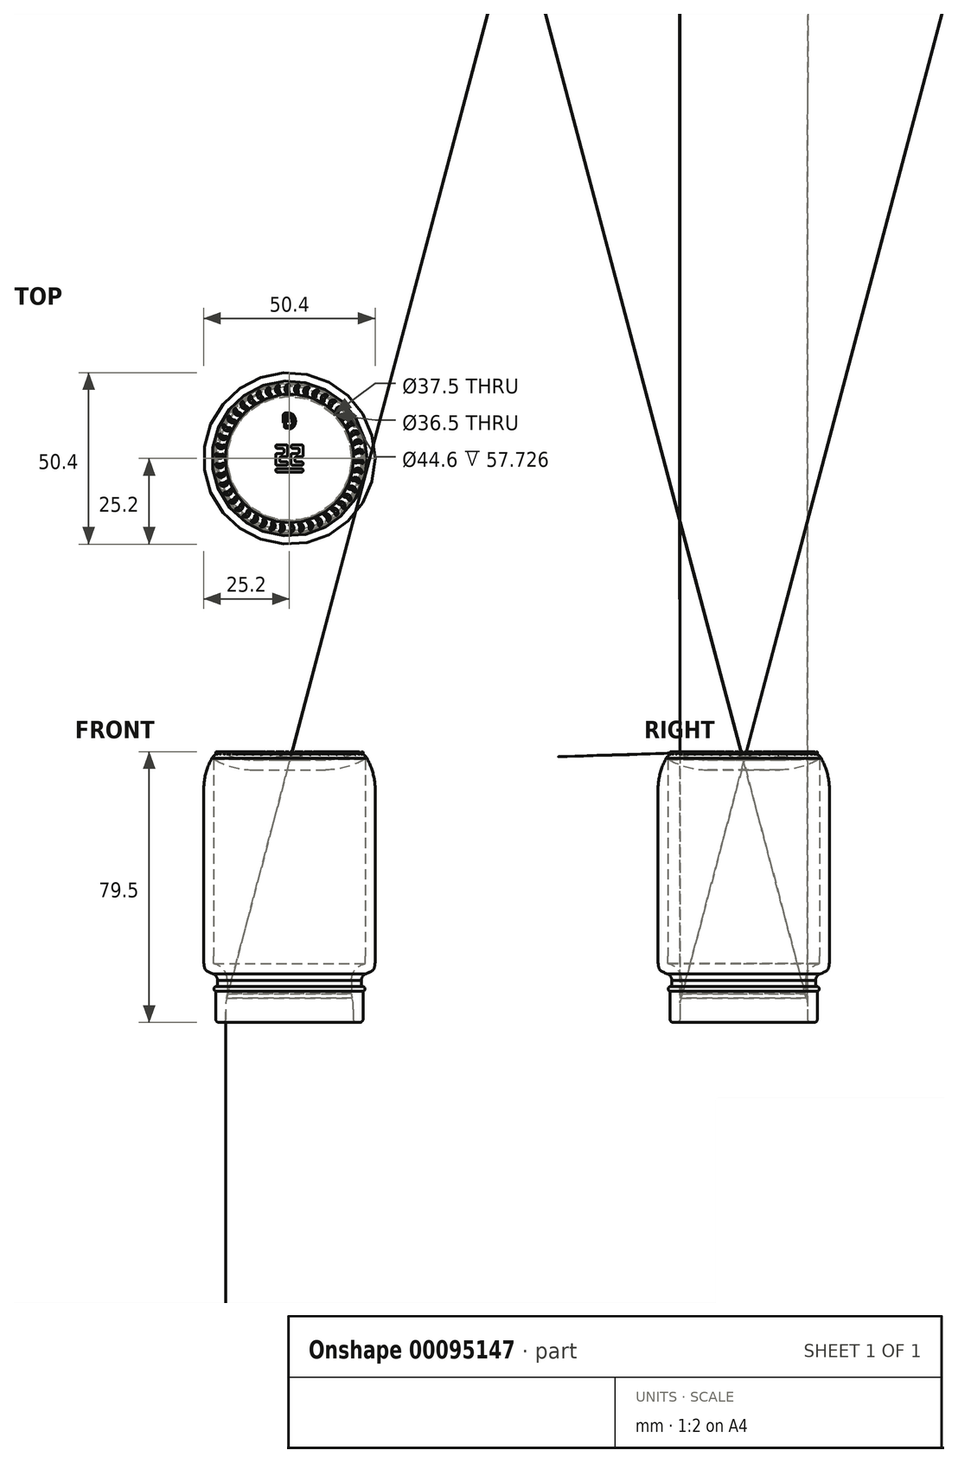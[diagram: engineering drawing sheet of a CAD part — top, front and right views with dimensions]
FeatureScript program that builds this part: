
annotation { "Feature Type Name" : "Feature", "Feature Type Description" : "" }
export const myFeature = defineFeature(function(context is Context, id is Id, definition is map)
    precondition{}
    {
        {
            var Q0;
            Q0=qCreatedBy(makeId("Top.planeOp"),FACE);
            var sketch = newSketch(context, id + "F0", { "sketchPlane" : qUnion([Q0])});
            skCircle(sketch, "E0", {"center": v(0, 0) * mm, "radius": 21.65 * mm});
            skCircle(sketch, "E1", {"center": v(0, 0) * mm, "radius": 25.2 * mm});
            skCircle(sketch, "E2", {"center": v(0, 0) * mm, "radius": 21.15 * mm});
            skCircle(sketch, "E3", {"center": v(0, 0) * mm, "radius": 22.15 * mm});
            skSolve(sketch);
        }
        {
            var Q0;
            Q0=makeQuery(id+"F0.imprint","IMPRINT",FACE,{"disambiguationData":[TD([[makeQuery(id+"F0.imprint","IMPRINT",EDGE,{"derivedFrom":sQuery(id+"F0.wireOp",EDGE,"E0")}),1.0]])]});
            var Q1;
            Q1=makeQuery(id+"F0.imprint","IMPRINT",FACE,{"disambiguationData":[TD([[makeQuery(id+"F0.imprint","IMPRINT",EDGE,{"derivedFrom":sQuery(id+"F0.wireOp",EDGE,"E2")}),1.0]])]});
            extrude(context, id + "F1", {"entities" : qUnion([Q0, Q1]), "depth" : 10.6 * mm});
        }
        {
            var Q0;
            Q0=makeQuery(id+"F0.imprint","IMPRINT",FACE,{"disambiguationData":[TD([[makeQuery(id+"F0.imprint","IMPRINT",EDGE,{"derivedFrom":sQuery(id+"F0.wireOp",EDGE,"E2")}),1.0]])]});
            extrude(context, id + "F2", {"entities" : qUnion([Q0]), "operationType" : NewBodyOperationType.ADD, "depth" : 13.8 * mm, "hasSecondDirection" : true, "secondDirectionOppositeDirection" : false, "secondDirectionDepth" : 10.6 * mm});
        }
        {
            var Q0;
            Q0=makeQuery(id+"F0.imprint","IMPRINT",FACE,{"disambiguationData":[TD([[makeQuery(id+"F0.imprint","IMPRINT",EDGE,{"derivedFrom":sQuery(id+"F0.wireOp",EDGE,"E1")}),1.0]])]});
            var Q1;
            Q1=makeQuery(id+"F0.imprint","IMPRINT",FACE,{"disambiguationData":[TD([[makeQuery(id+"F0.imprint","IMPRINT",EDGE,{"derivedFrom":sQuery(id+"F0.wireOp",EDGE,"E0")}),-1.0]])]});
            var Q2;
            Q2=makeQuery(id+"F0.imprint","IMPRINT",FACE,{"disambiguationData":[TD([[makeQuery(id+"F0.imprint","IMPRINT",EDGE,{"derivedFrom":sQuery(id+"F0.wireOp",EDGE,"E0")}),1.0]])]});
            var Q3;
            Q3=makeQuery(id+"F0.imprint","IMPRINT",FACE,{"disambiguationData":[TD([[makeQuery(id+"F0.imprint","IMPRINT",EDGE,{"derivedFrom":sQuery(id+"F0.wireOp",EDGE,"E2")}),1.0]])]});
            extrude(context, id + "F3", {"entities" : qUnion([Q0, Q1, Q2, Q3]), "operationType" : NewBodyOperationType.ADD, "depth" : (15.8 + 64.3) * mm, "hasSecondDirection" : true, "secondDirectionOppositeDirection" : false, "secondDirectionDepth" : 13.8 * mm});
        }
        {
            var Q0;
            Q0=makeQuery(id+"F3.opExtrude","CAP_EDGE",EDGE,{"disambiguationData":[OSD([sQuery(id+"F0.wireOp",EDGE,"E1")])],"isStart":true});
            fillet(context, id + "F4", {"entities" : qUnion([Q0]), "radius" : 6 * mm, "tangentPropagation" : true, "rho" : .75, "crossSection" : FilletCrossSection.CONIC, "allowEdgeOverflow" : false});
        }
        {
            var Q0;
            Q0=makeQuery(id+"F4.opFillet","BLEND_EDGE",EDGE,{"blendedFrom":[makeQuery(id+"F3.opExtrude","CAP_EDGE",EDGE,{"disambiguationData":[OSD([sQuery(id+"F0.wireOp",EDGE,"E1")])],"isStart":true}),makeQuery(id+"F2.opExtrude","SWEPT_FACE",FACE,{"disambiguationData":[OSD([sQuery(id+"F0.wireOp",EDGE,"E2")])]})],"blendedInto":[makeQuery(id+"F2.opExtrude","SWEPT_FACE",FACE,{"disambiguationData":[OSD([sQuery(id+"F0.wireOp",EDGE,"E2")])]})]});
            fillet(context, id + "F5", {"entities" : qUnion([Q0]), "radius" : 2 * mm, "tangentPropagation" : true, "allowEdgeOverflow" : false});
        }
        {
            var Q0;
            Q0=makeQuery(id+"F0.imprint","IMPRINT",FACE,{"disambiguationData":[TD([[makeQuery(id+"F0.imprint","IMPRINT",EDGE,{"derivedFrom":sQuery(id+"F0.wireOp",EDGE,"E2")}),1.0]])]});
            extrude(context, id + "F6", {"entities" : qUnion([Q0]), "operationType" : NewBodyOperationType.REMOVE, "depth" : 80.1 * mm, "hasSecondDirection" : true, "secondDirectionOppositeDirection" : false, "secondDirectionDepth" : 77.1 * mm});
        }
        {
            var Q0;
            Q0=makeQuery(id+"F6.boolean.opBoolean","COPY",EDGE,{"derivedFrom":makeQuery(id+"F6.opExtrude","CAP_EDGE",EDGE,{"disambiguationData":[OSD([sQuery(id+"F0.wireOp",EDGE,"E2")])],"isStart":true})});
            fillet(context, id + "F7", {"entities" : qUnion([Q0]), "radius" : 20 * mm, "tangentPropagation" : true, "rho" : 0, "crossSection" : FilletCrossSection.CONIC, "allowEdgeOverflow" : false});
        }
        {
            var Q0;
            Q0=makeQuery(id+"F1.opExtrude","CAP_FACE",FACE,{"disambiguationData":[OSD([sQuery(id+"F0.wireOp",EDGE,"E0")])],"isStart":true});
            shell(context, id + "F8", {"entities" : qUnion([Q0]), "thickness" : 2.9 * mm});
        }
        {
            var Q0;
            Q0=makeQuery(id+"F0.imprint","IMPRINT",FACE,{"disambiguationData":[TD([[makeQuery(id+"F0.imprint","IMPRINT",EDGE,{"derivedFrom":sQuery(id+"F0.wireOp",EDGE,"E0")}),-1.0]])]});
            extrude(context, id + "F9", {"entities" : qUnion([Q0]), "operationType" : NewBodyOperationType.ADD, "depth" : 10.6 * mm, "hasSecondDirection" : true, "secondDirectionOppositeDirection" : false, "secondDirectionDepth" : 9.1 * mm});
        }
        {
            var Q0;
            {var subQ0=sQuery(id+"F0.wireOp",EDGE,"E0");Q0=makeQuery(id+"F8.opShell","OFFSET_EDGE",EDGE,{"disambiguationData":[OSD([subQ0]),TDD([makeQuery(id+"F1.opExtrude","CAP_EDGE",EDGE,{"disambiguationData":[OSD([subQ0])],"isStart":false})])]});}
            fillet(context, id + "F10", {"entities" : qUnion([Q0]), "radius" : 15 * mm, "tangentPropagation" : true, "rho" : .999, "crossSection" : FilletCrossSection.CONIC, "allowEdgeOverflow" : false});
        }
        {
            var Q0;
            Q0=makeQuery(id+"F9.opExtrude","CAP_EDGE",EDGE,{"disambiguationData":[OSD([sQuery(id+"F0.wireOp",EDGE,"E3")])],"isStart":false});
            var Q1;
            Q1=makeQuery(id+"F9.opExtrude","CAP_EDGE",EDGE,{"disambiguationData":[OSD([sQuery(id+"F0.wireOp",EDGE,"E3")])],"isStart":true});
            fillet(context, id + "F11", {"entities" : qUnion([Q0, Q1]), "radius" : .7 * mm, "tangentPropagation" : true, "allowEdgeOverflow" : false});
        }
        {
            var Q0;
            {var subQ0=sQuery(id+"F0.wireOp",EDGE,"E0");Q0=makeQuery(id+"F10.opFillet","BLEND_EDGE",EDGE,{"blendedFrom":[makeQuery(id+"F8.opShell","OFFSET_EDGE",EDGE,{"disambiguationData":[OSD([subQ0]),TDD([makeQuery(id+"F1.opExtrude","CAP_EDGE",EDGE,{"disambiguationData":[OSD([subQ0])],"isStart":false})])]}),makeQuery(id+"F8.opShell","OFFSET_FACE",FACE,{"disambiguationData":[OSD([sQuery(id+"F0.wireOp",EDGE,"E2")])]})],"blendedInto":[makeQuery(id+"F8.opShell","OFFSET_FACE",FACE,{"disambiguationData":[OSD([sQuery(id+"F0.wireOp",EDGE,"E2")])]})]});}
            fillet(context, id + "F12", {"entities" : qUnion([Q0]), "radius" : 5 * mm, "tangentPropagation" : true, "allowEdgeOverflow" : false});
        }
        {
            var Q0;
            Q0=makeQuery(id+"F3.opExtrude","CAP_EDGE",EDGE,{"disambiguationData":[OSD([sQuery(id+"F0.wireOp",EDGE,"E1")])],"isStart":false});
            fillet(context, id + "F13", {"entities" : qUnion([Q0]), "radius" : 20 * mm, "tangentPropagation" : true, "rho" : 0.5, "crossSection" : FilletCrossSection.CONIC, "allowEdgeOverflow" : false});
        }
        {
            var Q0;
            Q0=makeQuery(id+"F13.opFillet","BLEND_EDGE",EDGE,{"blendedFrom":[makeQuery(id+"F3.opExtrude","CAP_EDGE",EDGE,{"disambiguationData":[OSD([sQuery(id+"F0.wireOp",EDGE,"E1")])],"isStart":false}),makeQuery(id+"F7.opFillet","BLEND_FACE",FACE,{"disambiguationData":[OSD([sQuery(id+"F0.wireOp",EDGE,"E2")])]})],"blendedInto":[makeQuery(id+"F7.opFillet","BLEND_FACE",FACE,{"disambiguationData":[OSD([sQuery(id+"F0.wireOp",EDGE,"E2")])]})]});
            fillet(context, id + "F14", {"entities" : qUnion([Q0]), "radius" : 3 * mm, "tangentPropagation" : true, "allowEdgeOverflow" : false});
        }
        {
            var Q0;
            Q0=makeQuery(id+"F1.opExtrude","CAP_EDGE",EDGE,{"disambiguationData":[OSD([sQuery(id+"F0.wireOp",EDGE,"E0")])],"isStart":true});
            var Q1;
            {var subQ0=sQuery(id+"F0.wireOp",EDGE,"E0");Q1=makeQuery(id+"F8.opShell","OFFSET_EDGE",EDGE,{"disambiguationData":[OSD([subQ0]),TDD([makeQuery(id+"F1.opExtrude","CAP_EDGE",EDGE,{"disambiguationData":[OSD([subQ0])],"isStart":true})])]});}
            fillet(context, id + "F15", {"entities" : qUnion([Q0, Q1]), "radius" : 1 * mm, "tangentPropagation" : true, "allowEdgeOverflow" : false});
        }
        {
            var Q0;
            Q0=qCreatedBy(makeId("Top.planeOp"),FACE);
            var sketch = newSketch(context, id + "F16", { "sketchPlane" : qUnion([Q0])});
            skCircle(sketch, "E4", {"center": v(0, 0) * mm, "radius": 21.75 * mm, "construction": true});
            skCircle(sketch, "E5", {"center": v(0, 0) * mm, "radius": 19.3 * mm, "construction": true});
            skArc(sketch, "E6.MirrorCS", {"start": v(0, 19.3) * mm, "mid": v(-0.4, 20.52) * mm, "end": v(0, 21.75) * mm});
            skArc(sketch, "E7.MirrorCS", {"start": v(0, 21.75) * mm, "mid": v(-1.23, 20.52) * mm, "end": v(0, 19.3) * mm});
            skArc(sketch, "E8.1.0", {"start": v(2.96, 21.55) * mm, "mid": v(1.58, 20.5) * mm, "end": v(2.63, 19.12) * mm});
            skArc(sketch, "E8.1.1", {"start": v(2.63, 19.12) * mm, "mid": v(2.4, 20.39) * mm, "end": v(2.96, 21.55) * mm});
            skArc(sketch, "E8.2.0", {"start": v(5.87, 20.94) * mm, "mid": v(4.36, 20.1) * mm, "end": v(5.2, 18.58) * mm});
            skArc(sketch, "E8.2.1", {"start": v(5.2, 18.58) * mm, "mid": v(5.16, 19.87) * mm, "end": v(5.87, 20.94) * mm});
            skArc(sketch, "E8.3.0", {"start": v(8.67, 19.95) * mm, "mid": v(7.05, 19.31) * mm, "end": v(7.69, 17.7) * mm});
            skArc(sketch, "E8.3.1", {"start": v(7.69, 17.7) * mm, "mid": v(7.81, 18.98) * mm, "end": v(8.67, 19.95) * mm});
            skArc(sketch, "E8.4.0", {"start": v(11.3, 18.58) * mm, "mid": v(9.62, 18.17) * mm, "end": v(10.03, 16.49) * mm});
            skArc(sketch, "E8.4.1", {"start": v(10.03, 16.49) * mm, "mid": v(10.33, 17.74) * mm, "end": v(11.3, 18.58) * mm});
            skArc(sketch, "E8.5.0", {"start": v(13.73, 16.87) * mm, "mid": v(12, 16.7) * mm, "end": v(12.18, 14.97) * mm});
            skArc(sketch, "E8.5.1", {"start": v(12.18, 14.97) * mm, "mid": v(12.65, 16.17) * mm, "end": v(13.73, 16.87) * mm});
            skArc(sketch, "E8.6.0", {"start": v(15.9, 14.85) * mm, "mid": v(14.16, 14.9) * mm, "end": v(14.1, 13.17) * mm});
            skArc(sketch, "E8.6.1", {"start": v(14.1, 13.17) * mm, "mid": v(14.73, 14.3) * mm, "end": v(15.9, 14.85) * mm});
            skArc(sketch, "E8.7.0", {"start": v(17.77, 12.54) * mm, "mid": v(16.06, 12.84) * mm, "end": v(15.77, 11.13) * mm});
            skArc(sketch, "E8.7.1", {"start": v(15.77, 11.13) * mm, "mid": v(16.54, 12.16) * mm, "end": v(17.77, 12.54) * mm});
            skArc(sketch, "E8.8.0", {"start": v(19.31, 10) * mm, "mid": v(17.66, 10.53) * mm, "end": v(17.13, 8.88) * mm});
            skArc(sketch, "E8.8.1", {"start": v(17.13, 8.88) * mm, "mid": v(18.04, 9.8) * mm, "end": v(19.31, 10) * mm});
            skArc(sketch, "E8.9.0", {"start": v(20.5, 7.28) * mm, "mid": v(18.93, 8.03) * mm, "end": v(18.18, 6.46) * mm});
            skArc(sketch, "E8.9.1", {"start": v(18.18, 6.46) * mm, "mid": v(19.2, 7.25) * mm, "end": v(20.5, 7.28) * mm});
            skArc(sketch, "E8.10.0", {"start": v(21.3, 4.43) * mm, "mid": v(19.85, 5.38) * mm, "end": v(18.9, 3.93) * mm});
            skArc(sketch, "E8.10.1", {"start": v(18.9, 3.93) * mm, "mid": v(20.01, 4.56) * mm, "end": v(21.3, 4.43) * mm});
            skArc(sketch, "E8.11.0", {"start": v(21.7, 1.48) * mm, "mid": v(20.4, 2.62) * mm, "end": v(19.25, 1.32) * mm});
            skArc(sketch, "E8.11.1", {"start": v(19.25, 1.32) * mm, "mid": v(20.45, 1.8) * mm, "end": v(21.7, 1.48) * mm});
            skArc(sketch, "E8.12.0", {"start": v(21.7, -1.48) * mm, "mid": v(20.56, -0.18) * mm, "end": v(19.25, -1.32) * mm});
            skArc(sketch, "E8.12.1", {"start": v(19.25, -1.32) * mm, "mid": v(20.5, -1) * mm, "end": v(21.7, -1.48) * mm});
            skArc(sketch, "E8.13.0", {"start": v(21.3, -4.43) * mm, "mid": v(20.34, -2.98) * mm, "end": v(18.9, -3.93) * mm});
            skArc(sketch, "E8.13.1", {"start": v(18.9, -3.93) * mm, "mid": v(20.18, -3.79) * mm, "end": v(21.3, -4.43) * mm});
            skArc(sketch, "E8.14.0", {"start": v(20.5, -7.28) * mm, "mid": v(19.75, -5.72) * mm, "end": v(18.18, -6.46) * mm});
            skArc(sketch, "E8.14.1", {"start": v(18.18, -6.46) * mm, "mid": v(19.47, -6.5) * mm, "end": v(20.5, -7.28) * mm});
            skArc(sketch, "E8.15.0", {"start": v(19.31, -10) * mm, "mid": v(18.79, -8.35) * mm, "end": v(17.13, -8.88) * mm});
            skArc(sketch, "E8.15.1", {"start": v(17.13, -8.88) * mm, "mid": v(18.4, -9.1) * mm, "end": v(19.31, -10) * mm});
            skArc(sketch, "E8.16.0", {"start": v(17.77, -12.54) * mm, "mid": v(17.47, -10.83) * mm, "end": v(15.77, -11.13) * mm});
            skArc(sketch, "E8.16.1", {"start": v(15.77, -11.13) * mm, "mid": v(17, -11.51) * mm, "end": v(17.77, -12.54) * mm});
            skArc(sketch, "E8.17.0", {"start": v(15.9, -14.85) * mm, "mid": v(15.84, -13.11) * mm, "end": v(14.1, -13.17) * mm});
            skArc(sketch, "E8.17.1", {"start": v(14.1, -13.17) * mm, "mid": v(15.27, -13.72) * mm, "end": v(15.9, -14.85) * mm});
            skArc(sketch, "E8.18.0", {"start": v(13.73, -16.87) * mm, "mid": v(13.9, -15.15) * mm, "end": v(12.18, -14.97) * mm});
            skArc(sketch, "E8.18.1", {"start": v(12.18, -14.97) * mm, "mid": v(13.26, -15.67) * mm, "end": v(13.73, -16.87) * mm});
            skArc(sketch, "E8.19.0", {"start": v(11.3, -18.58) * mm, "mid": v(11.71, -16.9) * mm, "end": v(10.03, -16.49) * mm});
            skArc(sketch, "E8.19.1", {"start": v(10.03, -16.49) * mm, "mid": v(11, -17.33) * mm, "end": v(11.3, -18.58) * mm});
            skArc(sketch, "E8.20.0", {"start": v(8.67, -19.95) * mm, "mid": v(9.3, -18.34) * mm, "end": v(7.69, -17.7) * mm});
            skArc(sketch, "E8.20.1", {"start": v(7.69, -17.7) * mm, "mid": v(8.54, -18.67) * mm, "end": v(8.67, -19.95) * mm});
            skArc(sketch, "E8.21.0", {"start": v(5.87, -20.94) * mm, "mid": v(6.72, -19.43) * mm, "end": v(5.2, -18.58) * mm});
            skArc(sketch, "E8.21.1", {"start": v(5.2, -18.58) * mm, "mid": v(5.92, -19.66) * mm, "end": v(5.87, -20.94) * mm});
            skArc(sketch, "E8.22.0", {"start": v(2.96, -21.55) * mm, "mid": v(4, -20.17) * mm, "end": v(2.63, -19.12) * mm});
            skArc(sketch, "E8.22.1", {"start": v(2.63, -19.12) * mm, "mid": v(3.19, -20.28) * mm, "end": v(2.96, -21.55) * mm});
            skArc(sketch, "E8.23.0", {"start": v(0, -21.75) * mm, "mid": v(1.23, -20.52) * mm, "end": v(0, -19.3) * mm});
            skArc(sketch, "E8.23.1", {"start": v(0, -19.3) * mm, "mid": v(0.4, -20.52) * mm, "end": v(0, -21.75) * mm});
            skArc(sketch, "E8.24.0", {"start": v(-2.96, -21.55) * mm, "mid": v(-1.58, -20.5) * mm, "end": v(-2.63, -19.12) * mm});
            skArc(sketch, "E8.24.1", {"start": v(-2.63, -19.12) * mm, "mid": v(-2.4, -20.39) * mm, "end": v(-2.96, -21.55) * mm});
            skArc(sketch, "E8.25.0", {"start": v(-5.87, -20.94) * mm, "mid": v(-4.36, -20.1) * mm, "end": v(-5.2, -18.58) * mm});
            skArc(sketch, "E8.25.1", {"start": v(-5.2, -18.58) * mm, "mid": v(-5.16, -19.87) * mm, "end": v(-5.87, -20.94) * mm});
            skArc(sketch, "E8.26.0", {"start": v(-8.67, -19.95) * mm, "mid": v(-7.05, -19.31) * mm, "end": v(-7.69, -17.7) * mm});
            skArc(sketch, "E8.26.1", {"start": v(-7.69, -17.7) * mm, "mid": v(-7.81, -18.98) * mm, "end": v(-8.67, -19.95) * mm});
            skArc(sketch, "E8.27.0", {"start": v(-11.3, -18.58) * mm, "mid": v(-9.62, -18.17) * mm, "end": v(-10.03, -16.49) * mm});
            skArc(sketch, "E8.27.1", {"start": v(-10.03, -16.49) * mm, "mid": v(-10.33, -17.74) * mm, "end": v(-11.3, -18.58) * mm});
            skArc(sketch, "E8.28.0", {"start": v(-13.73, -16.87) * mm, "mid": v(-12, -16.7) * mm, "end": v(-12.18, -14.97) * mm});
            skArc(sketch, "E8.28.1", {"start": v(-12.18, -14.97) * mm, "mid": v(-12.65, -16.17) * mm, "end": v(-13.73, -16.87) * mm});
            skArc(sketch, "E8.29.0", {"start": v(-15.9, -14.85) * mm, "mid": v(-14.16, -14.9) * mm, "end": v(-14.1, -13.17) * mm});
            skArc(sketch, "E8.29.1", {"start": v(-14.1, -13.17) * mm, "mid": v(-14.73, -14.3) * mm, "end": v(-15.9, -14.85) * mm});
            skArc(sketch, "E8.30.0", {"start": v(-17.77, -12.54) * mm, "mid": v(-16.06, -12.84) * mm, "end": v(-15.77, -11.13) * mm});
            skArc(sketch, "E8.30.1", {"start": v(-15.77, -11.13) * mm, "mid": v(-16.54, -12.16) * mm, "end": v(-17.77, -12.54) * mm});
            skArc(sketch, "E8.31.0", {"start": v(-19.31, -10) * mm, "mid": v(-17.66, -10.53) * mm, "end": v(-17.13, -8.88) * mm});
            skArc(sketch, "E8.31.1", {"start": v(-17.13, -8.88) * mm, "mid": v(-18.04, -9.8) * mm, "end": v(-19.31, -10) * mm});
            skArc(sketch, "E8.32.0", {"start": v(-20.5, -7.28) * mm, "mid": v(-18.93, -8.03) * mm, "end": v(-18.18, -6.46) * mm});
            skArc(sketch, "E8.32.1", {"start": v(-18.18, -6.46) * mm, "mid": v(-19.2, -7.25) * mm, "end": v(-20.5, -7.28) * mm});
            skArc(sketch, "E8.33.0", {"start": v(-21.3, -4.43) * mm, "mid": v(-19.85, -5.38) * mm, "end": v(-18.9, -3.93) * mm});
            skArc(sketch, "E8.33.1", {"start": v(-18.9, -3.93) * mm, "mid": v(-20.01, -4.56) * mm, "end": v(-21.3, -4.43) * mm});
            skArc(sketch, "E8.34.0", {"start": v(-21.7, -1.48) * mm, "mid": v(-20.4, -2.62) * mm, "end": v(-19.25, -1.32) * mm});
            skArc(sketch, "E8.34.1", {"start": v(-19.25, -1.32) * mm, "mid": v(-20.45, -1.8) * mm, "end": v(-21.7, -1.48) * mm});
            skArc(sketch, "E8.35.0", {"start": v(-21.7, 1.48) * mm, "mid": v(-20.56, 0.18) * mm, "end": v(-19.25, 1.32) * mm});
            skArc(sketch, "E8.35.1", {"start": v(-19.25, 1.32) * mm, "mid": v(-20.5, 1) * mm, "end": v(-21.7, 1.48) * mm});
            skArc(sketch, "E8.36.0", {"start": v(-21.3, 4.43) * mm, "mid": v(-20.34, 2.98) * mm, "end": v(-18.9, 3.93) * mm});
            skArc(sketch, "E8.36.1", {"start": v(-18.9, 3.93) * mm, "mid": v(-20.18, 3.79) * mm, "end": v(-21.3, 4.43) * mm});
            skArc(sketch, "E8.37.0", {"start": v(-20.5, 7.28) * mm, "mid": v(-19.75, 5.72) * mm, "end": v(-18.18, 6.46) * mm});
            skArc(sketch, "E8.37.1", {"start": v(-18.18, 6.46) * mm, "mid": v(-19.47, 6.5) * mm, "end": v(-20.5, 7.28) * mm});
            skArc(sketch, "E8.38.0", {"start": v(-19.31, 10) * mm, "mid": v(-18.79, 8.35) * mm, "end": v(-17.13, 8.88) * mm});
            skArc(sketch, "E8.38.1", {"start": v(-17.13, 8.88) * mm, "mid": v(-18.4, 9.1) * mm, "end": v(-19.31, 10) * mm});
            skArc(sketch, "E8.39.0", {"start": v(-17.77, 12.54) * mm, "mid": v(-17.47, 10.83) * mm, "end": v(-15.77, 11.13) * mm});
            skArc(sketch, "E8.39.1", {"start": v(-15.77, 11.13) * mm, "mid": v(-17, 11.51) * mm, "end": v(-17.77, 12.54) * mm});
            skArc(sketch, "E8.40.0", {"start": v(-15.9, 14.85) * mm, "mid": v(-15.84, 13.11) * mm, "end": v(-14.1, 13.17) * mm});
            skArc(sketch, "E8.40.1", {"start": v(-14.1, 13.17) * mm, "mid": v(-15.27, 13.72) * mm, "end": v(-15.9, 14.85) * mm});
            skArc(sketch, "E8.41.0", {"start": v(-13.73, 16.87) * mm, "mid": v(-13.9, 15.15) * mm, "end": v(-12.18, 14.97) * mm});
            skArc(sketch, "E8.41.1", {"start": v(-12.18, 14.97) * mm, "mid": v(-13.26, 15.67) * mm, "end": v(-13.73, 16.87) * mm});
            skArc(sketch, "E8.42.0", {"start": v(-11.3, 18.58) * mm, "mid": v(-11.71, 16.9) * mm, "end": v(-10.03, 16.49) * mm});
            skArc(sketch, "E8.42.1", {"start": v(-10.03, 16.49) * mm, "mid": v(-11, 17.33) * mm, "end": v(-11.3, 18.58) * mm});
            skArc(sketch, "E8.43.0", {"start": v(-8.67, 19.95) * mm, "mid": v(-9.3, 18.34) * mm, "end": v(-7.69, 17.7) * mm});
            skArc(sketch, "E8.43.1", {"start": v(-7.69, 17.7) * mm, "mid": v(-8.54, 18.67) * mm, "end": v(-8.67, 19.95) * mm});
            skArc(sketch, "E8.44.0", {"start": v(-5.87, 20.94) * mm, "mid": v(-6.72, 19.43) * mm, "end": v(-5.2, 18.58) * mm});
            skArc(sketch, "E8.44.1", {"start": v(-5.2, 18.58) * mm, "mid": v(-5.92, 19.66) * mm, "end": v(-5.87, 20.94) * mm});
            skArc(sketch, "E8.45.0", {"start": v(-2.96, 21.55) * mm, "mid": v(-4, 20.17) * mm, "end": v(-2.63, 19.12) * mm});
            skArc(sketch, "E8.45.1", {"start": v(-2.63, 19.12) * mm, "mid": v(-3.19, 20.28) * mm, "end": v(-2.96, 21.55) * mm});
            skLineSegment(sketch, "E8.anchor1", {"start": v(0, 0) * mm, "end": v(0, 19.3) * mm, "construction": true});
            skLineSegment(sketch, "E8.anchor2", {"start": v(0, 0) * mm, "end": v(-2.63, 19.12) * mm, "construction": true});
            skSolve(sketch);
        }
        {
            var Q0;
            Q0 = qSketchRegion(id + "F16", true);
            extrude(context, id + "F17", {"entities" : qUnion([Q0]), "operationType" : NewBodyOperationType.ADD, "depth" : 79.5 * mm, "hasSecondDirection" : true, "secondDirectionOppositeDirection" : false, "secondDirectionDepth" : 77.1 * mm});
        }
        {
            var Q0;
            Q0=makeQuery(id+"F17.boolean.opBoolean","INTERSECT",EDGE,{"derivedFrom":[makeQuery(id+"F14.opFillet","BLEND_FACE",FACE,{"disambiguationData":[OSD([sQuery(id+"F0.wireOp",EDGE,"E1"),sQuery(id+"F0.wireOp",EDGE,"E2")])]}),makeQuery(id+"F17.opExtrude","SWEPT_FACE",FACE,{"disambiguationData":[OSD([sQuery(id+"F16.wireOp",EDGE,"E6.MirrorCS")])]})]});
            var Q1;
            Q1=makeQuery(id+"F17.boolean.opBoolean","INTERSECT",EDGE,{"derivedFrom":[makeQuery(id+"F14.opFillet","BLEND_FACE",FACE,{"disambiguationData":[OSD([sQuery(id+"F0.wireOp",EDGE,"E1"),sQuery(id+"F0.wireOp",EDGE,"E2")])]}),makeQuery(id+"F17.opExtrude","SWEPT_FACE",FACE,{"disambiguationData":[OSD([sQuery(id+"F16.wireOp",EDGE,"E7.MirrorCS")])]})]});
            var Q2;
            Q2=makeQuery(id+"F17.boolean.opBoolean","INTERSECT",EDGE,{"derivedFrom":[makeQuery(id+"F14.opFillet","BLEND_FACE",FACE,{"disambiguationData":[OSD([sQuery(id+"F0.wireOp",EDGE,"E1"),sQuery(id+"F0.wireOp",EDGE,"E2")])]}),makeQuery(id+"F17.opExtrude","SWEPT_FACE",FACE,{"disambiguationData":[OSD([sQuery(id+"F16.wireOp",EDGE,"E8.1.0")])]})]});
            var Q3;
            Q3=makeQuery(id+"F17.boolean.opBoolean","INTERSECT",EDGE,{"derivedFrom":[makeQuery(id+"F14.opFillet","BLEND_FACE",FACE,{"disambiguationData":[OSD([sQuery(id+"F0.wireOp",EDGE,"E1"),sQuery(id+"F0.wireOp",EDGE,"E2")])]}),makeQuery(id+"F17.opExtrude","SWEPT_FACE",FACE,{"disambiguationData":[OSD([sQuery(id+"F16.wireOp",EDGE,"E8.1.1")])]})]});
            var Q4;
            Q4=makeQuery(id+"F17.boolean.opBoolean","INTERSECT",EDGE,{"derivedFrom":[makeQuery(id+"F14.opFillet","BLEND_FACE",FACE,{"disambiguationData":[OSD([sQuery(id+"F0.wireOp",EDGE,"E1"),sQuery(id+"F0.wireOp",EDGE,"E2")])]}),makeQuery(id+"F17.opExtrude","SWEPT_FACE",FACE,{"disambiguationData":[OSD([sQuery(id+"F16.wireOp",EDGE,"E8.2.0")])]})]});
            var Q5;
            Q5=makeQuery(id+"F17.boolean.opBoolean","INTERSECT",EDGE,{"derivedFrom":[makeQuery(id+"F14.opFillet","BLEND_FACE",FACE,{"disambiguationData":[OSD([sQuery(id+"F0.wireOp",EDGE,"E1"),sQuery(id+"F0.wireOp",EDGE,"E2")])]}),makeQuery(id+"F17.opExtrude","SWEPT_FACE",FACE,{"disambiguationData":[OSD([sQuery(id+"F16.wireOp",EDGE,"E8.2.1")])]})]});
            var Q6;
            Q6=makeQuery(id+"F17.boolean.opBoolean","INTERSECT",EDGE,{"derivedFrom":[makeQuery(id+"F14.opFillet","BLEND_FACE",FACE,{"disambiguationData":[OSD([sQuery(id+"F0.wireOp",EDGE,"E1"),sQuery(id+"F0.wireOp",EDGE,"E2")])]}),makeQuery(id+"F17.opExtrude","SWEPT_FACE",FACE,{"disambiguationData":[OSD([sQuery(id+"F16.wireOp",EDGE,"E8.3.0")])]})]});
            var Q7;
            Q7=makeQuery(id+"F17.boolean.opBoolean","INTERSECT",EDGE,{"derivedFrom":[makeQuery(id+"F14.opFillet","BLEND_FACE",FACE,{"disambiguationData":[OSD([sQuery(id+"F0.wireOp",EDGE,"E1"),sQuery(id+"F0.wireOp",EDGE,"E2")])]}),makeQuery(id+"F17.opExtrude","SWEPT_FACE",FACE,{"disambiguationData":[OSD([sQuery(id+"F16.wireOp",EDGE,"E8.3.1")])]})]});
            var Q8;
            Q8=makeQuery(id+"F17.boolean.opBoolean","INTERSECT",EDGE,{"derivedFrom":[makeQuery(id+"F14.opFillet","BLEND_FACE",FACE,{"disambiguationData":[OSD([sQuery(id+"F0.wireOp",EDGE,"E1"),sQuery(id+"F0.wireOp",EDGE,"E2")])]}),makeQuery(id+"F17.opExtrude","SWEPT_FACE",FACE,{"disambiguationData":[OSD([sQuery(id+"F16.wireOp",EDGE,"E8.4.0")])]})]});
            var Q9;
            Q9=makeQuery(id+"F17.boolean.opBoolean","INTERSECT",EDGE,{"derivedFrom":[makeQuery(id+"F14.opFillet","BLEND_FACE",FACE,{"disambiguationData":[OSD([sQuery(id+"F0.wireOp",EDGE,"E1"),sQuery(id+"F0.wireOp",EDGE,"E2")])]}),makeQuery(id+"F17.opExtrude","SWEPT_FACE",FACE,{"disambiguationData":[OSD([sQuery(id+"F16.wireOp",EDGE,"E8.4.1")])]})]});
            var Q10;
            Q10=makeQuery(id+"F17.boolean.opBoolean","INTERSECT",EDGE,{"derivedFrom":[makeQuery(id+"F14.opFillet","BLEND_FACE",FACE,{"disambiguationData":[OSD([sQuery(id+"F0.wireOp",EDGE,"E1"),sQuery(id+"F0.wireOp",EDGE,"E2")])]}),makeQuery(id+"F17.opExtrude","SWEPT_FACE",FACE,{"disambiguationData":[OSD([sQuery(id+"F16.wireOp",EDGE,"E8.5.0")])]})]});
            var Q11;
            Q11=makeQuery(id+"F17.boolean.opBoolean","INTERSECT",EDGE,{"derivedFrom":[makeQuery(id+"F14.opFillet","BLEND_FACE",FACE,{"disambiguationData":[OSD([sQuery(id+"F0.wireOp",EDGE,"E1"),sQuery(id+"F0.wireOp",EDGE,"E2")])]}),makeQuery(id+"F17.opExtrude","SWEPT_FACE",FACE,{"disambiguationData":[OSD([sQuery(id+"F16.wireOp",EDGE,"E8.5.1")])]})]});
            var Q12;
            Q12=makeQuery(id+"F17.boolean.opBoolean","INTERSECT",EDGE,{"derivedFrom":[makeQuery(id+"F14.opFillet","BLEND_FACE",FACE,{"disambiguationData":[OSD([sQuery(id+"F0.wireOp",EDGE,"E1"),sQuery(id+"F0.wireOp",EDGE,"E2")])]}),makeQuery(id+"F17.opExtrude","SWEPT_FACE",FACE,{"disambiguationData":[OSD([sQuery(id+"F16.wireOp",EDGE,"E8.6.0")])]})]});
            var Q13;
            Q13=makeQuery(id+"F17.boolean.opBoolean","INTERSECT",EDGE,{"derivedFrom":[makeQuery(id+"F14.opFillet","BLEND_FACE",FACE,{"disambiguationData":[OSD([sQuery(id+"F0.wireOp",EDGE,"E1"),sQuery(id+"F0.wireOp",EDGE,"E2")])]}),makeQuery(id+"F17.opExtrude","SWEPT_FACE",FACE,{"disambiguationData":[OSD([sQuery(id+"F16.wireOp",EDGE,"E8.6.1")])]})]});
            var Q14;
            Q14=makeQuery(id+"F17.boolean.opBoolean","INTERSECT",EDGE,{"derivedFrom":[makeQuery(id+"F14.opFillet","BLEND_FACE",FACE,{"disambiguationData":[OSD([sQuery(id+"F0.wireOp",EDGE,"E1"),sQuery(id+"F0.wireOp",EDGE,"E2")])]}),makeQuery(id+"F17.opExtrude","SWEPT_FACE",FACE,{"disambiguationData":[OSD([sQuery(id+"F16.wireOp",EDGE,"E8.7.0")])]})]});
            var Q15;
            Q15=makeQuery(id+"F17.boolean.opBoolean","INTERSECT",EDGE,{"derivedFrom":[makeQuery(id+"F14.opFillet","BLEND_FACE",FACE,{"disambiguationData":[OSD([sQuery(id+"F0.wireOp",EDGE,"E1"),sQuery(id+"F0.wireOp",EDGE,"E2")])]}),makeQuery(id+"F17.opExtrude","SWEPT_FACE",FACE,{"disambiguationData":[OSD([sQuery(id+"F16.wireOp",EDGE,"E8.7.1")])]})]});
            var Q16;
            Q16=makeQuery(id+"F17.boolean.opBoolean","INTERSECT",EDGE,{"derivedFrom":[makeQuery(id+"F14.opFillet","BLEND_FACE",FACE,{"disambiguationData":[OSD([sQuery(id+"F0.wireOp",EDGE,"E1"),sQuery(id+"F0.wireOp",EDGE,"E2")])]}),makeQuery(id+"F17.opExtrude","SWEPT_FACE",FACE,{"disambiguationData":[OSD([sQuery(id+"F16.wireOp",EDGE,"E8.8.0")])]})]});
            var Q17;
            Q17=makeQuery(id+"F17.boolean.opBoolean","INTERSECT",EDGE,{"derivedFrom":[makeQuery(id+"F14.opFillet","BLEND_FACE",FACE,{"disambiguationData":[OSD([sQuery(id+"F0.wireOp",EDGE,"E1"),sQuery(id+"F0.wireOp",EDGE,"E2")])]}),makeQuery(id+"F17.opExtrude","SWEPT_FACE",FACE,{"disambiguationData":[OSD([sQuery(id+"F16.wireOp",EDGE,"E8.8.1")])]})]});
            var Q18;
            Q18=makeQuery(id+"F17.boolean.opBoolean","INTERSECT",EDGE,{"derivedFrom":[makeQuery(id+"F14.opFillet","BLEND_FACE",FACE,{"disambiguationData":[OSD([sQuery(id+"F0.wireOp",EDGE,"E1"),sQuery(id+"F0.wireOp",EDGE,"E2")])]}),makeQuery(id+"F17.opExtrude","SWEPT_FACE",FACE,{"disambiguationData":[OSD([sQuery(id+"F16.wireOp",EDGE,"E8.9.0")])]})]});
            var Q19;
            Q19=makeQuery(id+"F17.boolean.opBoolean","INTERSECT",EDGE,{"derivedFrom":[makeQuery(id+"F14.opFillet","BLEND_FACE",FACE,{"disambiguationData":[OSD([sQuery(id+"F0.wireOp",EDGE,"E1"),sQuery(id+"F0.wireOp",EDGE,"E2")])]}),makeQuery(id+"F17.opExtrude","SWEPT_FACE",FACE,{"disambiguationData":[OSD([sQuery(id+"F16.wireOp",EDGE,"E8.9.1")])]})]});
            var Q20;
            Q20=makeQuery(id+"F17.boolean.opBoolean","INTERSECT",EDGE,{"derivedFrom":[makeQuery(id+"F14.opFillet","BLEND_FACE",FACE,{"disambiguationData":[OSD([sQuery(id+"F0.wireOp",EDGE,"E1"),sQuery(id+"F0.wireOp",EDGE,"E2")])]}),makeQuery(id+"F17.opExtrude","SWEPT_FACE",FACE,{"disambiguationData":[OSD([sQuery(id+"F16.wireOp",EDGE,"E8.10.0")])]})]});
            var Q21;
            Q21=makeQuery(id+"F17.boolean.opBoolean","INTERSECT",EDGE,{"derivedFrom":[makeQuery(id+"F14.opFillet","BLEND_FACE",FACE,{"disambiguationData":[OSD([sQuery(id+"F0.wireOp",EDGE,"E1"),sQuery(id+"F0.wireOp",EDGE,"E2")])]}),makeQuery(id+"F17.opExtrude","SWEPT_FACE",FACE,{"disambiguationData":[OSD([sQuery(id+"F16.wireOp",EDGE,"E8.10.1")])]})]});
            var Q22;
            Q22=makeQuery(id+"F17.boolean.opBoolean","INTERSECT",EDGE,{"derivedFrom":[makeQuery(id+"F14.opFillet","BLEND_FACE",FACE,{"disambiguationData":[OSD([sQuery(id+"F0.wireOp",EDGE,"E1"),sQuery(id+"F0.wireOp",EDGE,"E2")])]}),makeQuery(id+"F17.opExtrude","SWEPT_FACE",FACE,{"disambiguationData":[OSD([sQuery(id+"F16.wireOp",EDGE,"E8.11.0")])]})]});
            var Q23;
            Q23=makeQuery(id+"F17.boolean.opBoolean","INTERSECT",EDGE,{"derivedFrom":[makeQuery(id+"F14.opFillet","BLEND_FACE",FACE,{"disambiguationData":[OSD([sQuery(id+"F0.wireOp",EDGE,"E1"),sQuery(id+"F0.wireOp",EDGE,"E2")])]}),makeQuery(id+"F17.opExtrude","SWEPT_FACE",FACE,{"disambiguationData":[OSD([sQuery(id+"F16.wireOp",EDGE,"E8.11.1")])]})]});
            var Q24;
            Q24=makeQuery(id+"F17.boolean.opBoolean","INTERSECT",EDGE,{"derivedFrom":[makeQuery(id+"F14.opFillet","BLEND_FACE",FACE,{"disambiguationData":[OSD([sQuery(id+"F0.wireOp",EDGE,"E1"),sQuery(id+"F0.wireOp",EDGE,"E2")])]}),makeQuery(id+"F17.opExtrude","SWEPT_FACE",FACE,{"disambiguationData":[OSD([sQuery(id+"F16.wireOp",EDGE,"E8.12.0")])]})]});
            var Q25;
            Q25=makeQuery(id+"F17.boolean.opBoolean","INTERSECT",EDGE,{"derivedFrom":[makeQuery(id+"F14.opFillet","BLEND_FACE",FACE,{"disambiguationData":[OSD([sQuery(id+"F0.wireOp",EDGE,"E1"),sQuery(id+"F0.wireOp",EDGE,"E2")])]}),makeQuery(id+"F17.opExtrude","SWEPT_FACE",FACE,{"disambiguationData":[OSD([sQuery(id+"F16.wireOp",EDGE,"E8.12.1")])]})]});
            var Q26;
            Q26=makeQuery(id+"F17.boolean.opBoolean","INTERSECT",EDGE,{"derivedFrom":[makeQuery(id+"F14.opFillet","BLEND_FACE",FACE,{"disambiguationData":[OSD([sQuery(id+"F0.wireOp",EDGE,"E1"),sQuery(id+"F0.wireOp",EDGE,"E2")])]}),makeQuery(id+"F17.opExtrude","SWEPT_FACE",FACE,{"disambiguationData":[OSD([sQuery(id+"F16.wireOp",EDGE,"E8.13.0")])]})]});
            var Q27;
            Q27=makeQuery(id+"F17.boolean.opBoolean","INTERSECT",EDGE,{"derivedFrom":[makeQuery(id+"F14.opFillet","BLEND_FACE",FACE,{"disambiguationData":[OSD([sQuery(id+"F0.wireOp",EDGE,"E1"),sQuery(id+"F0.wireOp",EDGE,"E2")])]}),makeQuery(id+"F17.opExtrude","SWEPT_FACE",FACE,{"disambiguationData":[OSD([sQuery(id+"F16.wireOp",EDGE,"E8.13.1")])]})]});
            var Q28;
            Q28=makeQuery(id+"F17.boolean.opBoolean","INTERSECT",EDGE,{"derivedFrom":[makeQuery(id+"F14.opFillet","BLEND_FACE",FACE,{"disambiguationData":[OSD([sQuery(id+"F0.wireOp",EDGE,"E1"),sQuery(id+"F0.wireOp",EDGE,"E2")])]}),makeQuery(id+"F17.opExtrude","SWEPT_FACE",FACE,{"disambiguationData":[OSD([sQuery(id+"F16.wireOp",EDGE,"E8.14.0")])]})]});
            var Q29;
            Q29=makeQuery(id+"F17.boolean.opBoolean","INTERSECT",EDGE,{"derivedFrom":[makeQuery(id+"F14.opFillet","BLEND_FACE",FACE,{"disambiguationData":[OSD([sQuery(id+"F0.wireOp",EDGE,"E1"),sQuery(id+"F0.wireOp",EDGE,"E2")])]}),makeQuery(id+"F17.opExtrude","SWEPT_FACE",FACE,{"disambiguationData":[OSD([sQuery(id+"F16.wireOp",EDGE,"E8.14.1")])]})]});
            var Q30;
            Q30=makeQuery(id+"F17.boolean.opBoolean","INTERSECT",EDGE,{"derivedFrom":[makeQuery(id+"F14.opFillet","BLEND_FACE",FACE,{"disambiguationData":[OSD([sQuery(id+"F0.wireOp",EDGE,"E1"),sQuery(id+"F0.wireOp",EDGE,"E2")])]}),makeQuery(id+"F17.opExtrude","SWEPT_FACE",FACE,{"disambiguationData":[OSD([sQuery(id+"F16.wireOp",EDGE,"E8.15.0")])]})]});
            var Q31;
            Q31=makeQuery(id+"F17.boolean.opBoolean","INTERSECT",EDGE,{"derivedFrom":[makeQuery(id+"F14.opFillet","BLEND_FACE",FACE,{"disambiguationData":[OSD([sQuery(id+"F0.wireOp",EDGE,"E1"),sQuery(id+"F0.wireOp",EDGE,"E2")])]}),makeQuery(id+"F17.opExtrude","SWEPT_FACE",FACE,{"disambiguationData":[OSD([sQuery(id+"F16.wireOp",EDGE,"E8.15.1")])]})]});
            var Q32;
            Q32=makeQuery(id+"F17.boolean.opBoolean","INTERSECT",EDGE,{"derivedFrom":[makeQuery(id+"F14.opFillet","BLEND_FACE",FACE,{"disambiguationData":[OSD([sQuery(id+"F0.wireOp",EDGE,"E1"),sQuery(id+"F0.wireOp",EDGE,"E2")])]}),makeQuery(id+"F17.opExtrude","SWEPT_FACE",FACE,{"disambiguationData":[OSD([sQuery(id+"F16.wireOp",EDGE,"E8.16.0")])]})]});
            var Q33;
            Q33=makeQuery(id+"F17.boolean.opBoolean","INTERSECT",EDGE,{"derivedFrom":[makeQuery(id+"F14.opFillet","BLEND_FACE",FACE,{"disambiguationData":[OSD([sQuery(id+"F0.wireOp",EDGE,"E1"),sQuery(id+"F0.wireOp",EDGE,"E2")])]}),makeQuery(id+"F17.opExtrude","SWEPT_FACE",FACE,{"disambiguationData":[OSD([sQuery(id+"F16.wireOp",EDGE,"E8.16.1")])]})]});
            var Q34;
            Q34=makeQuery(id+"F17.boolean.opBoolean","INTERSECT",EDGE,{"derivedFrom":[makeQuery(id+"F14.opFillet","BLEND_FACE",FACE,{"disambiguationData":[OSD([sQuery(id+"F0.wireOp",EDGE,"E1"),sQuery(id+"F0.wireOp",EDGE,"E2")])]}),makeQuery(id+"F17.opExtrude","SWEPT_FACE",FACE,{"disambiguationData":[OSD([sQuery(id+"F16.wireOp",EDGE,"E8.17.0")])]})]});
            var Q35;
            Q35=makeQuery(id+"F17.boolean.opBoolean","INTERSECT",EDGE,{"derivedFrom":[makeQuery(id+"F14.opFillet","BLEND_FACE",FACE,{"disambiguationData":[OSD([sQuery(id+"F0.wireOp",EDGE,"E1"),sQuery(id+"F0.wireOp",EDGE,"E2")])]}),makeQuery(id+"F17.opExtrude","SWEPT_FACE",FACE,{"disambiguationData":[OSD([sQuery(id+"F16.wireOp",EDGE,"E8.17.1")])]})]});
            var Q36;
            Q36=makeQuery(id+"F17.boolean.opBoolean","INTERSECT",EDGE,{"derivedFrom":[makeQuery(id+"F14.opFillet","BLEND_FACE",FACE,{"disambiguationData":[OSD([sQuery(id+"F0.wireOp",EDGE,"E1"),sQuery(id+"F0.wireOp",EDGE,"E2")])]}),makeQuery(id+"F17.opExtrude","SWEPT_FACE",FACE,{"disambiguationData":[OSD([sQuery(id+"F16.wireOp",EDGE,"E8.18.0")])]})]});
            var Q37;
            Q37=makeQuery(id+"F17.boolean.opBoolean","INTERSECT",EDGE,{"derivedFrom":[makeQuery(id+"F14.opFillet","BLEND_FACE",FACE,{"disambiguationData":[OSD([sQuery(id+"F0.wireOp",EDGE,"E1"),sQuery(id+"F0.wireOp",EDGE,"E2")])]}),makeQuery(id+"F17.opExtrude","SWEPT_FACE",FACE,{"disambiguationData":[OSD([sQuery(id+"F16.wireOp",EDGE,"E8.18.1")])]})]});
            var Q38;
            Q38=makeQuery(id+"F17.boolean.opBoolean","INTERSECT",EDGE,{"derivedFrom":[makeQuery(id+"F14.opFillet","BLEND_FACE",FACE,{"disambiguationData":[OSD([sQuery(id+"F0.wireOp",EDGE,"E1"),sQuery(id+"F0.wireOp",EDGE,"E2")])]}),makeQuery(id+"F17.opExtrude","SWEPT_FACE",FACE,{"disambiguationData":[OSD([sQuery(id+"F16.wireOp",EDGE,"E8.19.0")])]})]});
            var Q39;
            Q39=makeQuery(id+"F17.boolean.opBoolean","INTERSECT",EDGE,{"derivedFrom":[makeQuery(id+"F14.opFillet","BLEND_FACE",FACE,{"disambiguationData":[OSD([sQuery(id+"F0.wireOp",EDGE,"E1"),sQuery(id+"F0.wireOp",EDGE,"E2")])]}),makeQuery(id+"F17.opExtrude","SWEPT_FACE",FACE,{"disambiguationData":[OSD([sQuery(id+"F16.wireOp",EDGE,"E8.19.1")])]})]});
            var Q40;
            Q40=makeQuery(id+"F17.boolean.opBoolean","INTERSECT",EDGE,{"derivedFrom":[makeQuery(id+"F14.opFillet","BLEND_FACE",FACE,{"disambiguationData":[OSD([sQuery(id+"F0.wireOp",EDGE,"E1"),sQuery(id+"F0.wireOp",EDGE,"E2")])]}),makeQuery(id+"F17.opExtrude","SWEPT_FACE",FACE,{"disambiguationData":[OSD([sQuery(id+"F16.wireOp",EDGE,"E8.20.0")])]})]});
            var Q41;
            Q41=makeQuery(id+"F17.boolean.opBoolean","INTERSECT",EDGE,{"derivedFrom":[makeQuery(id+"F14.opFillet","BLEND_FACE",FACE,{"disambiguationData":[OSD([sQuery(id+"F0.wireOp",EDGE,"E1"),sQuery(id+"F0.wireOp",EDGE,"E2")])]}),makeQuery(id+"F17.opExtrude","SWEPT_FACE",FACE,{"disambiguationData":[OSD([sQuery(id+"F16.wireOp",EDGE,"E8.20.1")])]})]});
            var Q42;
            Q42=makeQuery(id+"F17.boolean.opBoolean","INTERSECT",EDGE,{"derivedFrom":[makeQuery(id+"F14.opFillet","BLEND_FACE",FACE,{"disambiguationData":[OSD([sQuery(id+"F0.wireOp",EDGE,"E1"),sQuery(id+"F0.wireOp",EDGE,"E2")])]}),makeQuery(id+"F17.opExtrude","SWEPT_FACE",FACE,{"disambiguationData":[OSD([sQuery(id+"F16.wireOp",EDGE,"E8.21.0")])]})]});
            var Q43;
            Q43=makeQuery(id+"F17.boolean.opBoolean","INTERSECT",EDGE,{"derivedFrom":[makeQuery(id+"F14.opFillet","BLEND_FACE",FACE,{"disambiguationData":[OSD([sQuery(id+"F0.wireOp",EDGE,"E1"),sQuery(id+"F0.wireOp",EDGE,"E2")])]}),makeQuery(id+"F17.opExtrude","SWEPT_FACE",FACE,{"disambiguationData":[OSD([sQuery(id+"F16.wireOp",EDGE,"E8.21.1")])]})]});
            var Q44;
            Q44=makeQuery(id+"F17.boolean.opBoolean","INTERSECT",EDGE,{"derivedFrom":[makeQuery(id+"F14.opFillet","BLEND_FACE",FACE,{"disambiguationData":[OSD([sQuery(id+"F0.wireOp",EDGE,"E1"),sQuery(id+"F0.wireOp",EDGE,"E2")])]}),makeQuery(id+"F17.opExtrude","SWEPT_FACE",FACE,{"disambiguationData":[OSD([sQuery(id+"F16.wireOp",EDGE,"E8.22.0")])]})]});
            var Q45;
            Q45=makeQuery(id+"F17.boolean.opBoolean","INTERSECT",EDGE,{"derivedFrom":[makeQuery(id+"F14.opFillet","BLEND_FACE",FACE,{"disambiguationData":[OSD([sQuery(id+"F0.wireOp",EDGE,"E1"),sQuery(id+"F0.wireOp",EDGE,"E2")])]}),makeQuery(id+"F17.opExtrude","SWEPT_FACE",FACE,{"disambiguationData":[OSD([sQuery(id+"F16.wireOp",EDGE,"E8.22.1")])]})]});
            var Q46;
            Q46=makeQuery(id+"F17.boolean.opBoolean","INTERSECT",EDGE,{"derivedFrom":[makeQuery(id+"F14.opFillet","BLEND_FACE",FACE,{"disambiguationData":[OSD([sQuery(id+"F0.wireOp",EDGE,"E1"),sQuery(id+"F0.wireOp",EDGE,"E2")])]}),makeQuery(id+"F17.opExtrude","SWEPT_FACE",FACE,{"disambiguationData":[OSD([sQuery(id+"F16.wireOp",EDGE,"E8.23.0")])]})]});
            var Q47;
            Q47=makeQuery(id+"F17.boolean.opBoolean","INTERSECT",EDGE,{"derivedFrom":[makeQuery(id+"F14.opFillet","BLEND_FACE",FACE,{"disambiguationData":[OSD([sQuery(id+"F0.wireOp",EDGE,"E1"),sQuery(id+"F0.wireOp",EDGE,"E2")])]}),makeQuery(id+"F17.opExtrude","SWEPT_FACE",FACE,{"disambiguationData":[OSD([sQuery(id+"F16.wireOp",EDGE,"E8.23.1")])]})]});
            var Q48;
            Q48=makeQuery(id+"F17.boolean.opBoolean","INTERSECT",EDGE,{"derivedFrom":[makeQuery(id+"F14.opFillet","BLEND_FACE",FACE,{"disambiguationData":[OSD([sQuery(id+"F0.wireOp",EDGE,"E1"),sQuery(id+"F0.wireOp",EDGE,"E2")])]}),makeQuery(id+"F17.opExtrude","SWEPT_FACE",FACE,{"disambiguationData":[OSD([sQuery(id+"F16.wireOp",EDGE,"E8.24.0")])]})]});
            var Q49;
            Q49=makeQuery(id+"F17.boolean.opBoolean","INTERSECT",EDGE,{"derivedFrom":[makeQuery(id+"F14.opFillet","BLEND_FACE",FACE,{"disambiguationData":[OSD([sQuery(id+"F0.wireOp",EDGE,"E1"),sQuery(id+"F0.wireOp",EDGE,"E2")])]}),makeQuery(id+"F17.opExtrude","SWEPT_FACE",FACE,{"disambiguationData":[OSD([sQuery(id+"F16.wireOp",EDGE,"E8.24.1")])]})]});
            var Q50;
            Q50=makeQuery(id+"F17.boolean.opBoolean","INTERSECT",EDGE,{"derivedFrom":[makeQuery(id+"F14.opFillet","BLEND_FACE",FACE,{"disambiguationData":[OSD([sQuery(id+"F0.wireOp",EDGE,"E1"),sQuery(id+"F0.wireOp",EDGE,"E2")])]}),makeQuery(id+"F17.opExtrude","SWEPT_FACE",FACE,{"disambiguationData":[OSD([sQuery(id+"F16.wireOp",EDGE,"E8.25.0")])]})]});
            var Q51;
            Q51=makeQuery(id+"F17.boolean.opBoolean","INTERSECT",EDGE,{"derivedFrom":[makeQuery(id+"F14.opFillet","BLEND_FACE",FACE,{"disambiguationData":[OSD([sQuery(id+"F0.wireOp",EDGE,"E1"),sQuery(id+"F0.wireOp",EDGE,"E2")])]}),makeQuery(id+"F17.opExtrude","SWEPT_FACE",FACE,{"disambiguationData":[OSD([sQuery(id+"F16.wireOp",EDGE,"E8.25.1")])]})]});
            var Q52;
            Q52=makeQuery(id+"F17.boolean.opBoolean","INTERSECT",EDGE,{"derivedFrom":[makeQuery(id+"F14.opFillet","BLEND_FACE",FACE,{"disambiguationData":[OSD([sQuery(id+"F0.wireOp",EDGE,"E1"),sQuery(id+"F0.wireOp",EDGE,"E2")])]}),makeQuery(id+"F17.opExtrude","SWEPT_FACE",FACE,{"disambiguationData":[OSD([sQuery(id+"F16.wireOp",EDGE,"E8.26.0")])]})]});
            var Q53;
            Q53=makeQuery(id+"F17.boolean.opBoolean","INTERSECT",EDGE,{"derivedFrom":[makeQuery(id+"F14.opFillet","BLEND_FACE",FACE,{"disambiguationData":[OSD([sQuery(id+"F0.wireOp",EDGE,"E1"),sQuery(id+"F0.wireOp",EDGE,"E2")])]}),makeQuery(id+"F17.opExtrude","SWEPT_FACE",FACE,{"disambiguationData":[OSD([sQuery(id+"F16.wireOp",EDGE,"E8.26.1")])]})]});
            var Q54;
            Q54=makeQuery(id+"F17.boolean.opBoolean","INTERSECT",EDGE,{"derivedFrom":[makeQuery(id+"F14.opFillet","BLEND_FACE",FACE,{"disambiguationData":[OSD([sQuery(id+"F0.wireOp",EDGE,"E1"),sQuery(id+"F0.wireOp",EDGE,"E2")])]}),makeQuery(id+"F17.opExtrude","SWEPT_FACE",FACE,{"disambiguationData":[OSD([sQuery(id+"F16.wireOp",EDGE,"E8.27.0")])]})]});
            var Q55;
            Q55=makeQuery(id+"F17.boolean.opBoolean","INTERSECT",EDGE,{"derivedFrom":[makeQuery(id+"F14.opFillet","BLEND_FACE",FACE,{"disambiguationData":[OSD([sQuery(id+"F0.wireOp",EDGE,"E1"),sQuery(id+"F0.wireOp",EDGE,"E2")])]}),makeQuery(id+"F17.opExtrude","SWEPT_FACE",FACE,{"disambiguationData":[OSD([sQuery(id+"F16.wireOp",EDGE,"E8.27.1")])]})]});
            var Q56;
            Q56=makeQuery(id+"F17.boolean.opBoolean","INTERSECT",EDGE,{"derivedFrom":[makeQuery(id+"F14.opFillet","BLEND_FACE",FACE,{"disambiguationData":[OSD([sQuery(id+"F0.wireOp",EDGE,"E1"),sQuery(id+"F0.wireOp",EDGE,"E2")])]}),makeQuery(id+"F17.opExtrude","SWEPT_FACE",FACE,{"disambiguationData":[OSD([sQuery(id+"F16.wireOp",EDGE,"E8.28.0")])]})]});
            var Q57;
            Q57=makeQuery(id+"F17.boolean.opBoolean","INTERSECT",EDGE,{"derivedFrom":[makeQuery(id+"F14.opFillet","BLEND_FACE",FACE,{"disambiguationData":[OSD([sQuery(id+"F0.wireOp",EDGE,"E1"),sQuery(id+"F0.wireOp",EDGE,"E2")])]}),makeQuery(id+"F17.opExtrude","SWEPT_FACE",FACE,{"disambiguationData":[OSD([sQuery(id+"F16.wireOp",EDGE,"E8.28.1")])]})]});
            var Q58;
            Q58=makeQuery(id+"F17.boolean.opBoolean","INTERSECT",EDGE,{"derivedFrom":[makeQuery(id+"F14.opFillet","BLEND_FACE",FACE,{"disambiguationData":[OSD([sQuery(id+"F0.wireOp",EDGE,"E1"),sQuery(id+"F0.wireOp",EDGE,"E2")])]}),makeQuery(id+"F17.opExtrude","SWEPT_FACE",FACE,{"disambiguationData":[OSD([sQuery(id+"F16.wireOp",EDGE,"E8.29.0")])]})]});
            var Q59;
            Q59=makeQuery(id+"F17.boolean.opBoolean","INTERSECT",EDGE,{"derivedFrom":[makeQuery(id+"F14.opFillet","BLEND_FACE",FACE,{"disambiguationData":[OSD([sQuery(id+"F0.wireOp",EDGE,"E1"),sQuery(id+"F0.wireOp",EDGE,"E2")])]}),makeQuery(id+"F17.opExtrude","SWEPT_FACE",FACE,{"disambiguationData":[OSD([sQuery(id+"F16.wireOp",EDGE,"E8.29.1")])]})]});
            var Q60;
            Q60=makeQuery(id+"F17.boolean.opBoolean","INTERSECT",EDGE,{"derivedFrom":[makeQuery(id+"F14.opFillet","BLEND_FACE",FACE,{"disambiguationData":[OSD([sQuery(id+"F0.wireOp",EDGE,"E1"),sQuery(id+"F0.wireOp",EDGE,"E2")])]}),makeQuery(id+"F17.opExtrude","SWEPT_FACE",FACE,{"disambiguationData":[OSD([sQuery(id+"F16.wireOp",EDGE,"E8.30.0")])]})]});
            var Q61;
            Q61=makeQuery(id+"F17.boolean.opBoolean","INTERSECT",EDGE,{"derivedFrom":[makeQuery(id+"F14.opFillet","BLEND_FACE",FACE,{"disambiguationData":[OSD([sQuery(id+"F0.wireOp",EDGE,"E1"),sQuery(id+"F0.wireOp",EDGE,"E2")])]}),makeQuery(id+"F17.opExtrude","SWEPT_FACE",FACE,{"disambiguationData":[OSD([sQuery(id+"F16.wireOp",EDGE,"E8.30.1")])]})]});
            var Q62;
            Q62=makeQuery(id+"F17.boolean.opBoolean","INTERSECT",EDGE,{"derivedFrom":[makeQuery(id+"F14.opFillet","BLEND_FACE",FACE,{"disambiguationData":[OSD([sQuery(id+"F0.wireOp",EDGE,"E1"),sQuery(id+"F0.wireOp",EDGE,"E2")])]}),makeQuery(id+"F17.opExtrude","SWEPT_FACE",FACE,{"disambiguationData":[OSD([sQuery(id+"F16.wireOp",EDGE,"E8.31.0")])]})]});
            var Q63;
            Q63=makeQuery(id+"F17.boolean.opBoolean","INTERSECT",EDGE,{"derivedFrom":[makeQuery(id+"F14.opFillet","BLEND_FACE",FACE,{"disambiguationData":[OSD([sQuery(id+"F0.wireOp",EDGE,"E1"),sQuery(id+"F0.wireOp",EDGE,"E2")])]}),makeQuery(id+"F17.opExtrude","SWEPT_FACE",FACE,{"disambiguationData":[OSD([sQuery(id+"F16.wireOp",EDGE,"E8.31.1")])]})]});
            var Q64;
            Q64=makeQuery(id+"F17.boolean.opBoolean","INTERSECT",EDGE,{"derivedFrom":[makeQuery(id+"F14.opFillet","BLEND_FACE",FACE,{"disambiguationData":[OSD([sQuery(id+"F0.wireOp",EDGE,"E1"),sQuery(id+"F0.wireOp",EDGE,"E2")])]}),makeQuery(id+"F17.opExtrude","SWEPT_FACE",FACE,{"disambiguationData":[OSD([sQuery(id+"F16.wireOp",EDGE,"E8.32.0")])]})]});
            var Q65;
            Q65=makeQuery(id+"F17.boolean.opBoolean","INTERSECT",EDGE,{"derivedFrom":[makeQuery(id+"F14.opFillet","BLEND_FACE",FACE,{"disambiguationData":[OSD([sQuery(id+"F0.wireOp",EDGE,"E1"),sQuery(id+"F0.wireOp",EDGE,"E2")])]}),makeQuery(id+"F17.opExtrude","SWEPT_FACE",FACE,{"disambiguationData":[OSD([sQuery(id+"F16.wireOp",EDGE,"E8.32.1")])]})]});
            var Q66;
            Q66=makeQuery(id+"F17.boolean.opBoolean","INTERSECT",EDGE,{"derivedFrom":[makeQuery(id+"F14.opFillet","BLEND_FACE",FACE,{"disambiguationData":[OSD([sQuery(id+"F0.wireOp",EDGE,"E1"),sQuery(id+"F0.wireOp",EDGE,"E2")])]}),makeQuery(id+"F17.opExtrude","SWEPT_FACE",FACE,{"disambiguationData":[OSD([sQuery(id+"F16.wireOp",EDGE,"E8.33.0")])]})]});
            var Q67;
            Q67=makeQuery(id+"F17.boolean.opBoolean","INTERSECT",EDGE,{"derivedFrom":[makeQuery(id+"F14.opFillet","BLEND_FACE",FACE,{"disambiguationData":[OSD([sQuery(id+"F0.wireOp",EDGE,"E1"),sQuery(id+"F0.wireOp",EDGE,"E2")])]}),makeQuery(id+"F17.opExtrude","SWEPT_FACE",FACE,{"disambiguationData":[OSD([sQuery(id+"F16.wireOp",EDGE,"E8.33.1")])]})]});
            var Q68;
            Q68=makeQuery(id+"F17.boolean.opBoolean","INTERSECT",EDGE,{"derivedFrom":[makeQuery(id+"F14.opFillet","BLEND_FACE",FACE,{"disambiguationData":[OSD([sQuery(id+"F0.wireOp",EDGE,"E1"),sQuery(id+"F0.wireOp",EDGE,"E2")])]}),makeQuery(id+"F17.opExtrude","SWEPT_FACE",FACE,{"disambiguationData":[OSD([sQuery(id+"F16.wireOp",EDGE,"E8.34.0")])]})]});
            var Q69;
            Q69=makeQuery(id+"F17.boolean.opBoolean","INTERSECT",EDGE,{"derivedFrom":[makeQuery(id+"F14.opFillet","BLEND_FACE",FACE,{"disambiguationData":[OSD([sQuery(id+"F0.wireOp",EDGE,"E1"),sQuery(id+"F0.wireOp",EDGE,"E2")])]}),makeQuery(id+"F17.opExtrude","SWEPT_FACE",FACE,{"disambiguationData":[OSD([sQuery(id+"F16.wireOp",EDGE,"E8.34.1")])]})]});
            var Q70;
            Q70=makeQuery(id+"F17.boolean.opBoolean","INTERSECT",EDGE,{"derivedFrom":[makeQuery(id+"F14.opFillet","BLEND_FACE",FACE,{"disambiguationData":[OSD([sQuery(id+"F0.wireOp",EDGE,"E1"),sQuery(id+"F0.wireOp",EDGE,"E2")])]}),makeQuery(id+"F17.opExtrude","SWEPT_FACE",FACE,{"disambiguationData":[OSD([sQuery(id+"F16.wireOp",EDGE,"E8.35.0")])]})]});
            var Q71;
            Q71=makeQuery(id+"F17.boolean.opBoolean","INTERSECT",EDGE,{"derivedFrom":[makeQuery(id+"F14.opFillet","BLEND_FACE",FACE,{"disambiguationData":[OSD([sQuery(id+"F0.wireOp",EDGE,"E1"),sQuery(id+"F0.wireOp",EDGE,"E2")])]}),makeQuery(id+"F17.opExtrude","SWEPT_FACE",FACE,{"disambiguationData":[OSD([sQuery(id+"F16.wireOp",EDGE,"E8.35.1")])]})]});
            var Q72;
            Q72=makeQuery(id+"F17.boolean.opBoolean","INTERSECT",EDGE,{"derivedFrom":[makeQuery(id+"F14.opFillet","BLEND_FACE",FACE,{"disambiguationData":[OSD([sQuery(id+"F0.wireOp",EDGE,"E1"),sQuery(id+"F0.wireOp",EDGE,"E2")])]}),makeQuery(id+"F17.opExtrude","SWEPT_FACE",FACE,{"disambiguationData":[OSD([sQuery(id+"F16.wireOp",EDGE,"E8.36.0")])]})]});
            var Q73;
            Q73=makeQuery(id+"F17.boolean.opBoolean","INTERSECT",EDGE,{"derivedFrom":[makeQuery(id+"F14.opFillet","BLEND_FACE",FACE,{"disambiguationData":[OSD([sQuery(id+"F0.wireOp",EDGE,"E1"),sQuery(id+"F0.wireOp",EDGE,"E2")])]}),makeQuery(id+"F17.opExtrude","SWEPT_FACE",FACE,{"disambiguationData":[OSD([sQuery(id+"F16.wireOp",EDGE,"E8.36.1")])]})]});
            var Q74;
            Q74=makeQuery(id+"F17.boolean.opBoolean","INTERSECT",EDGE,{"derivedFrom":[makeQuery(id+"F14.opFillet","BLEND_FACE",FACE,{"disambiguationData":[OSD([sQuery(id+"F0.wireOp",EDGE,"E1"),sQuery(id+"F0.wireOp",EDGE,"E2")])]}),makeQuery(id+"F17.opExtrude","SWEPT_FACE",FACE,{"disambiguationData":[OSD([sQuery(id+"F16.wireOp",EDGE,"E8.37.0")])]})]});
            var Q75;
            Q75=makeQuery(id+"F17.boolean.opBoolean","INTERSECT",EDGE,{"derivedFrom":[makeQuery(id+"F14.opFillet","BLEND_FACE",FACE,{"disambiguationData":[OSD([sQuery(id+"F0.wireOp",EDGE,"E1"),sQuery(id+"F0.wireOp",EDGE,"E2")])]}),makeQuery(id+"F17.opExtrude","SWEPT_FACE",FACE,{"disambiguationData":[OSD([sQuery(id+"F16.wireOp",EDGE,"E8.37.1")])]})]});
            var Q76;
            Q76=makeQuery(id+"F17.boolean.opBoolean","INTERSECT",EDGE,{"derivedFrom":[makeQuery(id+"F14.opFillet","BLEND_FACE",FACE,{"disambiguationData":[OSD([sQuery(id+"F0.wireOp",EDGE,"E1"),sQuery(id+"F0.wireOp",EDGE,"E2")])]}),makeQuery(id+"F17.opExtrude","SWEPT_FACE",FACE,{"disambiguationData":[OSD([sQuery(id+"F16.wireOp",EDGE,"E8.38.0")])]})]});
            var Q77;
            Q77=makeQuery(id+"F17.boolean.opBoolean","INTERSECT",EDGE,{"derivedFrom":[makeQuery(id+"F14.opFillet","BLEND_FACE",FACE,{"disambiguationData":[OSD([sQuery(id+"F0.wireOp",EDGE,"E1"),sQuery(id+"F0.wireOp",EDGE,"E2")])]}),makeQuery(id+"F17.opExtrude","SWEPT_FACE",FACE,{"disambiguationData":[OSD([sQuery(id+"F16.wireOp",EDGE,"E8.38.1")])]})]});
            var Q78;
            Q78=makeQuery(id+"F17.boolean.opBoolean","INTERSECT",EDGE,{"derivedFrom":[makeQuery(id+"F14.opFillet","BLEND_FACE",FACE,{"disambiguationData":[OSD([sQuery(id+"F0.wireOp",EDGE,"E1"),sQuery(id+"F0.wireOp",EDGE,"E2")])]}),makeQuery(id+"F17.opExtrude","SWEPT_FACE",FACE,{"disambiguationData":[OSD([sQuery(id+"F16.wireOp",EDGE,"E8.39.0")])]})]});
            var Q79;
            Q79=makeQuery(id+"F17.boolean.opBoolean","INTERSECT",EDGE,{"derivedFrom":[makeQuery(id+"F14.opFillet","BLEND_FACE",FACE,{"disambiguationData":[OSD([sQuery(id+"F0.wireOp",EDGE,"E1"),sQuery(id+"F0.wireOp",EDGE,"E2")])]}),makeQuery(id+"F17.opExtrude","SWEPT_FACE",FACE,{"disambiguationData":[OSD([sQuery(id+"F16.wireOp",EDGE,"E8.39.1")])]})]});
            var Q80;
            Q80=makeQuery(id+"F17.boolean.opBoolean","INTERSECT",EDGE,{"derivedFrom":[makeQuery(id+"F14.opFillet","BLEND_FACE",FACE,{"disambiguationData":[OSD([sQuery(id+"F0.wireOp",EDGE,"E1"),sQuery(id+"F0.wireOp",EDGE,"E2")])]}),makeQuery(id+"F17.opExtrude","SWEPT_FACE",FACE,{"disambiguationData":[OSD([sQuery(id+"F16.wireOp",EDGE,"E8.40.0")])]})]});
            var Q81;
            Q81=makeQuery(id+"F17.boolean.opBoolean","INTERSECT",EDGE,{"derivedFrom":[makeQuery(id+"F14.opFillet","BLEND_FACE",FACE,{"disambiguationData":[OSD([sQuery(id+"F0.wireOp",EDGE,"E1"),sQuery(id+"F0.wireOp",EDGE,"E2")])]}),makeQuery(id+"F17.opExtrude","SWEPT_FACE",FACE,{"disambiguationData":[OSD([sQuery(id+"F16.wireOp",EDGE,"E8.40.1")])]})]});
            var Q82;
            Q82=makeQuery(id+"F17.boolean.opBoolean","INTERSECT",EDGE,{"derivedFrom":[makeQuery(id+"F14.opFillet","BLEND_FACE",FACE,{"disambiguationData":[OSD([sQuery(id+"F0.wireOp",EDGE,"E1"),sQuery(id+"F0.wireOp",EDGE,"E2")])]}),makeQuery(id+"F17.opExtrude","SWEPT_FACE",FACE,{"disambiguationData":[OSD([sQuery(id+"F16.wireOp",EDGE,"E8.41.0")])]})]});
            var Q83;
            Q83=makeQuery(id+"F17.boolean.opBoolean","INTERSECT",EDGE,{"derivedFrom":[makeQuery(id+"F14.opFillet","BLEND_FACE",FACE,{"disambiguationData":[OSD([sQuery(id+"F0.wireOp",EDGE,"E1"),sQuery(id+"F0.wireOp",EDGE,"E2")])]}),makeQuery(id+"F17.opExtrude","SWEPT_FACE",FACE,{"disambiguationData":[OSD([sQuery(id+"F16.wireOp",EDGE,"E8.41.1")])]})]});
            var Q84;
            Q84=makeQuery(id+"F17.boolean.opBoolean","INTERSECT",EDGE,{"derivedFrom":[makeQuery(id+"F14.opFillet","BLEND_FACE",FACE,{"disambiguationData":[OSD([sQuery(id+"F0.wireOp",EDGE,"E1"),sQuery(id+"F0.wireOp",EDGE,"E2")])]}),makeQuery(id+"F17.opExtrude","SWEPT_FACE",FACE,{"disambiguationData":[OSD([sQuery(id+"F16.wireOp",EDGE,"E8.42.0")])]})]});
            var Q85;
            Q85=makeQuery(id+"F17.boolean.opBoolean","INTERSECT",EDGE,{"derivedFrom":[makeQuery(id+"F14.opFillet","BLEND_FACE",FACE,{"disambiguationData":[OSD([sQuery(id+"F0.wireOp",EDGE,"E1"),sQuery(id+"F0.wireOp",EDGE,"E2")])]}),makeQuery(id+"F17.opExtrude","SWEPT_FACE",FACE,{"disambiguationData":[OSD([sQuery(id+"F16.wireOp",EDGE,"E8.42.1")])]})]});
            var Q86;
            Q86=makeQuery(id+"F17.boolean.opBoolean","INTERSECT",EDGE,{"derivedFrom":[makeQuery(id+"F14.opFillet","BLEND_FACE",FACE,{"disambiguationData":[OSD([sQuery(id+"F0.wireOp",EDGE,"E1"),sQuery(id+"F0.wireOp",EDGE,"E2")])]}),makeQuery(id+"F17.opExtrude","SWEPT_FACE",FACE,{"disambiguationData":[OSD([sQuery(id+"F16.wireOp",EDGE,"E8.43.0")])]})]});
            var Q87;
            Q87=makeQuery(id+"F17.boolean.opBoolean","INTERSECT",EDGE,{"derivedFrom":[makeQuery(id+"F14.opFillet","BLEND_FACE",FACE,{"disambiguationData":[OSD([sQuery(id+"F0.wireOp",EDGE,"E1"),sQuery(id+"F0.wireOp",EDGE,"E2")])]}),makeQuery(id+"F17.opExtrude","SWEPT_FACE",FACE,{"disambiguationData":[OSD([sQuery(id+"F16.wireOp",EDGE,"E8.43.1")])]})]});
            var Q88;
            Q88=makeQuery(id+"F17.boolean.opBoolean","INTERSECT",EDGE,{"derivedFrom":[makeQuery(id+"F14.opFillet","BLEND_FACE",FACE,{"disambiguationData":[OSD([sQuery(id+"F0.wireOp",EDGE,"E1"),sQuery(id+"F0.wireOp",EDGE,"E2")])]}),makeQuery(id+"F17.opExtrude","SWEPT_FACE",FACE,{"disambiguationData":[OSD([sQuery(id+"F16.wireOp",EDGE,"E8.44.0")])]})]});
            var Q89;
            Q89=makeQuery(id+"F17.boolean.opBoolean","INTERSECT",EDGE,{"derivedFrom":[makeQuery(id+"F14.opFillet","BLEND_FACE",FACE,{"disambiguationData":[OSD([sQuery(id+"F0.wireOp",EDGE,"E1"),sQuery(id+"F0.wireOp",EDGE,"E2")])]}),makeQuery(id+"F17.opExtrude","SWEPT_FACE",FACE,{"disambiguationData":[OSD([sQuery(id+"F16.wireOp",EDGE,"E8.44.1")])]})]});
            var Q90;
            Q90=makeQuery(id+"F17.boolean.opBoolean","INTERSECT",EDGE,{"derivedFrom":[makeQuery(id+"F14.opFillet","BLEND_FACE",FACE,{"disambiguationData":[OSD([sQuery(id+"F0.wireOp",EDGE,"E1"),sQuery(id+"F0.wireOp",EDGE,"E2")])]}),makeQuery(id+"F17.opExtrude","SWEPT_FACE",FACE,{"disambiguationData":[OSD([sQuery(id+"F16.wireOp",EDGE,"E8.45.0")])]})]});
            var Q91;
            Q91=makeQuery(id+"F17.boolean.opBoolean","INTERSECT",EDGE,{"derivedFrom":[makeQuery(id+"F14.opFillet","BLEND_FACE",FACE,{"disambiguationData":[OSD([sQuery(id+"F0.wireOp",EDGE,"E1"),sQuery(id+"F0.wireOp",EDGE,"E2")])]}),makeQuery(id+"F17.opExtrude","SWEPT_FACE",FACE,{"disambiguationData":[OSD([sQuery(id+"F16.wireOp",EDGE,"E8.45.1")])]})]});
            var Q92;
            Q92=makeQuery(id+"F17.opExtrude","CAP_EDGE",EDGE,{"disambiguationData":[OSD([sQuery(id+"F16.wireOp",EDGE,"E8.8.0")])],"isStart":false});
            var Q93;
            Q93=makeQuery(id+"F17.opExtrude","CAP_EDGE",EDGE,{"disambiguationData":[OSD([sQuery(id+"F16.wireOp",EDGE,"E8.9.0")])],"isStart":false});
            var Q94;
            Q94=makeQuery(id+"F17.opExtrude","CAP_EDGE",EDGE,{"disambiguationData":[OSD([sQuery(id+"F16.wireOp",EDGE,"E8.10.0")])],"isStart":false});
            var Q95;
            Q95=makeQuery(id+"F17.opExtrude","CAP_EDGE",EDGE,{"disambiguationData":[OSD([sQuery(id+"F16.wireOp",EDGE,"E8.11.0")])],"isStart":false});
            var Q96;
            Q96=makeQuery(id+"F17.opExtrude","CAP_EDGE",EDGE,{"disambiguationData":[OSD([sQuery(id+"F16.wireOp",EDGE,"E8.12.0")])],"isStart":false});
            var Q97;
            Q97=makeQuery(id+"F17.opExtrude","CAP_EDGE",EDGE,{"disambiguationData":[OSD([sQuery(id+"F16.wireOp",EDGE,"E8.13.0")])],"isStart":false});
            var Q98;
            Q98=makeQuery(id+"F17.opExtrude","CAP_EDGE",EDGE,{"disambiguationData":[OSD([sQuery(id+"F16.wireOp",EDGE,"E8.14.0")])],"isStart":false});
            var Q99;
            Q99=makeQuery(id+"F17.opExtrude","CAP_EDGE",EDGE,{"disambiguationData":[OSD([sQuery(id+"F16.wireOp",EDGE,"E8.7.0")])],"isStart":false});
            var Q100;
            Q100=makeQuery(id+"F17.opExtrude","CAP_EDGE",EDGE,{"disambiguationData":[OSD([sQuery(id+"F16.wireOp",EDGE,"E8.6.0")])],"isStart":false});
            var Q101;
            Q101=makeQuery(id+"F17.opExtrude","CAP_EDGE",EDGE,{"disambiguationData":[OSD([sQuery(id+"F16.wireOp",EDGE,"E8.5.0")])],"isStart":false});
            var Q102;
            Q102=makeQuery(id+"F17.opExtrude","CAP_EDGE",EDGE,{"disambiguationData":[OSD([sQuery(id+"F16.wireOp",EDGE,"E8.4.0")])],"isStart":false});
            var Q103;
            Q103=makeQuery(id+"F17.opExtrude","CAP_EDGE",EDGE,{"disambiguationData":[OSD([sQuery(id+"F16.wireOp",EDGE,"E8.3.0")])],"isStart":false});
            var Q104;
            Q104=makeQuery(id+"F17.opExtrude","CAP_EDGE",EDGE,{"disambiguationData":[OSD([sQuery(id+"F16.wireOp",EDGE,"E8.2.0")])],"isStart":false});
            var Q105;
            Q105=makeQuery(id+"F17.opExtrude","CAP_EDGE",EDGE,{"disambiguationData":[OSD([sQuery(id+"F16.wireOp",EDGE,"E8.1.0")])],"isStart":false});
            var Q106;
            Q106=makeQuery(id+"F17.opExtrude","CAP_EDGE",EDGE,{"disambiguationData":[OSD([sQuery(id+"F16.wireOp",EDGE,"E8.24.0")])],"isStart":false});
            var Q107;
            Q107=makeQuery(id+"F17.opExtrude","CAP_EDGE",EDGE,{"disambiguationData":[OSD([sQuery(id+"F16.wireOp",EDGE,"E8.25.0")])],"isStart":false});
            var Q108;
            Q108=makeQuery(id+"F17.opExtrude","CAP_EDGE",EDGE,{"disambiguationData":[OSD([sQuery(id+"F16.wireOp",EDGE,"E8.26.0")])],"isStart":false});
            var Q109;
            Q109=makeQuery(id+"F17.opExtrude","CAP_EDGE",EDGE,{"disambiguationData":[OSD([sQuery(id+"F16.wireOp",EDGE,"E8.27.0")])],"isStart":false});
            var Q110;
            Q110=makeQuery(id+"F17.opExtrude","CAP_EDGE",EDGE,{"disambiguationData":[OSD([sQuery(id+"F16.wireOp",EDGE,"E8.28.0")])],"isStart":false});
            var Q111;
            Q111=makeQuery(id+"F17.opExtrude","CAP_EDGE",EDGE,{"disambiguationData":[OSD([sQuery(id+"F16.wireOp",EDGE,"E8.29.0")])],"isStart":false});
            var Q112;
            Q112=makeQuery(id+"F17.opExtrude","CAP_EDGE",EDGE,{"disambiguationData":[OSD([sQuery(id+"F16.wireOp",EDGE,"E8.30.0")])],"isStart":false});
            var Q113;
            Q113=makeQuery(id+"F17.opExtrude","CAP_EDGE",EDGE,{"disambiguationData":[OSD([sQuery(id+"F16.wireOp",EDGE,"E8.31.0")])],"isStart":false});
            var Q114;
            Q114=makeQuery(id+"F17.opExtrude","CAP_EDGE",EDGE,{"disambiguationData":[OSD([sQuery(id+"F16.wireOp",EDGE,"E8.32.0")])],"isStart":false});
            var Q115;
            Q115=makeQuery(id+"F17.opExtrude","CAP_EDGE",EDGE,{"disambiguationData":[OSD([sQuery(id+"F16.wireOp",EDGE,"E8.33.0")])],"isStart":false});
            var Q116;
            Q116=makeQuery(id+"F17.opExtrude","CAP_EDGE",EDGE,{"disambiguationData":[OSD([sQuery(id+"F16.wireOp",EDGE,"E8.34.0")])],"isStart":false});
            var Q117;
            Q117=makeQuery(id+"F17.opExtrude","CAP_EDGE",EDGE,{"disambiguationData":[OSD([sQuery(id+"F16.wireOp",EDGE,"E8.35.0")])],"isStart":false});
            var Q118;
            Q118=makeQuery(id+"F17.opExtrude","CAP_EDGE",EDGE,{"disambiguationData":[OSD([sQuery(id+"F16.wireOp",EDGE,"E8.36.0")])],"isStart":false});
            var Q119;
            Q119=makeQuery(id+"F17.opExtrude","CAP_EDGE",EDGE,{"disambiguationData":[OSD([sQuery(id+"F16.wireOp",EDGE,"E8.37.0")])],"isStart":false});
            var Q120;
            Q120=makeQuery(id+"F17.opExtrude","CAP_EDGE",EDGE,{"disambiguationData":[OSD([sQuery(id+"F16.wireOp",EDGE,"E8.38.0")])],"isStart":false});
            var Q121;
            Q121=makeQuery(id+"F17.opExtrude","CAP_EDGE",EDGE,{"disambiguationData":[OSD([sQuery(id+"F16.wireOp",EDGE,"E8.39.0")])],"isStart":false});
            var Q122;
            Q122=makeQuery(id+"F17.opExtrude","CAP_EDGE",EDGE,{"disambiguationData":[OSD([sQuery(id+"F16.wireOp",EDGE,"E8.40.0")])],"isStart":false});
            var Q123;
            Q123=makeQuery(id+"F17.opExtrude","CAP_EDGE",EDGE,{"disambiguationData":[OSD([sQuery(id+"F16.wireOp",EDGE,"E8.41.0")])],"isStart":false});
            var Q124;
            Q124=makeQuery(id+"F17.opExtrude","CAP_EDGE",EDGE,{"disambiguationData":[OSD([sQuery(id+"F16.wireOp",EDGE,"E8.42.0")])],"isStart":false});
            var Q125;
            Q125=makeQuery(id+"F17.opExtrude","CAP_EDGE",EDGE,{"disambiguationData":[OSD([sQuery(id+"F16.wireOp",EDGE,"E8.43.0")])],"isStart":false});
            var Q126;
            Q126=makeQuery(id+"F17.opExtrude","CAP_EDGE",EDGE,{"disambiguationData":[OSD([sQuery(id+"F16.wireOp",EDGE,"E8.44.0")])],"isStart":false});
            var Q127;
            Q127=makeQuery(id+"F17.opExtrude","CAP_EDGE",EDGE,{"disambiguationData":[OSD([sQuery(id+"F16.wireOp",EDGE,"E8.45.0")])],"isStart":false});
            var Q128;
            Q128=makeQuery(id+"F17.opExtrude","CAP_EDGE",EDGE,{"disambiguationData":[OSD([sQuery(id+"F16.wireOp",EDGE,"E7.MirrorCS")])],"isStart":false});
            var Q129;
            Q129=makeQuery(id+"F17.opExtrude","CAP_EDGE",EDGE,{"disambiguationData":[OSD([sQuery(id+"F16.wireOp",EDGE,"E8.1.1")])],"isStart":false});
            var Q130;
            Q130=makeQuery(id+"F17.opExtrude","CAP_EDGE",EDGE,{"disambiguationData":[OSD([sQuery(id+"F16.wireOp",EDGE,"E6.MirrorCS")])],"isStart":false});
            var Q131;
            Q131=makeQuery(id+"F17.opExtrude","CAP_EDGE",EDGE,{"disambiguationData":[OSD([sQuery(id+"F16.wireOp",EDGE,"E8.45.1")])],"isStart":false});
            var Q132;
            Q132=makeQuery(id+"F17.opExtrude","CAP_EDGE",EDGE,{"disambiguationData":[OSD([sQuery(id+"F16.wireOp",EDGE,"E8.28.1")])],"isStart":false});
            var Q133;
            Q133=makeQuery(id+"F17.opExtrude","CAP_EDGE",EDGE,{"disambiguationData":[OSD([sQuery(id+"F16.wireOp",EDGE,"E8.5.1")])],"isStart":false});
            var Q134;
            Q134=makeQuery(id+"F17.opExtrude","CAP_EDGE",EDGE,{"disambiguationData":[OSD([sQuery(id+"F16.wireOp",EDGE,"E8.42.1")])],"isStart":false});
            var Q135;
            Q135=makeQuery(id+"F17.opExtrude","CAP_EDGE",EDGE,{"disambiguationData":[OSD([sQuery(id+"F16.wireOp",EDGE,"E8.29.1")])],"isStart":false});
            var Q136;
            Q136=makeQuery(id+"F17.opExtrude","CAP_EDGE",EDGE,{"disambiguationData":[OSD([sQuery(id+"F16.wireOp",EDGE,"E8.4.1")])],"isStart":false});
            var Q137;
            Q137=makeQuery(id+"F17.opExtrude","CAP_EDGE",EDGE,{"disambiguationData":[OSD([sQuery(id+"F16.wireOp",EDGE,"E8.7.1")])],"isStart":false});
            var Q138;
            Q138=makeQuery(id+"F17.opExtrude","CAP_EDGE",EDGE,{"disambiguationData":[OSD([sQuery(id+"F16.wireOp",EDGE,"E8.3.1")])],"isStart":false});
            var Q139;
            Q139=makeQuery(id+"F17.opExtrude","CAP_EDGE",EDGE,{"disambiguationData":[OSD([sQuery(id+"F16.wireOp",EDGE,"E8.33.1")])],"isStart":false});
            var Q140;
            Q140=makeQuery(id+"F17.opExtrude","CAP_EDGE",EDGE,{"disambiguationData":[OSD([sQuery(id+"F16.wireOp",EDGE,"E8.27.1")])],"isStart":false});
            var Q141;
            Q141=makeQuery(id+"F17.opExtrude","CAP_EDGE",EDGE,{"disambiguationData":[OSD([sQuery(id+"F16.wireOp",EDGE,"E8.35.1")])],"isStart":false});
            var Q142;
            Q142=makeQuery(id+"F17.opExtrude","CAP_EDGE",EDGE,{"disambiguationData":[OSD([sQuery(id+"F16.wireOp",EDGE,"E8.43.1")])],"isStart":false});
            var Q143;
            Q143=makeQuery(id+"F17.opExtrude","CAP_EDGE",EDGE,{"disambiguationData":[OSD([sQuery(id+"F16.wireOp",EDGE,"E8.2.1")])],"isStart":false});
            var Q144;
            {var subQ0=sQuery(id+"F16.wireOp",EDGE,"E8.28.1");var subQ1=sQuery(id+"F16.wireOp",EDGE,"E8.28.0");Q144=makeQuery(id+"F17.opExtrude","SWEPT_EDGE",EDGE,{"disambiguationData":[OSD([subQ1,subQ0]),TDD([makeQuery(id+"F16.imprint","INTERSECT",VERTEX,{"disambiguationData":[OD(1.0)],"derivedFrom":[subQ1,subQ0]})])]});}
            var Q145;
            Q145=makeQuery(id+"F17.opExtrude","CAP_EDGE",EDGE,{"disambiguationData":[OSD([sQuery(id+"F16.wireOp",EDGE,"E8.37.1")])],"isStart":false});
            var Q146;
            Q146=makeQuery(id+"F17.opExtrude","CAP_EDGE",EDGE,{"disambiguationData":[OSD([sQuery(id+"F16.wireOp",EDGE,"E8.32.1")])],"isStart":false});
            var Q147;
            {var subQ0=sQuery(id+"F16.wireOp",EDGE,"E8.36.1");var subQ1=sQuery(id+"F16.wireOp",EDGE,"E8.36.0");Q147=makeQuery(id+"F17.opExtrude","SWEPT_EDGE",EDGE,{"disambiguationData":[OSD([subQ1,subQ0]),TDD([makeQuery(id+"F16.imprint","INTERSECT",VERTEX,{"disambiguationData":[OD(1.0)],"derivedFrom":[subQ1,subQ0]})])]});}
            var Q148;
            {var subQ0=sQuery(id+"F16.wireOp",EDGE,"E8.42.1");var subQ1=sQuery(id+"F16.wireOp",EDGE,"E8.42.0");Q148=makeQuery(id+"F17.opExtrude","SWEPT_EDGE",EDGE,{"disambiguationData":[OSD([subQ1,subQ0]),TDD([makeQuery(id+"F16.imprint","INTERSECT",VERTEX,{"disambiguationData":[OD(1.0)],"derivedFrom":[subQ1,subQ0]})])]});}
            var Q149;
            {var subQ0=sQuery(id+"F16.wireOp",EDGE,"E8.37.1");var subQ1=sQuery(id+"F16.wireOp",EDGE,"E8.37.0");Q149=makeQuery(id+"F17.opExtrude","SWEPT_EDGE",EDGE,{"disambiguationData":[OSD([subQ1,subQ0]),TDD([makeQuery(id+"F16.imprint","INTERSECT",VERTEX,{"disambiguationData":[OD(1.0)],"derivedFrom":[subQ1,subQ0]})])]});}
            var Q150;
            Q150=makeQuery(id+"F17.opExtrude","CAP_EDGE",EDGE,{"disambiguationData":[OSD([sQuery(id+"F16.wireOp",EDGE,"E8.41.1")])],"isStart":false});
            var Q151;
            {var subQ0=sQuery(id+"F16.wireOp",EDGE,"E8.3.1");var subQ1=sQuery(id+"F16.wireOp",EDGE,"E8.3.0");Q151=makeQuery(id+"F17.opExtrude","SWEPT_EDGE",EDGE,{"disambiguationData":[OSD([subQ1,subQ0]),TDD([makeQuery(id+"F16.imprint","INTERSECT",VERTEX,{"disambiguationData":[OD(0.0)],"derivedFrom":[subQ1,subQ0]})])]});}
            var Q152;
            Q152=makeQuery(id+"F17.opExtrude","CAP_EDGE",EDGE,{"disambiguationData":[OSD([sQuery(id+"F16.wireOp",EDGE,"E8.31.1")])],"isStart":false});
            var Q153;
            Q153=makeQuery(id+"F17.opExtrude","CAP_EDGE",EDGE,{"disambiguationData":[OSD([sQuery(id+"F16.wireOp",EDGE,"E8.44.1")])],"isStart":false});
            var Q154;
            {var subQ0=sQuery(id+"F16.wireOp",EDGE,"E8.35.1");var subQ1=sQuery(id+"F16.wireOp",EDGE,"E8.35.0");Q154=makeQuery(id+"F17.opExtrude","SWEPT_EDGE",EDGE,{"disambiguationData":[OSD([subQ1,subQ0]),TDD([makeQuery(id+"F16.imprint","INTERSECT",VERTEX,{"disambiguationData":[OD(0.0)],"derivedFrom":[subQ1,subQ0]})])]});}
            var Q155;
            Q155=makeQuery(id+"F17.opExtrude","CAP_EDGE",EDGE,{"disambiguationData":[OSD([sQuery(id+"F16.wireOp",EDGE,"E8.38.1")])],"isStart":false});
            var Q156;
            {var subQ0=sQuery(id+"F16.wireOp",EDGE,"E8.30.1");var subQ1=sQuery(id+"F16.wireOp",EDGE,"E8.30.0");Q156=makeQuery(id+"F17.opExtrude","SWEPT_EDGE",EDGE,{"disambiguationData":[OSD([subQ1,subQ0]),TDD([makeQuery(id+"F16.imprint","INTERSECT",VERTEX,{"disambiguationData":[OD(0.0)],"derivedFrom":[subQ1,subQ0]})])]});}
            var Q157;
            {var subQ0=sQuery(id+"F16.wireOp",EDGE,"E8.37.1");var subQ1=sQuery(id+"F16.wireOp",EDGE,"E8.37.0");Q157=makeQuery(id+"F17.opExtrude","SWEPT_EDGE",EDGE,{"disambiguationData":[OSD([subQ1,subQ0]),TDD([makeQuery(id+"F16.imprint","INTERSECT",VERTEX,{"disambiguationData":[OD(0.0)],"derivedFrom":[subQ1,subQ0]})])]});}
            var Q158;
            {var subQ0=sQuery(id+"F16.wireOp",EDGE,"E8.2.1");var subQ1=sQuery(id+"F16.wireOp",EDGE,"E8.2.0");Q158=makeQuery(id+"F17.opExtrude","SWEPT_EDGE",EDGE,{"disambiguationData":[OSD([subQ1,subQ0]),TDD([makeQuery(id+"F16.imprint","INTERSECT",VERTEX,{"disambiguationData":[OD(1.0)],"derivedFrom":[subQ1,subQ0]})])]});}
            var Q159;
            Q159=makeQuery(id+"F17.opExtrude","CAP_EDGE",EDGE,{"disambiguationData":[OSD([sQuery(id+"F16.wireOp",EDGE,"E8.6.1")])],"isStart":false});
            var Q160;
            {var subQ0=sQuery(id+"F16.wireOp",EDGE,"E8.35.1");var subQ1=sQuery(id+"F16.wireOp",EDGE,"E8.35.0");Q160=makeQuery(id+"F17.opExtrude","SWEPT_EDGE",EDGE,{"disambiguationData":[OSD([subQ1,subQ0]),TDD([makeQuery(id+"F16.imprint","INTERSECT",VERTEX,{"disambiguationData":[OD(1.0)],"derivedFrom":[subQ1,subQ0]})])]});}
            var Q161;
            {var subQ0=sQuery(id+"F16.wireOp",EDGE,"E8.41.1");var subQ1=sQuery(id+"F16.wireOp",EDGE,"E8.41.0");Q161=makeQuery(id+"F17.opExtrude","SWEPT_EDGE",EDGE,{"disambiguationData":[OSD([subQ1,subQ0]),TDD([makeQuery(id+"F16.imprint","INTERSECT",VERTEX,{"disambiguationData":[OD(1.0)],"derivedFrom":[subQ1,subQ0]})])]});}
            var Q162;
            {var subQ0=sQuery(id+"F16.wireOp",EDGE,"E8.44.1");var subQ1=sQuery(id+"F16.wireOp",EDGE,"E8.44.0");Q162=makeQuery(id+"F17.opExtrude","SWEPT_EDGE",EDGE,{"disambiguationData":[OSD([subQ1,subQ0]),TDD([makeQuery(id+"F16.imprint","INTERSECT",VERTEX,{"disambiguationData":[OD(0.0)],"derivedFrom":[subQ1,subQ0]})])]});}
            var Q163;
            {var subQ0=sQuery(id+"F16.wireOp",EDGE,"E8.43.1");var subQ1=sQuery(id+"F16.wireOp",EDGE,"E8.43.0");Q163=makeQuery(id+"F17.opExtrude","SWEPT_EDGE",EDGE,{"disambiguationData":[OSD([subQ1,subQ0]),TDD([makeQuery(id+"F16.imprint","INTERSECT",VERTEX,{"disambiguationData":[OD(0.0)],"derivedFrom":[subQ1,subQ0]})])]});}
            var Q164;
            {var subQ0=sQuery(id+"F16.wireOp",EDGE,"E8.4.1");var subQ1=sQuery(id+"F16.wireOp",EDGE,"E8.4.0");Q164=makeQuery(id+"F17.opExtrude","SWEPT_EDGE",EDGE,{"disambiguationData":[OSD([subQ1,subQ0]),TDD([makeQuery(id+"F16.imprint","INTERSECT",VERTEX,{"disambiguationData":[OD(0.0)],"derivedFrom":[subQ1,subQ0]})])]});}
            var Q165;
            {var subQ0=sQuery(id+"F16.wireOp",EDGE,"E8.43.1");var subQ1=sQuery(id+"F16.wireOp",EDGE,"E8.43.0");Q165=makeQuery(id+"F17.opExtrude","SWEPT_EDGE",EDGE,{"disambiguationData":[OSD([subQ1,subQ0]),TDD([makeQuery(id+"F16.imprint","INTERSECT",VERTEX,{"disambiguationData":[OD(1.0)],"derivedFrom":[subQ1,subQ0]})])]});}
            var Q166;
            {var subQ0=sQuery(id+"F16.wireOp",EDGE,"E8.41.1");var subQ1=sQuery(id+"F16.wireOp",EDGE,"E8.41.0");Q166=makeQuery(id+"F17.opExtrude","SWEPT_EDGE",EDGE,{"disambiguationData":[OSD([subQ1,subQ0]),TDD([makeQuery(id+"F16.imprint","INTERSECT",VERTEX,{"disambiguationData":[OD(0.0)],"derivedFrom":[subQ1,subQ0]})])]});}
            var Q167;
            {var subQ0=sQuery(id+"F16.wireOp",EDGE,"E8.42.1");var subQ1=sQuery(id+"F16.wireOp",EDGE,"E8.42.0");Q167=makeQuery(id+"F17.opExtrude","SWEPT_EDGE",EDGE,{"disambiguationData":[OSD([subQ1,subQ0]),TDD([makeQuery(id+"F16.imprint","INTERSECT",VERTEX,{"disambiguationData":[OD(0.0)],"derivedFrom":[subQ1,subQ0]})])]});}
            var Q168;
            {var subQ0=sQuery(id+"F16.wireOp",EDGE,"E8.6.1");var subQ1=sQuery(id+"F16.wireOp",EDGE,"E8.6.0");Q168=makeQuery(id+"F17.opExtrude","SWEPT_EDGE",EDGE,{"disambiguationData":[OSD([subQ1,subQ0]),TDD([makeQuery(id+"F16.imprint","INTERSECT",VERTEX,{"disambiguationData":[OD(1.0)],"derivedFrom":[subQ1,subQ0]})])]});}
            var Q169;
            Q169=makeQuery(id+"F17.opExtrude","CAP_EDGE",EDGE,{"disambiguationData":[OSD([sQuery(id+"F16.wireOp",EDGE,"E8.39.1")])],"isStart":false});
            var Q170;
            {var subQ0=sQuery(id+"F16.wireOp",EDGE,"E8.39.1");var subQ1=sQuery(id+"F16.wireOp",EDGE,"E8.39.0");Q170=makeQuery(id+"F17.opExtrude","SWEPT_EDGE",EDGE,{"disambiguationData":[OSD([subQ1,subQ0]),TDD([makeQuery(id+"F16.imprint","INTERSECT",VERTEX,{"disambiguationData":[OD(1.0)],"derivedFrom":[subQ1,subQ0]})])]});}
            var Q171;
            {var subQ0=sQuery(id+"F16.wireOp",EDGE,"E8.3.1");var subQ1=sQuery(id+"F16.wireOp",EDGE,"E8.3.0");Q171=makeQuery(id+"F17.opExtrude","SWEPT_EDGE",EDGE,{"disambiguationData":[OSD([subQ1,subQ0]),TDD([makeQuery(id+"F16.imprint","INTERSECT",VERTEX,{"disambiguationData":[OD(1.0)],"derivedFrom":[subQ1,subQ0]})])]});}
            var Q172;
            Q172=makeQuery(id+"F17.opExtrude","CAP_EDGE",EDGE,{"disambiguationData":[OSD([sQuery(id+"F16.wireOp",EDGE,"E8.36.1")])],"isStart":false});
            var Q173;
            Q173=makeQuery(id+"F17.opExtrude","CAP_EDGE",EDGE,{"disambiguationData":[OSD([sQuery(id+"F16.wireOp",EDGE,"E8.34.1")])],"isStart":false});
            var Q174;
            {var subQ0=sQuery(id+"F16.wireOp",EDGE,"E8.40.1");var subQ1=sQuery(id+"F16.wireOp",EDGE,"E8.40.0");Q174=makeQuery(id+"F17.opExtrude","SWEPT_EDGE",EDGE,{"disambiguationData":[OSD([subQ1,subQ0]),TDD([makeQuery(id+"F16.imprint","INTERSECT",VERTEX,{"disambiguationData":[OD(1.0)],"derivedFrom":[subQ1,subQ0]})])]});}
            var Q175;
            Q175=makeQuery(id+"F17.opExtrude","CAP_EDGE",EDGE,{"disambiguationData":[OSD([sQuery(id+"F16.wireOp",EDGE,"E8.30.1")])],"isStart":false});
            var Q176;
            {var subQ0=sQuery(id+"F16.wireOp",EDGE,"E7.MirrorCS");var subQ1=sQuery(id+"F16.wireOp",EDGE,"E6.MirrorCS");Q176=makeQuery(id+"F17.opExtrude","SWEPT_EDGE",EDGE,{"disambiguationData":[OSD([subQ1,subQ0]),TDD([makeQuery(id+"F16.imprint","INTERSECT",VERTEX,{"disambiguationData":[OD(0.0)],"derivedFrom":[subQ1,subQ0]})])]});}
            var Q177;
            {var subQ0=sQuery(id+"F16.wireOp",EDGE,"E8.34.1");var subQ1=sQuery(id+"F16.wireOp",EDGE,"E8.34.0");Q177=makeQuery(id+"F17.opExtrude","SWEPT_EDGE",EDGE,{"disambiguationData":[OSD([subQ1,subQ0]),TDD([makeQuery(id+"F16.imprint","INTERSECT",VERTEX,{"disambiguationData":[OD(1.0)],"derivedFrom":[subQ1,subQ0]})])]});}
            var Q178;
            {var subQ0=sQuery(id+"F16.wireOp",EDGE,"E8.45.1");var subQ1=sQuery(id+"F16.wireOp",EDGE,"E8.45.0");Q178=makeQuery(id+"F17.opExtrude","SWEPT_EDGE",EDGE,{"disambiguationData":[OSD([subQ1,subQ0]),TDD([makeQuery(id+"F16.imprint","INTERSECT",VERTEX,{"disambiguationData":[OD(1.0)],"derivedFrom":[subQ1,subQ0]})])]});}
            var Q179;
            {var subQ0=sQuery(id+"F16.wireOp",EDGE,"E8.33.1");var subQ1=sQuery(id+"F16.wireOp",EDGE,"E8.33.0");Q179=makeQuery(id+"F17.opExtrude","SWEPT_EDGE",EDGE,{"disambiguationData":[OSD([subQ1,subQ0]),TDD([makeQuery(id+"F16.imprint","INTERSECT",VERTEX,{"disambiguationData":[OD(1.0)],"derivedFrom":[subQ1,subQ0]})])]});}
            var Q180;
            {var subQ0=sQuery(id+"F16.wireOp",EDGE,"E8.39.1");var subQ1=sQuery(id+"F16.wireOp",EDGE,"E8.39.0");Q180=makeQuery(id+"F17.opExtrude","SWEPT_EDGE",EDGE,{"disambiguationData":[OSD([subQ1,subQ0]),TDD([makeQuery(id+"F16.imprint","INTERSECT",VERTEX,{"disambiguationData":[OD(0.0)],"derivedFrom":[subQ1,subQ0]})])]});}
            var Q181;
            {var subQ0=sQuery(id+"F16.wireOp",EDGE,"E8.45.1");var subQ1=sQuery(id+"F16.wireOp",EDGE,"E8.45.0");Q181=makeQuery(id+"F17.opExtrude","SWEPT_EDGE",EDGE,{"disambiguationData":[OSD([subQ1,subQ0]),TDD([makeQuery(id+"F16.imprint","INTERSECT",VERTEX,{"disambiguationData":[OD(0.0)],"derivedFrom":[subQ1,subQ0]})])]});}
            var Q182;
            {var subQ0=sQuery(id+"F16.wireOp",EDGE,"E8.1.1");var subQ1=sQuery(id+"F16.wireOp",EDGE,"E8.1.0");Q182=makeQuery(id+"F17.opExtrude","SWEPT_EDGE",EDGE,{"disambiguationData":[OSD([subQ1,subQ0]),TDD([makeQuery(id+"F16.imprint","INTERSECT",VERTEX,{"disambiguationData":[OD(0.0)],"derivedFrom":[subQ1,subQ0]})])]});}
            var Q183;
            {var subQ0=sQuery(id+"F16.wireOp",EDGE,"E7.MirrorCS");var subQ1=sQuery(id+"F16.wireOp",EDGE,"E6.MirrorCS");Q183=makeQuery(id+"F17.opExtrude","SWEPT_EDGE",EDGE,{"disambiguationData":[OSD([subQ1,subQ0]),TDD([makeQuery(id+"F16.imprint","INTERSECT",VERTEX,{"disambiguationData":[OD(1.0)],"derivedFrom":[subQ1,subQ0]})])]});}
            var Q184;
            {var subQ0=sQuery(id+"F16.wireOp",EDGE,"E8.44.1");var subQ1=sQuery(id+"F16.wireOp",EDGE,"E8.44.0");Q184=makeQuery(id+"F17.opExtrude","SWEPT_EDGE",EDGE,{"disambiguationData":[OSD([subQ1,subQ0]),TDD([makeQuery(id+"F16.imprint","INTERSECT",VERTEX,{"disambiguationData":[OD(1.0)],"derivedFrom":[subQ1,subQ0]})])]});}
            var Q185;
            {var subQ0=sQuery(id+"F16.wireOp",EDGE,"E8.33.1");var subQ1=sQuery(id+"F16.wireOp",EDGE,"E8.33.0");Q185=makeQuery(id+"F17.opExtrude","SWEPT_EDGE",EDGE,{"disambiguationData":[OSD([subQ1,subQ0]),TDD([makeQuery(id+"F16.imprint","INTERSECT",VERTEX,{"disambiguationData":[OD(0.0)],"derivedFrom":[subQ1,subQ0]})])]});}
            var Q186;
            {var subQ0=sQuery(id+"F16.wireOp",EDGE,"E8.31.1");var subQ1=sQuery(id+"F16.wireOp",EDGE,"E8.31.0");Q186=makeQuery(id+"F17.opExtrude","SWEPT_EDGE",EDGE,{"disambiguationData":[OSD([subQ1,subQ0]),TDD([makeQuery(id+"F16.imprint","INTERSECT",VERTEX,{"disambiguationData":[OD(0.0)],"derivedFrom":[subQ1,subQ0]})])]});}
            var Q187;
            {var subQ0=sQuery(id+"F16.wireOp",EDGE,"E8.38.1");var subQ1=sQuery(id+"F16.wireOp",EDGE,"E8.38.0");Q187=makeQuery(id+"F17.opExtrude","SWEPT_EDGE",EDGE,{"disambiguationData":[OSD([subQ1,subQ0]),TDD([makeQuery(id+"F16.imprint","INTERSECT",VERTEX,{"disambiguationData":[OD(1.0)],"derivedFrom":[subQ1,subQ0]})])]});}
            var Q188;
            {var subQ0=sQuery(id+"F16.wireOp",EDGE,"E8.5.1");var subQ1=sQuery(id+"F16.wireOp",EDGE,"E8.5.0");Q188=makeQuery(id+"F17.opExtrude","SWEPT_EDGE",EDGE,{"disambiguationData":[OSD([subQ1,subQ0]),TDD([makeQuery(id+"F16.imprint","INTERSECT",VERTEX,{"disambiguationData":[OD(0.0)],"derivedFrom":[subQ1,subQ0]})])]});}
            var Q189;
            {var subQ0=sQuery(id+"F16.wireOp",EDGE,"E8.38.1");var subQ1=sQuery(id+"F16.wireOp",EDGE,"E8.38.0");Q189=makeQuery(id+"F17.opExtrude","SWEPT_EDGE",EDGE,{"disambiguationData":[OSD([subQ1,subQ0]),TDD([makeQuery(id+"F16.imprint","INTERSECT",VERTEX,{"disambiguationData":[OD(0.0)],"derivedFrom":[subQ1,subQ0]})])]});}
            var Q190;
            {var subQ0=sQuery(id+"F16.wireOp",EDGE,"E8.32.1");var subQ1=sQuery(id+"F16.wireOp",EDGE,"E8.32.0");Q190=makeQuery(id+"F17.opExtrude","SWEPT_EDGE",EDGE,{"disambiguationData":[OSD([subQ1,subQ0]),TDD([makeQuery(id+"F16.imprint","INTERSECT",VERTEX,{"disambiguationData":[OD(0.0)],"derivedFrom":[subQ1,subQ0]})])]});}
            var Q191;
            {var subQ0=sQuery(id+"F16.wireOp",EDGE,"E8.5.1");var subQ1=sQuery(id+"F16.wireOp",EDGE,"E8.5.0");Q191=makeQuery(id+"F17.opExtrude","SWEPT_EDGE",EDGE,{"disambiguationData":[OSD([subQ1,subQ0]),TDD([makeQuery(id+"F16.imprint","INTERSECT",VERTEX,{"disambiguationData":[OD(1.0)],"derivedFrom":[subQ1,subQ0]})])]});}
            var Q192;
            {var subQ0=sQuery(id+"F16.wireOp",EDGE,"E8.40.1");var subQ1=sQuery(id+"F16.wireOp",EDGE,"E8.40.0");Q192=makeQuery(id+"F17.opExtrude","SWEPT_EDGE",EDGE,{"disambiguationData":[OSD([subQ1,subQ0]),TDD([makeQuery(id+"F16.imprint","INTERSECT",VERTEX,{"disambiguationData":[OD(0.0)],"derivedFrom":[subQ1,subQ0]})])]});}
            var Q193;
            {var subQ0=sQuery(id+"F16.wireOp",EDGE,"E8.29.1");var subQ1=sQuery(id+"F16.wireOp",EDGE,"E8.29.0");Q193=makeQuery(id+"F17.opExtrude","SWEPT_EDGE",EDGE,{"disambiguationData":[OSD([subQ1,subQ0]),TDD([makeQuery(id+"F16.imprint","INTERSECT",VERTEX,{"disambiguationData":[OD(0.0)],"derivedFrom":[subQ1,subQ0]})])]});}
            var Q194;
            {var subQ0=sQuery(id+"F16.wireOp",EDGE,"E8.36.1");var subQ1=sQuery(id+"F16.wireOp",EDGE,"E8.36.0");Q194=makeQuery(id+"F17.opExtrude","SWEPT_EDGE",EDGE,{"disambiguationData":[OSD([subQ1,subQ0]),TDD([makeQuery(id+"F16.imprint","INTERSECT",VERTEX,{"disambiguationData":[OD(0.0)],"derivedFrom":[subQ1,subQ0]})])]});}
            var Q195;
            {var subQ0=sQuery(id+"F16.wireOp",EDGE,"E8.4.1");var subQ1=sQuery(id+"F16.wireOp",EDGE,"E8.4.0");Q195=makeQuery(id+"F17.opExtrude","SWEPT_EDGE",EDGE,{"disambiguationData":[OSD([subQ1,subQ0]),TDD([makeQuery(id+"F16.imprint","INTERSECT",VERTEX,{"disambiguationData":[OD(1.0)],"derivedFrom":[subQ1,subQ0]})])]});}
            var Q196;
            {var subQ0=sQuery(id+"F16.wireOp",EDGE,"E8.29.1");var subQ1=sQuery(id+"F16.wireOp",EDGE,"E8.29.0");Q196=makeQuery(id+"F17.opExtrude","SWEPT_EDGE",EDGE,{"disambiguationData":[OSD([subQ1,subQ0]),TDD([makeQuery(id+"F16.imprint","INTERSECT",VERTEX,{"disambiguationData":[OD(1.0)],"derivedFrom":[subQ1,subQ0]})])]});}
            var Q197;
            Q197=makeQuery(id+"F17.opExtrude","CAP_EDGE",EDGE,{"disambiguationData":[OSD([sQuery(id+"F16.wireOp",EDGE,"E8.40.1")])],"isStart":false});
            var Q198;
            {var subQ0=sQuery(id+"F16.wireOp",EDGE,"E8.32.1");var subQ1=sQuery(id+"F16.wireOp",EDGE,"E8.32.0");Q198=makeQuery(id+"F17.opExtrude","SWEPT_EDGE",EDGE,{"disambiguationData":[OSD([subQ1,subQ0]),TDD([makeQuery(id+"F16.imprint","INTERSECT",VERTEX,{"disambiguationData":[OD(1.0)],"derivedFrom":[subQ1,subQ0]})])]});}
            var Q199;
            {var subQ0=sQuery(id+"F16.wireOp",EDGE,"E8.1.1");var subQ1=sQuery(id+"F16.wireOp",EDGE,"E8.1.0");Q199=makeQuery(id+"F17.opExtrude","SWEPT_EDGE",EDGE,{"disambiguationData":[OSD([subQ1,subQ0]),TDD([makeQuery(id+"F16.imprint","INTERSECT",VERTEX,{"disambiguationData":[OD(1.0)],"derivedFrom":[subQ1,subQ0]})])]});}
            var Q200;
            {var subQ0=sQuery(id+"F16.wireOp",EDGE,"E8.30.1");var subQ1=sQuery(id+"F16.wireOp",EDGE,"E8.30.0");Q200=makeQuery(id+"F17.opExtrude","SWEPT_EDGE",EDGE,{"disambiguationData":[OSD([subQ1,subQ0]),TDD([makeQuery(id+"F16.imprint","INTERSECT",VERTEX,{"disambiguationData":[OD(1.0)],"derivedFrom":[subQ1,subQ0]})])]});}
            var Q201;
            {var subQ0=sQuery(id+"F16.wireOp",EDGE,"E8.34.1");var subQ1=sQuery(id+"F16.wireOp",EDGE,"E8.34.0");Q201=makeQuery(id+"F17.opExtrude","SWEPT_EDGE",EDGE,{"disambiguationData":[OSD([subQ1,subQ0]),TDD([makeQuery(id+"F16.imprint","INTERSECT",VERTEX,{"disambiguationData":[OD(0.0)],"derivedFrom":[subQ1,subQ0]})])]});}
            var Q202;
            {var subQ0=sQuery(id+"F16.wireOp",EDGE,"E8.2.1");var subQ1=sQuery(id+"F16.wireOp",EDGE,"E8.2.0");Q202=makeQuery(id+"F17.opExtrude","SWEPT_EDGE",EDGE,{"disambiguationData":[OSD([subQ1,subQ0]),TDD([makeQuery(id+"F16.imprint","INTERSECT",VERTEX,{"disambiguationData":[OD(0.0)],"derivedFrom":[subQ1,subQ0]})])]});}
            var Q203;
            {var subQ0=sQuery(id+"F16.wireOp",EDGE,"E8.31.1");var subQ1=sQuery(id+"F16.wireOp",EDGE,"E8.31.0");Q203=makeQuery(id+"F17.opExtrude","SWEPT_EDGE",EDGE,{"disambiguationData":[OSD([subQ1,subQ0]),TDD([makeQuery(id+"F16.imprint","INTERSECT",VERTEX,{"disambiguationData":[OD(1.0)],"derivedFrom":[subQ1,subQ0]})])]});}
            var Q204;
            Q204=makeQuery(id+"F17.opExtrude","CAP_EDGE",EDGE,{"disambiguationData":[OSD([sQuery(id+"F16.wireOp",EDGE,"E8.16.1")])],"isStart":false});
            var Q205;
            Q205=makeQuery(id+"F17.opExtrude","CAP_EDGE",EDGE,{"disambiguationData":[OSD([sQuery(id+"F16.wireOp",EDGE,"E8.21.1")])],"isStart":false});
            var Q206;
            Q206=makeQuery(id+"F17.opExtrude","CAP_EDGE",EDGE,{"disambiguationData":[OSD([sQuery(id+"F16.wireOp",EDGE,"E8.18.1")])],"isStart":false});
            var Q207;
            Q207=makeQuery(id+"F17.opExtrude","CAP_EDGE",EDGE,{"disambiguationData":[OSD([sQuery(id+"F16.wireOp",EDGE,"E8.22.1")])],"isStart":false});
            var Q208;
            Q208=makeQuery(id+"F17.opExtrude","CAP_EDGE",EDGE,{"disambiguationData":[OSD([sQuery(id+"F16.wireOp",EDGE,"E8.19.0")])],"isStart":false});
            var Q209;
            Q209=makeQuery(id+"F17.opExtrude","CAP_EDGE",EDGE,{"disambiguationData":[OSD([sQuery(id+"F16.wireOp",EDGE,"E8.19.1")])],"isStart":false});
            var Q210;
            Q210=makeQuery(id+"F17.opExtrude","CAP_EDGE",EDGE,{"disambiguationData":[OSD([sQuery(id+"F16.wireOp",EDGE,"E8.23.1")])],"isStart":false});
            var Q211;
            Q211=makeQuery(id+"F17.opExtrude","CAP_EDGE",EDGE,{"disambiguationData":[OSD([sQuery(id+"F16.wireOp",EDGE,"E8.24.1")])],"isStart":false});
            var Q212;
            Q212=makeQuery(id+"F17.opExtrude","CAP_EDGE",EDGE,{"disambiguationData":[OSD([sQuery(id+"F16.wireOp",EDGE,"E8.13.1")])],"isStart":false});
            var Q213;
            Q213=makeQuery(id+"F17.opExtrude","CAP_EDGE",EDGE,{"disambiguationData":[OSD([sQuery(id+"F16.wireOp",EDGE,"E8.11.1")])],"isStart":false});
            var Q214;
            Q214=makeQuery(id+"F17.opExtrude","CAP_EDGE",EDGE,{"disambiguationData":[OSD([sQuery(id+"F16.wireOp",EDGE,"E8.26.1")])],"isStart":false});
            var Q215;
            Q215=makeQuery(id+"F17.opExtrude","CAP_EDGE",EDGE,{"disambiguationData":[OSD([sQuery(id+"F16.wireOp",EDGE,"E8.16.0")])],"isStart":false});
            var Q216;
            Q216=makeQuery(id+"F17.opExtrude","CAP_EDGE",EDGE,{"disambiguationData":[OSD([sQuery(id+"F16.wireOp",EDGE,"E8.20.0")])],"isStart":false});
            var Q217;
            Q217=makeQuery(id+"F17.opExtrude","CAP_EDGE",EDGE,{"disambiguationData":[OSD([sQuery(id+"F16.wireOp",EDGE,"E8.20.1")])],"isStart":false});
            var Q218;
            Q218=makeQuery(id+"F17.opExtrude","CAP_EDGE",EDGE,{"disambiguationData":[OSD([sQuery(id+"F16.wireOp",EDGE,"E8.17.0")])],"isStart":false});
            var Q219;
            Q219=makeQuery(id+"F17.opExtrude","CAP_EDGE",EDGE,{"disambiguationData":[OSD([sQuery(id+"F16.wireOp",EDGE,"E8.21.0")])],"isStart":false});
            var Q220;
            Q220=makeQuery(id+"F17.opExtrude","CAP_EDGE",EDGE,{"disambiguationData":[OSD([sQuery(id+"F16.wireOp",EDGE,"E8.17.1")])],"isStart":false});
            var Q221;
            Q221=makeQuery(id+"F17.opExtrude","CAP_EDGE",EDGE,{"disambiguationData":[OSD([sQuery(id+"F16.wireOp",EDGE,"E8.18.0")])],"isStart":false});
            var Q222;
            Q222=makeQuery(id+"F17.opExtrude","CAP_EDGE",EDGE,{"disambiguationData":[OSD([sQuery(id+"F16.wireOp",EDGE,"E8.22.0")])],"isStart":false});
            var Q223;
            Q223=makeQuery(id+"F17.opExtrude","CAP_EDGE",EDGE,{"disambiguationData":[OSD([sQuery(id+"F16.wireOp",EDGE,"E8.15.0")])],"isStart":false});
            var Q224;
            Q224=makeQuery(id+"F17.opExtrude","CAP_EDGE",EDGE,{"disambiguationData":[OSD([sQuery(id+"F16.wireOp",EDGE,"E8.23.0")])],"isStart":false});
            var Q225;
            {var subQ0=sQuery(id+"F16.wireOp",EDGE,"E8.11.1");var subQ1=sQuery(id+"F16.wireOp",EDGE,"E8.11.0");Q225=makeQuery(id+"F17.opExtrude","SWEPT_EDGE",EDGE,{"disambiguationData":[OSD([subQ1,subQ0]),TDD([makeQuery(id+"F16.imprint","INTERSECT",VERTEX,{"disambiguationData":[OD(0.0)],"derivedFrom":[subQ1,subQ0]})])]});}
            var Q226;
            {var subQ0=sQuery(id+"F16.wireOp",EDGE,"E8.26.1");var subQ1=sQuery(id+"F16.wireOp",EDGE,"E8.26.0");Q226=makeQuery(id+"F17.opExtrude","SWEPT_EDGE",EDGE,{"disambiguationData":[OSD([subQ1,subQ0]),TDD([makeQuery(id+"F16.imprint","INTERSECT",VERTEX,{"disambiguationData":[OD(0.0)],"derivedFrom":[subQ1,subQ0]})])]});}
            var Q227;
            {var subQ0=sQuery(id+"F16.wireOp",EDGE,"E8.13.1");var subQ1=sQuery(id+"F16.wireOp",EDGE,"E8.13.0");Q227=makeQuery(id+"F17.opExtrude","SWEPT_EDGE",EDGE,{"disambiguationData":[OSD([subQ1,subQ0]),TDD([makeQuery(id+"F16.imprint","INTERSECT",VERTEX,{"disambiguationData":[OD(1.0)],"derivedFrom":[subQ1,subQ0]})])]});}
            var Q228;
            {var subQ0=sQuery(id+"F16.wireOp",EDGE,"E8.9.1");var subQ1=sQuery(id+"F16.wireOp",EDGE,"E8.9.0");Q228=makeQuery(id+"F17.opExtrude","SWEPT_EDGE",EDGE,{"disambiguationData":[OSD([subQ1,subQ0]),TDD([makeQuery(id+"F16.imprint","INTERSECT",VERTEX,{"disambiguationData":[OD(0.0)],"derivedFrom":[subQ1,subQ0]})])]});}
            var Q229;
            Q229=makeQuery(id+"F17.opExtrude","CAP_EDGE",EDGE,{"disambiguationData":[OSD([sQuery(id+"F16.wireOp",EDGE,"E8.25.1")])],"isStart":false});
            var Q230;
            {var subQ0=sQuery(id+"F16.wireOp",EDGE,"E8.19.1");var subQ1=sQuery(id+"F16.wireOp",EDGE,"E8.19.0");Q230=makeQuery(id+"F17.opExtrude","SWEPT_EDGE",EDGE,{"disambiguationData":[OSD([subQ1,subQ0]),TDD([makeQuery(id+"F16.imprint","INTERSECT",VERTEX,{"disambiguationData":[OD(0.0)],"derivedFrom":[subQ1,subQ0]})])]});}
            var Q231;
            Q231=makeQuery(id+"F17.opExtrude","CAP_EDGE",EDGE,{"disambiguationData":[OSD([sQuery(id+"F16.wireOp",EDGE,"E8.10.1")])],"isStart":false});
            var Q232;
            {var subQ0=sQuery(id+"F16.wireOp",EDGE,"E8.9.1");var subQ1=sQuery(id+"F16.wireOp",EDGE,"E8.9.0");Q232=makeQuery(id+"F17.opExtrude","SWEPT_EDGE",EDGE,{"disambiguationData":[OSD([subQ1,subQ0]),TDD([makeQuery(id+"F16.imprint","INTERSECT",VERTEX,{"disambiguationData":[OD(1.0)],"derivedFrom":[subQ1,subQ0]})])]});}
            var Q233;
            Q233=makeQuery(id+"F17.opExtrude","CAP_EDGE",EDGE,{"disambiguationData":[OSD([sQuery(id+"F16.wireOp",EDGE,"E8.12.1")])],"isStart":false});
            var Q234;
            Q234=makeQuery(id+"F17.opExtrude","CAP_EDGE",EDGE,{"disambiguationData":[OSD([sQuery(id+"F16.wireOp",EDGE,"E8.14.1")])],"isStart":false});
            var Q235;
            Q235=makeQuery(id+"F17.opExtrude","CAP_EDGE",EDGE,{"disambiguationData":[OSD([sQuery(id+"F16.wireOp",EDGE,"E8.8.1")])],"isStart":false});
            var Q236;
            {var subQ0=sQuery(id+"F16.wireOp",EDGE,"E8.25.1");var subQ1=sQuery(id+"F16.wireOp",EDGE,"E8.25.0");Q236=makeQuery(id+"F17.opExtrude","SWEPT_EDGE",EDGE,{"disambiguationData":[OSD([subQ1,subQ0]),TDD([makeQuery(id+"F16.imprint","INTERSECT",VERTEX,{"disambiguationData":[OD(0.0)],"derivedFrom":[subQ1,subQ0]})])]});}
            var Q237;
            {var subQ0=sQuery(id+"F16.wireOp",EDGE,"E8.11.1");var subQ1=sQuery(id+"F16.wireOp",EDGE,"E8.11.0");Q237=makeQuery(id+"F17.opExtrude","SWEPT_EDGE",EDGE,{"disambiguationData":[OSD([subQ1,subQ0]),TDD([makeQuery(id+"F16.imprint","INTERSECT",VERTEX,{"disambiguationData":[OD(1.0)],"derivedFrom":[subQ1,subQ0]})])]});}
            var Q238;
            {var subQ0=sQuery(id+"F16.wireOp",EDGE,"E8.16.1");var subQ1=sQuery(id+"F16.wireOp",EDGE,"E8.16.0");Q238=makeQuery(id+"F17.opExtrude","SWEPT_EDGE",EDGE,{"disambiguationData":[OSD([subQ1,subQ0]),TDD([makeQuery(id+"F16.imprint","INTERSECT",VERTEX,{"disambiguationData":[OD(0.0)],"derivedFrom":[subQ1,subQ0]})])]});}
            var Q239;
            {var subQ0=sQuery(id+"F16.wireOp",EDGE,"E8.20.1");var subQ1=sQuery(id+"F16.wireOp",EDGE,"E8.20.0");Q239=makeQuery(id+"F17.opExtrude","SWEPT_EDGE",EDGE,{"disambiguationData":[OSD([subQ1,subQ0]),TDD([makeQuery(id+"F16.imprint","INTERSECT",VERTEX,{"disambiguationData":[OD(0.0)],"derivedFrom":[subQ1,subQ0]})])]});}
            var Q240;
            {var subQ0=sQuery(id+"F16.wireOp",EDGE,"E8.22.1");var subQ1=sQuery(id+"F16.wireOp",EDGE,"E8.22.0");Q240=makeQuery(id+"F17.opExtrude","SWEPT_EDGE",EDGE,{"disambiguationData":[OSD([subQ1,subQ0]),TDD([makeQuery(id+"F16.imprint","INTERSECT",VERTEX,{"disambiguationData":[OD(1.0)],"derivedFrom":[subQ1,subQ0]})])]});}
            var Q241;
            Q241=makeQuery(id+"F17.opExtrude","CAP_EDGE",EDGE,{"disambiguationData":[OSD([sQuery(id+"F16.wireOp",EDGE,"E8.9.1")])],"isStart":false});
            var Q242;
            {var subQ0=sQuery(id+"F16.wireOp",EDGE,"E8.14.1");var subQ1=sQuery(id+"F16.wireOp",EDGE,"E8.14.0");Q242=makeQuery(id+"F17.opExtrude","SWEPT_EDGE",EDGE,{"disambiguationData":[OSD([subQ1,subQ0]),TDD([makeQuery(id+"F16.imprint","INTERSECT",VERTEX,{"disambiguationData":[OD(0.0)],"derivedFrom":[subQ1,subQ0]})])]});}
            var Q243;
            {var subQ0=sQuery(id+"F16.wireOp",EDGE,"E8.21.1");var subQ1=sQuery(id+"F16.wireOp",EDGE,"E8.21.0");Q243=makeQuery(id+"F17.opExtrude","SWEPT_EDGE",EDGE,{"disambiguationData":[OSD([subQ1,subQ0]),TDD([makeQuery(id+"F16.imprint","INTERSECT",VERTEX,{"disambiguationData":[OD(0.0)],"derivedFrom":[subQ1,subQ0]})])]});}
            var Q244;
            {var subQ0=sQuery(id+"F16.wireOp",EDGE,"E8.28.1");var subQ1=sQuery(id+"F16.wireOp",EDGE,"E8.28.0");Q244=makeQuery(id+"F17.opExtrude","SWEPT_EDGE",EDGE,{"disambiguationData":[OSD([subQ1,subQ0]),TDD([makeQuery(id+"F16.imprint","INTERSECT",VERTEX,{"disambiguationData":[OD(0.0)],"derivedFrom":[subQ1,subQ0]})])]});}
            var Q245;
            {var subQ0=sQuery(id+"F16.wireOp",EDGE,"E8.21.1");var subQ1=sQuery(id+"F16.wireOp",EDGE,"E8.21.0");Q245=makeQuery(id+"F17.opExtrude","SWEPT_EDGE",EDGE,{"disambiguationData":[OSD([subQ1,subQ0]),TDD([makeQuery(id+"F16.imprint","INTERSECT",VERTEX,{"disambiguationData":[OD(1.0)],"derivedFrom":[subQ1,subQ0]})])]});}
            var Q246;
            {var subQ0=sQuery(id+"F16.wireOp",EDGE,"E8.27.1");var subQ1=sQuery(id+"F16.wireOp",EDGE,"E8.27.0");Q246=makeQuery(id+"F17.opExtrude","SWEPT_EDGE",EDGE,{"disambiguationData":[OSD([subQ1,subQ0]),TDD([makeQuery(id+"F16.imprint","INTERSECT",VERTEX,{"disambiguationData":[OD(0.0)],"derivedFrom":[subQ1,subQ0]})])]});}
            var Q247;
            {var subQ0=sQuery(id+"F16.wireOp",EDGE,"E8.27.1");var subQ1=sQuery(id+"F16.wireOp",EDGE,"E8.27.0");Q247=makeQuery(id+"F17.opExtrude","SWEPT_EDGE",EDGE,{"disambiguationData":[OSD([subQ1,subQ0]),TDD([makeQuery(id+"F16.imprint","INTERSECT",VERTEX,{"disambiguationData":[OD(1.0)],"derivedFrom":[subQ1,subQ0]})])]});}
            var Q248;
            {var subQ0=sQuery(id+"F16.wireOp",EDGE,"E8.26.1");var subQ1=sQuery(id+"F16.wireOp",EDGE,"E8.26.0");Q248=makeQuery(id+"F17.opExtrude","SWEPT_EDGE",EDGE,{"disambiguationData":[OSD([subQ1,subQ0]),TDD([makeQuery(id+"F16.imprint","INTERSECT",VERTEX,{"disambiguationData":[OD(1.0)],"derivedFrom":[subQ1,subQ0]})])]});}
            var Q249;
            {var subQ0=sQuery(id+"F16.wireOp",EDGE,"E8.23.1");var subQ1=sQuery(id+"F16.wireOp",EDGE,"E8.23.0");Q249=makeQuery(id+"F17.opExtrude","SWEPT_EDGE",EDGE,{"disambiguationData":[OSD([subQ1,subQ0]),TDD([makeQuery(id+"F16.imprint","INTERSECT",VERTEX,{"disambiguationData":[OD(0.0)],"derivedFrom":[subQ1,subQ0]})])]});}
            var Q250;
            {var subQ0=sQuery(id+"F16.wireOp",EDGE,"E8.19.1");var subQ1=sQuery(id+"F16.wireOp",EDGE,"E8.19.0");Q250=makeQuery(id+"F17.opExtrude","SWEPT_EDGE",EDGE,{"disambiguationData":[OSD([subQ1,subQ0]),TDD([makeQuery(id+"F16.imprint","INTERSECT",VERTEX,{"disambiguationData":[OD(1.0)],"derivedFrom":[subQ1,subQ0]})])]});}
            var Q251;
            Q251=makeQuery(id+"F17.opExtrude","CAP_EDGE",EDGE,{"disambiguationData":[OSD([sQuery(id+"F16.wireOp",EDGE,"E8.15.1")])],"isStart":false});
            var Q252;
            {var subQ0=sQuery(id+"F16.wireOp",EDGE,"E8.7.1");var subQ1=sQuery(id+"F16.wireOp",EDGE,"E8.7.0");Q252=makeQuery(id+"F17.opExtrude","SWEPT_EDGE",EDGE,{"disambiguationData":[OSD([subQ1,subQ0]),TDD([makeQuery(id+"F16.imprint","INTERSECT",VERTEX,{"disambiguationData":[OD(0.0)],"derivedFrom":[subQ1,subQ0]})])]});}
            var Q253;
            {var subQ0=sQuery(id+"F16.wireOp",EDGE,"E8.14.1");var subQ1=sQuery(id+"F16.wireOp",EDGE,"E8.14.0");Q253=makeQuery(id+"F17.opExtrude","SWEPT_EDGE",EDGE,{"disambiguationData":[OSD([subQ1,subQ0]),TDD([makeQuery(id+"F16.imprint","INTERSECT",VERTEX,{"disambiguationData":[OD(1.0)],"derivedFrom":[subQ1,subQ0]})])]});}
            var Q254;
            {var subQ0=sQuery(id+"F16.wireOp",EDGE,"E8.24.1");var subQ1=sQuery(id+"F16.wireOp",EDGE,"E8.24.0");Q254=makeQuery(id+"F17.opExtrude","SWEPT_EDGE",EDGE,{"disambiguationData":[OSD([subQ1,subQ0]),TDD([makeQuery(id+"F16.imprint","INTERSECT",VERTEX,{"disambiguationData":[OD(0.0)],"derivedFrom":[subQ1,subQ0]})])]});}
            var Q255;
            {var subQ0=sQuery(id+"F16.wireOp",EDGE,"E8.12.1");var subQ1=sQuery(id+"F16.wireOp",EDGE,"E8.12.0");Q255=makeQuery(id+"F17.opExtrude","SWEPT_EDGE",EDGE,{"disambiguationData":[OSD([subQ1,subQ0]),TDD([makeQuery(id+"F16.imprint","INTERSECT",VERTEX,{"disambiguationData":[OD(1.0)],"derivedFrom":[subQ1,subQ0]})])]});}
            var Q256;
            {var subQ0=sQuery(id+"F16.wireOp",EDGE,"E8.24.1");var subQ1=sQuery(id+"F16.wireOp",EDGE,"E8.24.0");Q256=makeQuery(id+"F17.opExtrude","SWEPT_EDGE",EDGE,{"disambiguationData":[OSD([subQ1,subQ0]),TDD([makeQuery(id+"F16.imprint","INTERSECT",VERTEX,{"disambiguationData":[OD(1.0)],"derivedFrom":[subQ1,subQ0]})])]});}
            var Q257;
            {var subQ0=sQuery(id+"F16.wireOp",EDGE,"E8.8.1");var subQ1=sQuery(id+"F16.wireOp",EDGE,"E8.8.0");Q257=makeQuery(id+"F17.opExtrude","SWEPT_EDGE",EDGE,{"disambiguationData":[OSD([subQ1,subQ0]),TDD([makeQuery(id+"F16.imprint","INTERSECT",VERTEX,{"disambiguationData":[OD(1.0)],"derivedFrom":[subQ1,subQ0]})])]});}
            var Q258;
            {var subQ0=sQuery(id+"F16.wireOp",EDGE,"E8.16.1");var subQ1=sQuery(id+"F16.wireOp",EDGE,"E8.16.0");Q258=makeQuery(id+"F17.opExtrude","SWEPT_EDGE",EDGE,{"disambiguationData":[OSD([subQ1,subQ0]),TDD([makeQuery(id+"F16.imprint","INTERSECT",VERTEX,{"disambiguationData":[OD(1.0)],"derivedFrom":[subQ1,subQ0]})])]});}
            var Q259;
            {var subQ0=sQuery(id+"F16.wireOp",EDGE,"E8.20.1");var subQ1=sQuery(id+"F16.wireOp",EDGE,"E8.20.0");Q259=makeQuery(id+"F17.opExtrude","SWEPT_EDGE",EDGE,{"disambiguationData":[OSD([subQ1,subQ0]),TDD([makeQuery(id+"F16.imprint","INTERSECT",VERTEX,{"disambiguationData":[OD(1.0)],"derivedFrom":[subQ1,subQ0]})])]});}
            var Q260;
            {var subQ0=sQuery(id+"F16.wireOp",EDGE,"E8.12.1");var subQ1=sQuery(id+"F16.wireOp",EDGE,"E8.12.0");Q260=makeQuery(id+"F17.opExtrude","SWEPT_EDGE",EDGE,{"disambiguationData":[OSD([subQ1,subQ0]),TDD([makeQuery(id+"F16.imprint","INTERSECT",VERTEX,{"disambiguationData":[OD(0.0)],"derivedFrom":[subQ1,subQ0]})])]});}
            var Q261;
            {var subQ0=sQuery(id+"F16.wireOp",EDGE,"E8.15.1");var subQ1=sQuery(id+"F16.wireOp",EDGE,"E8.15.0");Q261=makeQuery(id+"F17.opExtrude","SWEPT_EDGE",EDGE,{"disambiguationData":[OSD([subQ1,subQ0]),TDD([makeQuery(id+"F16.imprint","INTERSECT",VERTEX,{"disambiguationData":[OD(0.0)],"derivedFrom":[subQ1,subQ0]})])]});}
            var Q262;
            {var subQ0=sQuery(id+"F16.wireOp",EDGE,"E8.10.1");var subQ1=sQuery(id+"F16.wireOp",EDGE,"E8.10.0");Q262=makeQuery(id+"F17.opExtrude","SWEPT_EDGE",EDGE,{"disambiguationData":[OSD([subQ1,subQ0]),TDD([makeQuery(id+"F16.imprint","INTERSECT",VERTEX,{"disambiguationData":[OD(1.0)],"derivedFrom":[subQ1,subQ0]})])]});}
            var Q263;
            {var subQ0=sQuery(id+"F16.wireOp",EDGE,"E8.23.1");var subQ1=sQuery(id+"F16.wireOp",EDGE,"E8.23.0");Q263=makeQuery(id+"F17.opExtrude","SWEPT_EDGE",EDGE,{"disambiguationData":[OSD([subQ1,subQ0]),TDD([makeQuery(id+"F16.imprint","INTERSECT",VERTEX,{"disambiguationData":[OD(1.0)],"derivedFrom":[subQ1,subQ0]})])]});}
            var Q264;
            {var subQ0=sQuery(id+"F16.wireOp",EDGE,"E8.17.1");var subQ1=sQuery(id+"F16.wireOp",EDGE,"E8.17.0");Q264=makeQuery(id+"F17.opExtrude","SWEPT_EDGE",EDGE,{"disambiguationData":[OSD([subQ1,subQ0]),TDD([makeQuery(id+"F16.imprint","INTERSECT",VERTEX,{"disambiguationData":[OD(1.0)],"derivedFrom":[subQ1,subQ0]})])]});}
            var Q265;
            {var subQ0=sQuery(id+"F16.wireOp",EDGE,"E8.18.1");var subQ1=sQuery(id+"F16.wireOp",EDGE,"E8.18.0");Q265=makeQuery(id+"F17.opExtrude","SWEPT_EDGE",EDGE,{"disambiguationData":[OSD([subQ1,subQ0]),TDD([makeQuery(id+"F16.imprint","INTERSECT",VERTEX,{"disambiguationData":[OD(0.0)],"derivedFrom":[subQ1,subQ0]})])]});}
            var Q266;
            {var subQ0=sQuery(id+"F16.wireOp",EDGE,"E8.17.1");var subQ1=sQuery(id+"F16.wireOp",EDGE,"E8.17.0");Q266=makeQuery(id+"F17.opExtrude","SWEPT_EDGE",EDGE,{"disambiguationData":[OSD([subQ1,subQ0]),TDD([makeQuery(id+"F16.imprint","INTERSECT",VERTEX,{"disambiguationData":[OD(0.0)],"derivedFrom":[subQ1,subQ0]})])]});}
            var Q267;
            {var subQ0=sQuery(id+"F16.wireOp",EDGE,"E8.13.1");var subQ1=sQuery(id+"F16.wireOp",EDGE,"E8.13.0");Q267=makeQuery(id+"F17.opExtrude","SWEPT_EDGE",EDGE,{"disambiguationData":[OSD([subQ1,subQ0]),TDD([makeQuery(id+"F16.imprint","INTERSECT",VERTEX,{"disambiguationData":[OD(0.0)],"derivedFrom":[subQ1,subQ0]})])]});}
            var Q268;
            {var subQ0=sQuery(id+"F16.wireOp",EDGE,"E8.18.1");var subQ1=sQuery(id+"F16.wireOp",EDGE,"E8.18.0");Q268=makeQuery(id+"F17.opExtrude","SWEPT_EDGE",EDGE,{"disambiguationData":[OSD([subQ1,subQ0]),TDD([makeQuery(id+"F16.imprint","INTERSECT",VERTEX,{"disambiguationData":[OD(1.0)],"derivedFrom":[subQ1,subQ0]})])]});}
            var Q269;
            {var subQ0=sQuery(id+"F16.wireOp",EDGE,"E8.7.1");var subQ1=sQuery(id+"F16.wireOp",EDGE,"E8.7.0");Q269=makeQuery(id+"F17.opExtrude","SWEPT_EDGE",EDGE,{"disambiguationData":[OSD([subQ1,subQ0]),TDD([makeQuery(id+"F16.imprint","INTERSECT",VERTEX,{"disambiguationData":[OD(1.0)],"derivedFrom":[subQ1,subQ0]})])]});}
            var Q270;
            {var subQ0=sQuery(id+"F16.wireOp",EDGE,"E8.10.1");var subQ1=sQuery(id+"F16.wireOp",EDGE,"E8.10.0");Q270=makeQuery(id+"F17.opExtrude","SWEPT_EDGE",EDGE,{"disambiguationData":[OSD([subQ1,subQ0]),TDD([makeQuery(id+"F16.imprint","INTERSECT",VERTEX,{"disambiguationData":[OD(0.0)],"derivedFrom":[subQ1,subQ0]})])]});}
            var Q271;
            {var subQ0=sQuery(id+"F16.wireOp",EDGE,"E8.22.1");var subQ1=sQuery(id+"F16.wireOp",EDGE,"E8.22.0");Q271=makeQuery(id+"F17.opExtrude","SWEPT_EDGE",EDGE,{"disambiguationData":[OSD([subQ1,subQ0]),TDD([makeQuery(id+"F16.imprint","INTERSECT",VERTEX,{"disambiguationData":[OD(0.0)],"derivedFrom":[subQ1,subQ0]})])]});}
            var Q272;
            {var subQ0=sQuery(id+"F16.wireOp",EDGE,"E8.6.1");var subQ1=sQuery(id+"F16.wireOp",EDGE,"E8.6.0");Q272=makeQuery(id+"F17.opExtrude","SWEPT_EDGE",EDGE,{"disambiguationData":[OSD([subQ1,subQ0]),TDD([makeQuery(id+"F16.imprint","INTERSECT",VERTEX,{"disambiguationData":[OD(0.0)],"derivedFrom":[subQ1,subQ0]})])]});}
            var Q273;
            {var subQ0=sQuery(id+"F16.wireOp",EDGE,"E8.25.1");var subQ1=sQuery(id+"F16.wireOp",EDGE,"E8.25.0");Q273=makeQuery(id+"F17.opExtrude","SWEPT_EDGE",EDGE,{"disambiguationData":[OSD([subQ1,subQ0]),TDD([makeQuery(id+"F16.imprint","INTERSECT",VERTEX,{"disambiguationData":[OD(1.0)],"derivedFrom":[subQ1,subQ0]})])]});}
            var Q274;
            {var subQ0=sQuery(id+"F16.wireOp",EDGE,"E8.15.1");var subQ1=sQuery(id+"F16.wireOp",EDGE,"E8.15.0");Q274=makeQuery(id+"F17.opExtrude","SWEPT_EDGE",EDGE,{"disambiguationData":[OSD([subQ1,subQ0]),TDD([makeQuery(id+"F16.imprint","INTERSECT",VERTEX,{"disambiguationData":[OD(1.0)],"derivedFrom":[subQ1,subQ0]})])]});}
            var Q275;
            {var subQ0=sQuery(id+"F16.wireOp",EDGE,"E8.8.1");var subQ1=sQuery(id+"F16.wireOp",EDGE,"E8.8.0");Q275=makeQuery(id+"F17.opExtrude","SWEPT_EDGE",EDGE,{"disambiguationData":[OSD([subQ1,subQ0]),TDD([makeQuery(id+"F16.imprint","INTERSECT",VERTEX,{"disambiguationData":[OD(0.0)],"derivedFrom":[subQ1,subQ0]})])]});}
            fillet(context, id + "F18", {"entities" : qUnion([Q0, Q1, Q2, Q3, Q4, Q5, Q6, Q7, Q8, Q9, Q10, Q11, Q12, Q13, Q14, Q15, Q16, Q17, Q18, Q19, Q20, Q21, Q22, Q23, Q24, Q25, Q26, Q27, Q28, Q29, Q30, Q31, Q32, Q33, Q34, Q35, Q36, Q37, Q38, Q39, Q40, Q41, Q42, Q43, Q44, Q45, Q46, Q47, Q48, Q49, Q50, Q51, Q52, Q53, Q54, Q55, Q56, Q57, Q58, Q59, Q60, Q61, Q62, Q63, Q64, Q65, Q66, Q67, Q68, Q69, Q70, Q71, Q72, Q73, Q74, Q75, Q76, Q77, Q78, Q79, Q80, Q81, Q82, Q83, Q84, Q85, Q86, Q87, Q88, Q89, Q90, Q91, Q92, Q93, Q94, Q95, Q96, Q97, Q98, Q99, Q100, Q101, Q102, Q103, Q104, Q105, Q106, Q107, Q108, Q109, Q110, Q111, Q112, Q113, Q114, Q115, Q116, Q117, Q118, Q119, Q120, Q121, Q122, Q123, Q124, Q125, Q126, Q127, Q128, Q129, Q130, Q131, Q132, Q133, Q134, Q135, Q136, Q137, Q138, Q139, Q140, Q141, Q142, Q143, Q144, Q145, Q146, Q147, Q148, Q149, Q150, Q151, Q152, Q153, Q154, Q155, Q156, Q157, Q158, Q159, Q160, Q161, Q162, Q163, Q164, Q165, Q166, Q167, Q168, Q169, Q170, Q171, Q172, Q173, Q174, Q175, Q176, Q177, Q178, Q179, Q180, Q181, Q182, Q183, Q184, Q185, Q186, Q187, Q188, Q189, Q190, Q191, Q192, Q193, Q194, Q195, Q196, Q197, Q198, Q199, Q200, Q201, Q202, Q203, Q204, Q205, Q206, Q207, Q208, Q209, Q210, Q211, Q212, Q213, Q214, Q215, Q216, Q217, Q218, Q219, Q220, Q221, Q222, Q223, Q224, Q225, Q226, Q227, Q228, Q229, Q230, Q231, Q232, Q233, Q234, Q235, Q236, Q237, Q238, Q239, Q240, Q241, Q242, Q243, Q244, Q245, Q246, Q247, Q248, Q249, Q250, Q251, Q252, Q253, Q254, Q255, Q256, Q257, Q258, Q259, Q260, Q261, Q262, Q263, Q264, Q265, Q266, Q267, Q268, Q269, Q270, Q271, Q272, Q273, Q274, Q275]), "radius" : 0.16 * mm, "tangentPropagation" : true, "allowEdgeOverflow" : false});
        }
        {
            var Q0;
            Q0=qCreatedBy(makeId("Top.planeOp"),FACE);
            var sketch = newSketch(context, id + "F19", { "sketchPlane" : qUnion([Q0])});
            skLineSegment(sketch, "E9.bottom", {"start": v(4, 4) * mm, "end": v(-4, 4) * mm, "construction": true});
            skLineSegment(sketch, "E9.left", {"start": v(4, 4) * mm, "end": v(4, -4) * mm, "construction": true});
            skLineSegment(sketch, "E9.right", {"start": v(-4, 4) * mm, "end": v(-4, -4) * mm, "construction": true});
            skPoint(sketch, "E9.middle", {"position": v(0, 0) * mm});
            skLineSegment(sketch, "E10.bottom", {"start": v(-4, -4) * mm, "end": v(4, -4) * mm});
            skLineSegment(sketch, "E10.top", {"start": v(-4, -3) * mm, "end": v(4, -3) * mm});
            skLineSegment(sketch, "E10.left", {"start": v(-4, -4) * mm, "end": v(-4, -3) * mm});
            skLineSegment(sketch, "E10.right", {"start": v(4, -4) * mm, "end": v(4, -3) * mm});
            skLineSegment(sketch, "E11", {"start": v(-4, -2) * mm, "end": v(4, -2) * mm, "construction": true});
            skLineSegment(sketch, "E12", {"start": v(0, -2) * mm, "end": v(0, 4) * mm, "construction": true});
            skLineSegment(sketch, "E13", {"start": v(-0.5, -2) * mm, "end": v(-0.5, 4) * mm, "construction": true});
            skLineSegment(sketch, "E14.MirrorCS", {"start": v(0.5, -2) * mm, "end": v(0.5, 4) * mm, "construction": true});
            skLineSegment(sketch, "E15", {"start": v(0.5, 4) * mm, "end": v(4, 4) * mm});
            skLineSegment(sketch, "E16", {"start": v(4, 4) * mm, "end": v(4, 0.5) * mm});
            skLineSegment(sketch, "E17", {"start": v(4, 0.5) * mm, "end": v(1.62, 0.5) * mm});
            skLineSegment(sketch, "E18", {"start": v(1.62, 0.5) * mm, "end": v(1.62, -1) * mm});
            skLineSegment(sketch, "E19", {"start": v(1.62, -1) * mm, "end": v(4, -1) * mm});
            skLineSegment(sketch, "E20", {"start": v(4, -1) * mm, "end": v(4, -2) * mm});
            skLineSegment(sketch, "E21", {"start": v(4, -2) * mm, "end": v(0.5, -2) * mm});
            skLineSegment(sketch, "E22", {"start": v(0.5, -2) * mm, "end": v(0.5, 1.5) * mm});
            skLineSegment(sketch, "E23", {"start": v(0.5, 1.5) * mm, "end": v(2.88, 1.5) * mm});
            skLineSegment(sketch, "E24", {"start": v(2.88, 1.5) * mm, "end": v(2.88, 3) * mm});
            skLineSegment(sketch, "E25", {"start": v(2.88, 3) * mm, "end": v(0.5, 3) * mm});
            skLineSegment(sketch, "E26", {"start": v(0.5, 3) * mm, "end": v(0.5, 4) * mm});
            skLineSegment(sketch, "E27", {"start": v(-4, 4) * mm, "end": v(-0.5, 4) * mm});
            skLineSegment(sketch, "E28", {"start": v(-0.5, 0.5) * mm, "end": v(-0.5, 4) * mm});
            skLineSegment(sketch, "E29", {"start": v(-0.5, 0.5) * mm, "end": v(-2.88, 0.5) * mm});
            skLineSegment(sketch, "E30", {"start": v(-2.88, 0.5) * mm, "end": v(-2.88, -1) * mm});
            skLineSegment(sketch, "E31", {"start": v(-2.88, -1) * mm, "end": v(-0.5, -1) * mm});
            skLineSegment(sketch, "E32", {"start": v(-0.5, -1) * mm, "end": v(-0.5, -2) * mm});
            skLineSegment(sketch, "E33", {"start": v(-0.5, -2) * mm, "end": v(-4, -2) * mm});
            skLineSegment(sketch, "E34", {"start": v(-4, -2) * mm, "end": v(-4, 1.5) * mm});
            skLineSegment(sketch, "E35", {"start": v(-4, 1.5) * mm, "end": v(-1.62, 1.5) * mm});
            skLineSegment(sketch, "E36", {"start": v(-1.62, 1.5) * mm, "end": v(-1.62, 3) * mm});
            skLineSegment(sketch, "E37", {"start": v(-1.62, 3) * mm, "end": v(-4, 3) * mm});
            skLineSegment(sketch, "E38", {"start": v(-4, 3) * mm, "end": v(-4, 4) * mm});
            skLineSegment(sketch, "E39.bottom", {"start": v(1.5, 9) * mm, "end": v(-1.5, 9) * mm, "construction": true});
            skLineSegment(sketch, "E39.top", {"start": v(1.5, 13) * mm, "end": v(-1.5, 13) * mm, "construction": true});
            skLineSegment(sketch, "E39.left", {"start": v(1.5, 9) * mm, "end": v(1.5, 13) * mm, "construction": true});
            skLineSegment(sketch, "E39.right", {"start": v(-1.5, 9) * mm, "end": v(-1.5, 13) * mm, "construction": true});
            skPoint(sketch, "E39.middle", {"position": v(0, 11) * mm});
            skLineSegment(sketch, "E40", {"start": v(-1.5, 13) * mm, "end": v(-1.5, 9) * mm});
            skLineSegment(sketch, "E41", {"start": v(0, 9) * mm, "end": v(-1.5, 9) * mm});
            skLineSegment(sketch, "E42", {"start": v(-1.5, 13) * mm, "end": v(0, 13) * mm});
            skEllipse(sketch, "E43", {"center": v(0, 11) * mm, "majorRadius": 2 * mm, "minorRadius": 1.5 * mm, "majorAxis": v(0, -1)});
            skLineSegment(sketch, "E44", {"start": v(-1.03, 12.46) * mm, "end": v(-1.03, 9.54) * mm});
            skLineSegment(sketch, "E45", {"start": v(-1.03, 9.54) * mm, "end": v(0, 9.54) * mm});
            skLineSegment(sketch, "E46", {"start": v(-1.03, 12.46) * mm, "end": v(0, 12.46) * mm});
            skEllipse(sketch, "E47", {"center": v(0, 11) * mm, "majorRadius": 1.46 * mm, "minorRadius": 1.03 * mm, "majorAxis": v(0, -1)});
            skSolve(sketch);
        }
        {
            var Q0;
            Q0 = qSketchRegion(id + "F19", true);
            extrude(context, id + "F20", {"entities" : qUnion([Q0]), "operationType" : NewBodyOperationType.ADD, "depth" : 78 * mm, "hasSecondDirection" : true, "secondDirectionOppositeDirection" : false, "secondDirectionDepth" : 76.1 * mm});
        }
        {
            var Q0;
            Q0=makeQuery(id+"F20.opExtrude","CAP_FACE",FACE,{"disambiguationData":[OSD([sQuery(id+"F19.wireOp",EDGE,"E10.bottom"),sQuery(id+"F19.wireOp",EDGE,"E10.top"),sQuery(id+"F19.wireOp",EDGE,"E10.left"),sQuery(id+"F19.wireOp",EDGE,"E10.right")])],"isStart":false});
            var Q1;
            Q1=makeQuery(id+"F20.opExtrude","CAP_FACE",FACE,{"disambiguationData":[OSD([sQuery(id+"F19.wireOp",EDGE,"E15"),sQuery(id+"F19.wireOp",EDGE,"E16"),sQuery(id+"F19.wireOp",EDGE,"E17"),sQuery(id+"F19.wireOp",EDGE,"E18"),sQuery(id+"F19.wireOp",EDGE,"E19"),sQuery(id+"F19.wireOp",EDGE,"E20"),sQuery(id+"F19.wireOp",EDGE,"E21"),sQuery(id+"F19.wireOp",EDGE,"E22"),sQuery(id+"F19.wireOp",EDGE,"E23"),sQuery(id+"F19.wireOp",EDGE,"E24"),sQuery(id+"F19.wireOp",EDGE,"E25"),sQuery(id+"F19.wireOp",EDGE,"E26")])],"isStart":false});
            var Q2;
            Q2=makeQuery(id+"F20.opExtrude","SWEPT_FACE",FACE,{"disambiguationData":[OSD([sQuery(id+"F19.wireOp",EDGE,"E25")])]});
            var Q3;
            Q3=makeQuery(id+"F20.opExtrude","SWEPT_FACE",FACE,{"disambiguationData":[OSD([sQuery(id+"F19.wireOp",EDGE,"E24")])]});
            var Q4;
            Q4=makeQuery(id+"F20.opExtrude","SWEPT_FACE",FACE,{"disambiguationData":[OSD([sQuery(id+"F19.wireOp",EDGE,"E10.bottom")])]});
            var Q5;
            Q5=makeQuery(id+"F20.opExtrude","SWEPT_FACE",FACE,{"disambiguationData":[OSD([sQuery(id+"F19.wireOp",EDGE,"E10.right")])]});
            var Q6;
            Q6=makeQuery(id+"F20.opExtrude","SWEPT_FACE",FACE,{"disambiguationData":[OSD([sQuery(id+"F19.wireOp",EDGE,"E16")])]});
            var Q7;
            Q7=makeQuery(id+"F20.opExtrude","SWEPT_FACE",FACE,{"disambiguationData":[OSD([sQuery(id+"F19.wireOp",EDGE,"E21")])]});
            var Q8;
            Q8=makeQuery(id+"F20.opExtrude","CAP_EDGE",EDGE,{"disambiguationData":[OSD([sQuery(id+"F19.wireOp",EDGE,"E10.bottom")])],"isStart":false});
            var Q9;
            Q9=makeQuery(id+"F20.opExtrude","CAP_EDGE",EDGE,{"disambiguationData":[OSD([sQuery(id+"F19.wireOp",EDGE,"E19")])],"isStart":false});
            var Q10;
            Q10=makeQuery(id+"F20.opExtrude","CAP_EDGE",EDGE,{"disambiguationData":[OSD([sQuery(id+"F19.wireOp",EDGE,"E27")])],"isStart":false});
            var Q11;
            Q11=makeQuery(id+"F20.opExtrude","CAP_EDGE",EDGE,{"disambiguationData":[OSD([sQuery(id+"F19.wireOp",EDGE,"E35")])],"isStart":false});
            var Q12;
            Q12=makeQuery(id+"F20.opExtrude","CAP_EDGE",EDGE,{"disambiguationData":[OSD([sQuery(id+"F19.wireOp",EDGE,"E10.top")])],"isStart":false});
            var Q13;
            Q13=makeQuery(id+"F20.opExtrude","CAP_EDGE",EDGE,{"disambiguationData":[OSD([sQuery(id+"F19.wireOp",EDGE,"E28")])],"isStart":false});
            var Q14;
            Q14=makeQuery(id+"F20.opExtrude","CAP_EDGE",EDGE,{"disambiguationData":[OSD([sQuery(id+"F19.wireOp",EDGE,"E36")])],"isStart":false});
            var Q15;
            Q15=makeQuery(id+"F20.opExtrude","CAP_EDGE",EDGE,{"disambiguationData":[OSD([sQuery(id+"F19.wireOp",EDGE,"E21")])],"isStart":false});
            var Q16;
            Q16=makeQuery(id+"F20.opExtrude","CAP_EDGE",EDGE,{"disambiguationData":[OSD([sQuery(id+"F19.wireOp",EDGE,"E29")])],"isStart":false});
            var Q17;
            Q17=makeQuery(id+"F20.opExtrude","CAP_EDGE",EDGE,{"disambiguationData":[OSD([sQuery(id+"F19.wireOp",EDGE,"E37")])],"isStart":false});
            var Q18;
            Q18=makeQuery(id+"F20.opExtrude","CAP_EDGE",EDGE,{"disambiguationData":[OSD([sQuery(id+"F19.wireOp",EDGE,"E22")])],"isStart":false});
            var Q19;
            Q19=makeQuery(id+"F20.opExtrude","CAP_EDGE",EDGE,{"disambiguationData":[OSD([sQuery(id+"F19.wireOp",EDGE,"E30")])],"isStart":false});
            var Q20;
            Q20=makeQuery(id+"F20.opExtrude","CAP_EDGE",EDGE,{"disambiguationData":[OSD([sQuery(id+"F19.wireOp",EDGE,"E15")])],"isStart":false});
            var Q21;
            Q21=makeQuery(id+"F20.opExtrude","CAP_EDGE",EDGE,{"disambiguationData":[OSD([sQuery(id+"F19.wireOp",EDGE,"E23")])],"isStart":false});
            var Q22;
            Q22=makeQuery(id+"F20.opExtrude","CAP_EDGE",EDGE,{"disambiguationData":[OSD([sQuery(id+"F19.wireOp",EDGE,"E31")])],"isStart":false});
            var Q23;
            Q23=makeQuery(id+"F20.opExtrude","CAP_FACE",FACE,{"disambiguationData":[OSD([sQuery(id+"F19.wireOp",EDGE,"E27"),sQuery(id+"F19.wireOp",EDGE,"E28"),sQuery(id+"F19.wireOp",EDGE,"E29"),sQuery(id+"F19.wireOp",EDGE,"E30"),sQuery(id+"F19.wireOp",EDGE,"E31"),sQuery(id+"F19.wireOp",EDGE,"E32"),sQuery(id+"F19.wireOp",EDGE,"E33"),sQuery(id+"F19.wireOp",EDGE,"E34"),sQuery(id+"F19.wireOp",EDGE,"E35"),sQuery(id+"F19.wireOp",EDGE,"E36"),sQuery(id+"F19.wireOp",EDGE,"E37"),sQuery(id+"F19.wireOp",EDGE,"E38")])],"isStart":false});
            var Q24;
            Q24=makeQuery(id+"F20.opExtrude","CAP_EDGE",EDGE,{"disambiguationData":[OSD([sQuery(id+"F19.wireOp",EDGE,"E16")])],"isStart":false});
            var Q25;
            Q25=makeQuery(id+"F20.opExtrude","CAP_EDGE",EDGE,{"disambiguationData":[OSD([sQuery(id+"F19.wireOp",EDGE,"E24")])],"isStart":false});
            var Q26;
            Q26=makeQuery(id+"F20.opExtrude","CAP_EDGE",EDGE,{"disambiguationData":[OSD([sQuery(id+"F19.wireOp",EDGE,"E17")])],"isStart":false});
            var Q27;
            Q27=makeQuery(id+"F20.opExtrude","CAP_EDGE",EDGE,{"disambiguationData":[OSD([sQuery(id+"F19.wireOp",EDGE,"E25")])],"isStart":false});
            var Q28;
            Q28=makeQuery(id+"F20.opExtrude","CAP_EDGE",EDGE,{"disambiguationData":[OSD([sQuery(id+"F19.wireOp",EDGE,"E33")])],"isStart":false});
            var Q29;
            Q29=makeQuery(id+"F20.opExtrude","CAP_EDGE",EDGE,{"disambiguationData":[OSD([sQuery(id+"F19.wireOp",EDGE,"E18")])],"isStart":false});
            var Q30;
            Q30=makeQuery(id+"F20.opExtrude","CAP_EDGE",EDGE,{"disambiguationData":[OSD([sQuery(id+"F19.wireOp",EDGE,"E34")])],"isStart":false});
            var Q31;
            Q31=makeQuery(id+"F20.boolean.opBoolean","INTERSECT",EDGE,{"derivedFrom":[makeQuery(id+"F6.boolean.opBoolean","COPY",FACE,{"derivedFrom":makeQuery(id+"F6.opExtrude","CAP_FACE",FACE,{"disambiguationData":[OSD([sQuery(id+"F0.wireOp",EDGE,"E2")])],"isStart":true})}),makeQuery(id+"F20.opExtrude","SWEPT_FACE",FACE,{"disambiguationData":[OSD([sQuery(id+"F19.wireOp",EDGE,"E29")])]})]});
            var Q32;
            Q32=makeQuery(id+"F20.boolean.opBoolean","INTERSECT",EDGE,{"derivedFrom":[makeQuery(id+"F6.boolean.opBoolean","COPY",FACE,{"derivedFrom":makeQuery(id+"F6.opExtrude","CAP_FACE",FACE,{"disambiguationData":[OSD([sQuery(id+"F0.wireOp",EDGE,"E2")])],"isStart":true})}),makeQuery(id+"F20.opExtrude","SWEPT_FACE",FACE,{"disambiguationData":[OSD([sQuery(id+"F19.wireOp",EDGE,"E10.right")])]})]});
            var Q33;
            Q33=makeQuery(id+"F20.opExtrude","SWEPT_FACE",FACE,{"disambiguationData":[OSD([sQuery(id+"F19.wireOp",EDGE,"E26")])]});
            var Q34;
            Q34=makeQuery(id+"F20.boolean.opBoolean","INTERSECT",EDGE,{"derivedFrom":[makeQuery(id+"F6.boolean.opBoolean","COPY",FACE,{"derivedFrom":makeQuery(id+"F6.opExtrude","CAP_FACE",FACE,{"disambiguationData":[OSD([sQuery(id+"F0.wireOp",EDGE,"E2")])],"isStart":true})}),makeQuery(id+"F20.opExtrude","SWEPT_FACE",FACE,{"disambiguationData":[OSD([sQuery(id+"F19.wireOp",EDGE,"E16")])]})]});
            var Q35;
            Q35=makeQuery(id+"F20.boolean.opBoolean","INTERSECT",EDGE,{"derivedFrom":[makeQuery(id+"F6.boolean.opBoolean","COPY",FACE,{"derivedFrom":makeQuery(id+"F6.opExtrude","CAP_FACE",FACE,{"disambiguationData":[OSD([sQuery(id+"F0.wireOp",EDGE,"E2")])],"isStart":true})}),makeQuery(id+"F20.opExtrude","SWEPT_FACE",FACE,{"disambiguationData":[OSD([sQuery(id+"F19.wireOp",EDGE,"E17")])]})]});
            var Q36;
            Q36=makeQuery(id+"F20.boolean.opBoolean","INTERSECT",EDGE,{"derivedFrom":[makeQuery(id+"F6.boolean.opBoolean","COPY",FACE,{"derivedFrom":makeQuery(id+"F6.opExtrude","CAP_FACE",FACE,{"disambiguationData":[OSD([sQuery(id+"F0.wireOp",EDGE,"E2")])],"isStart":true})}),makeQuery(id+"F20.opExtrude","SWEPT_FACE",FACE,{"disambiguationData":[OSD([sQuery(id+"F19.wireOp",EDGE,"E33")])]})]});
            var Q37;
            Q37=makeQuery(id+"F20.opExtrude","SWEPT_FACE",FACE,{"disambiguationData":[OSD([sQuery(id+"F19.wireOp",EDGE,"E28")])]});
            var Q38;
            Q38=makeQuery(id+"F20.boolean.opBoolean","INTERSECT",EDGE,{"derivedFrom":[makeQuery(id+"F6.boolean.opBoolean","COPY",FACE,{"derivedFrom":makeQuery(id+"F6.opExtrude","CAP_FACE",FACE,{"disambiguationData":[OSD([sQuery(id+"F0.wireOp",EDGE,"E2")])],"isStart":true})}),makeQuery(id+"F20.opExtrude","SWEPT_FACE",FACE,{"disambiguationData":[OSD([sQuery(id+"F19.wireOp",EDGE,"E21")])]})]});
            var Q39;
            Q39=makeQuery(id+"F20.opExtrude","SWEPT_FACE",FACE,{"disambiguationData":[OSD([sQuery(id+"F19.wireOp",EDGE,"E32")])]});
            var Q40;
            Q40=makeQuery(id+"F20.opExtrude","SWEPT_FACE",FACE,{"disambiguationData":[OSD([sQuery(id+"F19.wireOp",EDGE,"E33")])]});
            var Q41;
            Q41=makeQuery(id+"F20.opExtrude","SWEPT_FACE",FACE,{"disambiguationData":[OSD([sQuery(id+"F19.wireOp",EDGE,"E34")])]});
            var Q42;
            Q42=makeQuery(id+"F20.boolean.opBoolean","INTERSECT",EDGE,{"derivedFrom":[makeQuery(id+"F6.boolean.opBoolean","COPY",FACE,{"derivedFrom":makeQuery(id+"F6.opExtrude","CAP_FACE",FACE,{"disambiguationData":[OSD([sQuery(id+"F0.wireOp",EDGE,"E2")])],"isStart":true})}),makeQuery(id+"F20.opExtrude","SWEPT_FACE",FACE,{"disambiguationData":[OSD([sQuery(id+"F19.wireOp",EDGE,"E25")])]})]});
            var Q43;
            Q43=makeQuery(id+"F20.opExtrude","SWEPT_FACE",FACE,{"disambiguationData":[OSD([sQuery(id+"F19.wireOp",EDGE,"E37")])]});
            var Q44;
            Q44=makeQuery(id+"F20.opExtrude","SWEPT_EDGE",EDGE,{"disambiguationData":[OSD([sQuery(id+"F19.wireOp",EDGE,"E23"),sQuery(id+"F19.wireOp",EDGE,"E24")])]});
            var Q45;
            Q45=makeQuery(id+"F20.opExtrude","SWEPT_FACE",FACE,{"disambiguationData":[OSD([sQuery(id+"F19.wireOp",EDGE,"E23")])]});
            var Q46;
            Q46=makeQuery(id+"F20.opExtrude","SWEPT_EDGE",EDGE,{"disambiguationData":[OSD([sQuery(id+"F19.wireOp",EDGE,"E24"),sQuery(id+"F19.wireOp",EDGE,"E25")])]});
            var Q47;
            Q47=makeQuery(id+"F20.opExtrude","SWEPT_EDGE",EDGE,{"disambiguationData":[OSD([sQuery(id+"F19.wireOp",EDGE,"E25"),sQuery(id+"F19.wireOp",EDGE,"E26")])]});
            var Q48;
            Q48=makeQuery(id+"F20.opExtrude","SWEPT_EDGE",EDGE,{"disambiguationData":[OSD([sQuery(id+"F19.wireOp",EDGE,"E10.bottom"),sQuery(id+"F19.wireOp",EDGE,"E10.left")])]});
            var Q49;
            Q49=makeQuery(id+"F20.opExtrude","SWEPT_EDGE",EDGE,{"disambiguationData":[OSD([sQuery(id+"F19.wireOp",EDGE,"E10.bottom"),sQuery(id+"F19.wireOp",EDGE,"E10.right")])]});
            var Q50;
            Q50=makeQuery(id+"F20.opExtrude","SWEPT_EDGE",EDGE,{"disambiguationData":[OSD([sQuery(id+"F19.wireOp",EDGE,"E10.top"),sQuery(id+"F19.wireOp",EDGE,"E10.left")])]});
            var Q51;
            Q51=makeQuery(id+"F20.opExtrude","SWEPT_FACE",FACE,{"disambiguationData":[OSD([sQuery(id+"F19.wireOp",EDGE,"E10.top")])]});
            var Q52;
            Q52=makeQuery(id+"F20.opExtrude","SWEPT_EDGE",EDGE,{"disambiguationData":[OSD([sQuery(id+"F19.wireOp",EDGE,"E10.top"),sQuery(id+"F19.wireOp",EDGE,"E10.right")])]});
            var Q53;
            Q53=makeQuery(id+"F20.opExtrude","SWEPT_FACE",FACE,{"disambiguationData":[OSD([sQuery(id+"F19.wireOp",EDGE,"E10.left")])]});
            var Q54;
            Q54=makeQuery(id+"F20.opExtrude","SWEPT_EDGE",EDGE,{"disambiguationData":[OSD([sQuery(id+"F19.wireOp",EDGE,"E15"),sQuery(id+"F19.wireOp",EDGE,"E26")])]});
            var Q55;
            Q55=makeQuery(id+"F20.opExtrude","SWEPT_EDGE",EDGE,{"disambiguationData":[OSD([sQuery(id+"F19.wireOp",EDGE,"E15"),sQuery(id+"F19.wireOp",EDGE,"E16")])]});
            var Q56;
            Q56=makeQuery(id+"F20.opExtrude","SWEPT_FACE",FACE,{"disambiguationData":[OSD([sQuery(id+"F19.wireOp",EDGE,"E15")])]});
            var Q57;
            Q57=makeQuery(id+"F20.opExtrude","SWEPT_EDGE",EDGE,{"disambiguationData":[OSD([sQuery(id+"F19.wireOp",EDGE,"E16"),sQuery(id+"F19.wireOp",EDGE,"E17")])]});
            var Q58;
            Q58=makeQuery(id+"F20.opExtrude","SWEPT_EDGE",EDGE,{"disambiguationData":[OSD([sQuery(id+"F19.wireOp",EDGE,"E17"),sQuery(id+"F19.wireOp",EDGE,"E18")])]});
            var Q59;
            Q59=makeQuery(id+"F20.opExtrude","SWEPT_FACE",FACE,{"disambiguationData":[OSD([sQuery(id+"F19.wireOp",EDGE,"E17")])]});
            var Q60;
            Q60=makeQuery(id+"F20.opExtrude","SWEPT_EDGE",EDGE,{"disambiguationData":[OSD([sQuery(id+"F19.wireOp",EDGE,"E18"),sQuery(id+"F19.wireOp",EDGE,"E19")])]});
            var Q61;
            Q61=makeQuery(id+"F20.opExtrude","SWEPT_FACE",FACE,{"disambiguationData":[OSD([sQuery(id+"F19.wireOp",EDGE,"E18")])]});
            var Q62;
            Q62=makeQuery(id+"F20.opExtrude","SWEPT_EDGE",EDGE,{"disambiguationData":[OSD([sQuery(id+"F19.wireOp",EDGE,"E19"),sQuery(id+"F19.wireOp",EDGE,"E20")])]});
            var Q63;
            Q63=makeQuery(id+"F20.opExtrude","SWEPT_FACE",FACE,{"disambiguationData":[OSD([sQuery(id+"F19.wireOp",EDGE,"E19")])]});
            var Q64;
            Q64=makeQuery(id+"F20.opExtrude","SWEPT_EDGE",EDGE,{"disambiguationData":[OSD([sQuery(id+"F19.wireOp",EDGE,"E20"),sQuery(id+"F19.wireOp",EDGE,"E21")])]});
            var Q65;
            Q65=makeQuery(id+"F20.opExtrude","SWEPT_EDGE",EDGE,{"disambiguationData":[OSD([sQuery(id+"F19.wireOp",EDGE,"E21"),sQuery(id+"F19.wireOp",EDGE,"E22")])]});
            var Q66;
            Q66=makeQuery(id+"F20.opExtrude","SWEPT_EDGE",EDGE,{"disambiguationData":[OSD([sQuery(id+"F19.wireOp",EDGE,"E22"),sQuery(id+"F19.wireOp",EDGE,"E23")])]});
            var Q67;
            Q67=makeQuery(id+"F20.opExtrude","SWEPT_FACE",FACE,{"disambiguationData":[OSD([sQuery(id+"F19.wireOp",EDGE,"E22")])]});
            var Q68;
            Q68=makeQuery(id+"F20.opExtrude","CAP_EDGE",EDGE,{"disambiguationData":[OSD([sQuery(id+"F19.wireOp",EDGE,"E20")])],"isStart":false});
            var Q69;
            Q69=makeQuery(id+"F20.opExtrude","CAP_EDGE",EDGE,{"disambiguationData":[OSD([sQuery(id+"F19.wireOp",EDGE,"E10.left")])],"isStart":false});
            var Q70;
            Q70=makeQuery(id+"F20.opExtrude","CAP_EDGE",EDGE,{"disambiguationData":[OSD([sQuery(id+"F19.wireOp",EDGE,"E10.right")])],"isStart":false});
            var Q71;
            Q71=makeQuery(id+"F20.opExtrude","CAP_EDGE",EDGE,{"disambiguationData":[OSD([sQuery(id+"F19.wireOp",EDGE,"E38")])],"isStart":false});
            var Q72;
            Q72=makeQuery(id+"F20.opExtrude","CAP_EDGE",EDGE,{"disambiguationData":[OSD([sQuery(id+"F19.wireOp",EDGE,"E32")])],"isStart":false});
            var Q73;
            Q73=makeQuery(id+"F20.opExtrude","CAP_EDGE",EDGE,{"disambiguationData":[OSD([sQuery(id+"F19.wireOp",EDGE,"E26")])],"isStart":false});
            var Q74;
            Q74=makeQuery(id+"F20.boolean.opBoolean","INTERSECT",EDGE,{"derivedFrom":[makeQuery(id+"F6.boolean.opBoolean","COPY",FACE,{"derivedFrom":makeQuery(id+"F6.opExtrude","CAP_FACE",FACE,{"disambiguationData":[OSD([sQuery(id+"F0.wireOp",EDGE,"E2")])],"isStart":true})}),makeQuery(id+"F20.opExtrude","SWEPT_FACE",FACE,{"disambiguationData":[OSD([sQuery(id+"F19.wireOp",EDGE,"E10.top")])]})]});
            var Q75;
            Q75=makeQuery(id+"F20.boolean.opBoolean","INTERSECT",EDGE,{"derivedFrom":[makeQuery(id+"F6.boolean.opBoolean","COPY",FACE,{"derivedFrom":makeQuery(id+"F6.opExtrude","CAP_FACE",FACE,{"disambiguationData":[OSD([sQuery(id+"F0.wireOp",EDGE,"E2")])],"isStart":true})}),makeQuery(id+"F20.opExtrude","SWEPT_FACE",FACE,{"disambiguationData":[OSD([sQuery(id+"F19.wireOp",EDGE,"E28")])]})]});
            var Q76;
            Q76=makeQuery(id+"F20.boolean.opBoolean","INTERSECT",EDGE,{"derivedFrom":[makeQuery(id+"F6.boolean.opBoolean","COPY",FACE,{"derivedFrom":makeQuery(id+"F6.opExtrude","CAP_FACE",FACE,{"disambiguationData":[OSD([sQuery(id+"F0.wireOp",EDGE,"E2")])],"isStart":true})}),makeQuery(id+"F20.opExtrude","SWEPT_FACE",FACE,{"disambiguationData":[OSD([sQuery(id+"F19.wireOp",EDGE,"E10.left")])]})]});
            var Q77;
            Q77=makeQuery(id+"F20.boolean.opBoolean","INTERSECT",EDGE,{"derivedFrom":[makeQuery(id+"F6.boolean.opBoolean","COPY",FACE,{"derivedFrom":makeQuery(id+"F6.opExtrude","CAP_FACE",FACE,{"disambiguationData":[OSD([sQuery(id+"F0.wireOp",EDGE,"E2")])],"isStart":true})}),makeQuery(id+"F20.opExtrude","SWEPT_FACE",FACE,{"disambiguationData":[OSD([sQuery(id+"F19.wireOp",EDGE,"E15")])]})]});
            var Q78;
            Q78=makeQuery(id+"F20.boolean.opBoolean","INTERSECT",EDGE,{"derivedFrom":[makeQuery(id+"F6.boolean.opBoolean","COPY",FACE,{"derivedFrom":makeQuery(id+"F6.opExtrude","CAP_FACE",FACE,{"disambiguationData":[OSD([sQuery(id+"F0.wireOp",EDGE,"E2")])],"isStart":true})}),makeQuery(id+"F20.opExtrude","SWEPT_FACE",FACE,{"disambiguationData":[OSD([sQuery(id+"F19.wireOp",EDGE,"E31")])]})]});
            var Q79;
            Q79=makeQuery(id+"F20.opExtrude","SWEPT_EDGE",EDGE,{"disambiguationData":[OSD([sQuery(id+"F19.wireOp",EDGE,"E27"),sQuery(id+"F19.wireOp",EDGE,"E28")])]});
            var Q80;
            Q80=makeQuery(id+"F20.boolean.opBoolean","INTERSECT",EDGE,{"derivedFrom":[makeQuery(id+"F6.boolean.opBoolean","COPY",FACE,{"derivedFrom":makeQuery(id+"F6.opExtrude","CAP_FACE",FACE,{"disambiguationData":[OSD([sQuery(id+"F0.wireOp",EDGE,"E2")])],"isStart":true})}),makeQuery(id+"F20.opExtrude","SWEPT_FACE",FACE,{"disambiguationData":[OSD([sQuery(id+"F19.wireOp",EDGE,"E32")])]})]});
            var Q81;
            Q81=makeQuery(id+"F20.opExtrude","SWEPT_FACE",FACE,{"disambiguationData":[OSD([sQuery(id+"F19.wireOp",EDGE,"E27")])]});
            var Q82;
            Q82=makeQuery(id+"F20.opExtrude","SWEPT_EDGE",EDGE,{"disambiguationData":[OSD([sQuery(id+"F19.wireOp",EDGE,"E28"),sQuery(id+"F19.wireOp",EDGE,"E29")])]});
            var Q83;
            Q83=makeQuery(id+"F20.opExtrude","SWEPT_EDGE",EDGE,{"disambiguationData":[OSD([sQuery(id+"F19.wireOp",EDGE,"E29"),sQuery(id+"F19.wireOp",EDGE,"E30")])]});
            var Q84;
            Q84=makeQuery(id+"F20.boolean.opBoolean","INTERSECT",EDGE,{"derivedFrom":[makeQuery(id+"F6.boolean.opBoolean","COPY",FACE,{"derivedFrom":makeQuery(id+"F6.opExtrude","CAP_FACE",FACE,{"disambiguationData":[OSD([sQuery(id+"F0.wireOp",EDGE,"E2")])],"isStart":true})}),makeQuery(id+"F20.opExtrude","SWEPT_FACE",FACE,{"disambiguationData":[OSD([sQuery(id+"F19.wireOp",EDGE,"E18")])]})]});
            var Q85;
            Q85=makeQuery(id+"F20.boolean.opBoolean","INTERSECT",EDGE,{"derivedFrom":[makeQuery(id+"F6.boolean.opBoolean","COPY",FACE,{"derivedFrom":makeQuery(id+"F6.opExtrude","CAP_FACE",FACE,{"disambiguationData":[OSD([sQuery(id+"F0.wireOp",EDGE,"E2")])],"isStart":true})}),makeQuery(id+"F20.opExtrude","SWEPT_FACE",FACE,{"disambiguationData":[OSD([sQuery(id+"F19.wireOp",EDGE,"E34")])]})]});
            var Q86;
            Q86=makeQuery(id+"F20.opExtrude","SWEPT_FACE",FACE,{"disambiguationData":[OSD([sQuery(id+"F19.wireOp",EDGE,"E29")])]});
            var Q87;
            Q87=makeQuery(id+"F20.opExtrude","SWEPT_EDGE",EDGE,{"disambiguationData":[OSD([sQuery(id+"F19.wireOp",EDGE,"E30"),sQuery(id+"F19.wireOp",EDGE,"E31")])]});
            var Q88;
            Q88=makeQuery(id+"F20.boolean.opBoolean","INTERSECT",EDGE,{"derivedFrom":[makeQuery(id+"F6.boolean.opBoolean","COPY",FACE,{"derivedFrom":makeQuery(id+"F6.opExtrude","CAP_FACE",FACE,{"disambiguationData":[OSD([sQuery(id+"F0.wireOp",EDGE,"E2")])],"isStart":true})}),makeQuery(id+"F20.opExtrude","SWEPT_FACE",FACE,{"disambiguationData":[OSD([sQuery(id+"F19.wireOp",EDGE,"E19")])]})]});
            var Q89;
            Q89=makeQuery(id+"F20.boolean.opBoolean","INTERSECT",EDGE,{"derivedFrom":[makeQuery(id+"F6.boolean.opBoolean","COPY",FACE,{"derivedFrom":makeQuery(id+"F6.opExtrude","CAP_FACE",FACE,{"disambiguationData":[OSD([sQuery(id+"F0.wireOp",EDGE,"E2")])],"isStart":true})}),makeQuery(id+"F20.opExtrude","SWEPT_FACE",FACE,{"disambiguationData":[OSD([sQuery(id+"F19.wireOp",EDGE,"E35")])]})]});
            var Q90;
            Q90=makeQuery(id+"F20.opExtrude","SWEPT_FACE",FACE,{"disambiguationData":[OSD([sQuery(id+"F19.wireOp",EDGE,"E30")])]});
            var Q91;
            Q91=makeQuery(id+"F20.boolean.opBoolean","INTERSECT",EDGE,{"derivedFrom":[makeQuery(id+"F6.boolean.opBoolean","COPY",FACE,{"derivedFrom":makeQuery(id+"F6.opExtrude","CAP_FACE",FACE,{"disambiguationData":[OSD([sQuery(id+"F0.wireOp",EDGE,"E2")])],"isStart":true})}),makeQuery(id+"F20.opExtrude","SWEPT_FACE",FACE,{"disambiguationData":[OSD([sQuery(id+"F19.wireOp",EDGE,"E20")])]})]});
            var Q92;
            Q92=makeQuery(id+"F20.opExtrude","SWEPT_FACE",FACE,{"disambiguationData":[OSD([sQuery(id+"F19.wireOp",EDGE,"E31")])]});
            var Q93;
            Q93=makeQuery(id+"F20.boolean.opBoolean","INTERSECT",EDGE,{"derivedFrom":[makeQuery(id+"F6.boolean.opBoolean","COPY",FACE,{"derivedFrom":makeQuery(id+"F6.opExtrude","CAP_FACE",FACE,{"disambiguationData":[OSD([sQuery(id+"F0.wireOp",EDGE,"E2")])],"isStart":true})}),makeQuery(id+"F20.opExtrude","SWEPT_FACE",FACE,{"disambiguationData":[OSD([sQuery(id+"F19.wireOp",EDGE,"E37")])]})]});
            var Q94;
            Q94=makeQuery(id+"F20.opExtrude","SWEPT_EDGE",EDGE,{"disambiguationData":[OSD([sQuery(id+"F19.wireOp",EDGE,"E33"),sQuery(id+"F19.wireOp",EDGE,"E34")])]});
            var Q95;
            Q95=makeQuery(id+"F20.boolean.opBoolean","INTERSECT",EDGE,{"derivedFrom":[makeQuery(id+"F6.boolean.opBoolean","COPY",FACE,{"derivedFrom":makeQuery(id+"F6.opExtrude","CAP_FACE",FACE,{"disambiguationData":[OSD([sQuery(id+"F0.wireOp",EDGE,"E2")])],"isStart":true})}),makeQuery(id+"F20.opExtrude","SWEPT_FACE",FACE,{"disambiguationData":[OSD([sQuery(id+"F19.wireOp",EDGE,"E22")])]})]});
            var Q96;
            Q96=makeQuery(id+"F20.boolean.opBoolean","INTERSECT",EDGE,{"derivedFrom":[makeQuery(id+"F6.boolean.opBoolean","COPY",FACE,{"derivedFrom":makeQuery(id+"F6.opExtrude","CAP_FACE",FACE,{"disambiguationData":[OSD([sQuery(id+"F0.wireOp",EDGE,"E2")])],"isStart":true})}),makeQuery(id+"F20.opExtrude","SWEPT_FACE",FACE,{"disambiguationData":[OSD([sQuery(id+"F19.wireOp",EDGE,"E38")])]})]});
            var Q97;
            Q97=makeQuery(id+"F20.opExtrude","SWEPT_EDGE",EDGE,{"disambiguationData":[OSD([sQuery(id+"F19.wireOp",EDGE,"E34"),sQuery(id+"F19.wireOp",EDGE,"E35")])]});
            var Q98;
            Q98=makeQuery(id+"F20.boolean.opBoolean","INTERSECT",EDGE,{"derivedFrom":[makeQuery(id+"F6.boolean.opBoolean","COPY",FACE,{"derivedFrom":makeQuery(id+"F6.opExtrude","CAP_FACE",FACE,{"disambiguationData":[OSD([sQuery(id+"F0.wireOp",EDGE,"E2")])],"isStart":true})}),makeQuery(id+"F20.opExtrude","SWEPT_FACE",FACE,{"disambiguationData":[OSD([sQuery(id+"F19.wireOp",EDGE,"E23")])]})]});
            var Q99;
            Q99=makeQuery(id+"F20.opExtrude","SWEPT_EDGE",EDGE,{"disambiguationData":[OSD([sQuery(id+"F19.wireOp",EDGE,"E35"),sQuery(id+"F19.wireOp",EDGE,"E36")])]});
            var Q100;
            Q100=makeQuery(id+"F20.boolean.opBoolean","INTERSECT",EDGE,{"derivedFrom":[makeQuery(id+"F6.boolean.opBoolean","COPY",FACE,{"derivedFrom":makeQuery(id+"F6.opExtrude","CAP_FACE",FACE,{"disambiguationData":[OSD([sQuery(id+"F0.wireOp",EDGE,"E2")])],"isStart":true})}),makeQuery(id+"F20.opExtrude","SWEPT_FACE",FACE,{"disambiguationData":[OSD([sQuery(id+"F19.wireOp",EDGE,"E24")])]})]});
            var Q101;
            Q101=makeQuery(id+"F20.opExtrude","SWEPT_FACE",FACE,{"disambiguationData":[OSD([sQuery(id+"F19.wireOp",EDGE,"E35")])]});
            var Q102;
            Q102=makeQuery(id+"F20.opExtrude","SWEPT_EDGE",EDGE,{"disambiguationData":[OSD([sQuery(id+"F19.wireOp",EDGE,"E36"),sQuery(id+"F19.wireOp",EDGE,"E37")])]});
            var Q103;
            Q103=makeQuery(id+"F20.opExtrude","SWEPT_FACE",FACE,{"disambiguationData":[OSD([sQuery(id+"F19.wireOp",EDGE,"E36")])]});
            var Q104;
            Q104=makeQuery(id+"F20.boolean.opBoolean","INTERSECT",EDGE,{"derivedFrom":[makeQuery(id+"F6.boolean.opBoolean","COPY",FACE,{"derivedFrom":makeQuery(id+"F6.opExtrude","CAP_FACE",FACE,{"disambiguationData":[OSD([sQuery(id+"F0.wireOp",EDGE,"E2")])],"isStart":true})}),makeQuery(id+"F20.opExtrude","SWEPT_FACE",FACE,{"disambiguationData":[OSD([sQuery(id+"F19.wireOp",EDGE,"E10.bottom")])]})]});
            var Q105;
            Q105=makeQuery(id+"F20.boolean.opBoolean","INTERSECT",EDGE,{"derivedFrom":[makeQuery(id+"F6.boolean.opBoolean","COPY",FACE,{"derivedFrom":makeQuery(id+"F6.opExtrude","CAP_FACE",FACE,{"disambiguationData":[OSD([sQuery(id+"F0.wireOp",EDGE,"E2")])],"isStart":true})}),makeQuery(id+"F20.opExtrude","SWEPT_FACE",FACE,{"disambiguationData":[OSD([sQuery(id+"F19.wireOp",EDGE,"E27")])]})]});
            var Q106;
            Q106=makeQuery(id+"F20.opExtrude","SWEPT_FACE",FACE,{"disambiguationData":[OSD([sQuery(id+"F19.wireOp",EDGE,"E38")])]});
            var Q107;
            Q107=makeQuery(id+"F20.opExtrude","SWEPT_FACE",FACE,{"disambiguationData":[OSD([sQuery(id+"F19.wireOp",EDGE,"E20")])]});
            var Q108;
            Q108=makeQuery(id+"F20.boolean.opBoolean","INTERSECT",EDGE,{"derivedFrom":[makeQuery(id+"F6.boolean.opBoolean","COPY",FACE,{"derivedFrom":makeQuery(id+"F6.opExtrude","CAP_FACE",FACE,{"disambiguationData":[OSD([sQuery(id+"F0.wireOp",EDGE,"E2")])],"isStart":true})}),makeQuery(id+"F20.opExtrude","SWEPT_FACE",FACE,{"disambiguationData":[OSD([sQuery(id+"F19.wireOp",EDGE,"E30")])]})]});
            var Q109;
            Q109=makeQuery(id+"F20.opExtrude","SWEPT_EDGE",EDGE,{"disambiguationData":[OSD([sQuery(id+"F19.wireOp",EDGE,"E27"),sQuery(id+"F19.wireOp",EDGE,"E38")])]});
            var Q110;
            Q110=makeQuery(id+"F20.opExtrude","SWEPT_EDGE",EDGE,{"disambiguationData":[OSD([sQuery(id+"F19.wireOp",EDGE,"E31"),sQuery(id+"F19.wireOp",EDGE,"E32")])]});
            var Q111;
            Q111=makeQuery(id+"F20.boolean.opBoolean","INTERSECT",EDGE,{"derivedFrom":[makeQuery(id+"F6.boolean.opBoolean","COPY",FACE,{"derivedFrom":makeQuery(id+"F6.opExtrude","CAP_FACE",FACE,{"disambiguationData":[OSD([sQuery(id+"F0.wireOp",EDGE,"E2")])],"isStart":true})}),makeQuery(id+"F20.opExtrude","SWEPT_FACE",FACE,{"disambiguationData":[OSD([sQuery(id+"F19.wireOp",EDGE,"E36")])]})]});
            var Q112;
            Q112=makeQuery(id+"F20.opExtrude","SWEPT_EDGE",EDGE,{"disambiguationData":[OSD([sQuery(id+"F19.wireOp",EDGE,"E32"),sQuery(id+"F19.wireOp",EDGE,"E33")])]});
            var Q113;
            Q113=makeQuery(id+"F20.opExtrude","SWEPT_EDGE",EDGE,{"disambiguationData":[OSD([sQuery(id+"F19.wireOp",EDGE,"E37"),sQuery(id+"F19.wireOp",EDGE,"E38")])]});
            var Q114;
            Q114=makeQuery(id+"F20.boolean.opBoolean","INTERSECT",EDGE,{"derivedFrom":[makeQuery(id+"F6.boolean.opBoolean","COPY",FACE,{"derivedFrom":makeQuery(id+"F6.opExtrude","CAP_FACE",FACE,{"disambiguationData":[OSD([sQuery(id+"F0.wireOp",EDGE,"E2")])],"isStart":true})}),makeQuery(id+"F20.opExtrude","SWEPT_FACE",FACE,{"disambiguationData":[OSD([sQuery(id+"F19.wireOp",EDGE,"E26")])]})]});
            fillet(context, id + "F21", {"entities" : qUnion([Q0, Q1, Q2, Q3, Q4, Q5, Q6, Q7, Q8, Q9, Q10, Q11, Q12, Q13, Q14, Q15, Q16, Q17, Q18, Q19, Q20, Q21, Q22, Q23, Q24, Q25, Q26, Q27, Q28, Q29, Q30, Q31, Q32, Q33, Q34, Q35, Q36, Q37, Q38, Q39, Q40, Q41, Q42, Q43, Q44, Q45, Q46, Q47, Q48, Q49, Q50, Q51, Q52, Q53, Q54, Q55, Q56, Q57, Q58, Q59, Q60, Q61, Q62, Q63, Q64, Q65, Q66, Q67, Q68, Q69, Q70, Q71, Q72, Q73, Q74, Q75, Q76, Q77, Q78, Q79, Q80, Q81, Q82, Q83, Q84, Q85, Q86, Q87, Q88, Q89, Q90, Q91, Q92, Q93, Q94, Q95, Q96, Q97, Q98, Q99, Q100, Q101, Q102, Q103, Q104, Q105, Q106, Q107, Q108, Q109, Q110, Q111, Q112, Q113, Q114]), "radius" : 0.4 * mm, "tangentPropagation" : true, "allowEdgeOverflow" : false});
        }
        {
            var Q0;
            Q0=makeQuery(id+"F20.opExtrude","CAP_EDGE",EDGE,{"disambiguationData":[OSD([sQuery(id+"F19.wireOp",EDGE,"E43")])],"isStart":false});
            var Q1;
            Q1=makeQuery(id+"F20.opExtrude","CAP_EDGE",EDGE,{"disambiguationData":[OSD([sQuery(id+"F19.wireOp",EDGE,"E47")])],"isStart":false});
            var Q2;
            Q2=makeQuery(id+"F20.boolean.opBoolean","INTERSECT",EDGE,{"derivedFrom":[makeQuery(id+"F7.opFillet","BLEND_FACE",FACE,{"disambiguationData":[OSD([sQuery(id+"F0.wireOp",EDGE,"E2")])]}),makeQuery(id+"F20.opExtrude","SWEPT_FACE",FACE,{"disambiguationData":[OSD([sQuery(id+"F19.wireOp",EDGE,"E47")])]})]});
            var Q3;
            Q3=makeQuery(id+"F20.boolean.opBoolean","INTERSECT",EDGE,{"derivedFrom":[makeQuery(id+"F6.boolean.opBoolean","COPY",FACE,{"derivedFrom":makeQuery(id+"F6.opExtrude","CAP_FACE",FACE,{"disambiguationData":[OSD([sQuery(id+"F0.wireOp",EDGE,"E2")])],"isStart":true})}),makeQuery(id+"F20.opExtrude","SWEPT_FACE",FACE,{"disambiguationData":[OSD([sQuery(id+"F19.wireOp",EDGE,"E47")])]})]});
            var Q4;
            Q4=makeQuery(id+"F20.boolean.opBoolean","INTERSECT",EDGE,{"derivedFrom":[makeQuery(id+"F6.boolean.opBoolean","COPY",FACE,{"derivedFrom":makeQuery(id+"F6.opExtrude","CAP_FACE",FACE,{"disambiguationData":[OSD([sQuery(id+"F0.wireOp",EDGE,"E2")])],"isStart":true})}),makeQuery(id+"F20.opExtrude","SWEPT_FACE",FACE,{"disambiguationData":[OSD([sQuery(id+"F19.wireOp",EDGE,"E45")])]})]});
            var Q5;
            Q5=makeQuery(id+"F20.boolean.opBoolean","INTERSECT",EDGE,{"derivedFrom":[makeQuery(id+"F7.opFillet","BLEND_FACE",FACE,{"disambiguationData":[OSD([sQuery(id+"F0.wireOp",EDGE,"E2")])]}),makeQuery(id+"F20.opExtrude","SWEPT_FACE",FACE,{"disambiguationData":[OSD([sQuery(id+"F19.wireOp",EDGE,"E46")])]})]});
            var Q6;
            Q6=makeQuery(id+"F20.boolean.opBoolean","INTERSECT",EDGE,{"derivedFrom":[makeQuery(id+"F7.opFillet","BLEND_FACE",FACE,{"disambiguationData":[OSD([sQuery(id+"F0.wireOp",EDGE,"E2")])]}),makeQuery(id+"F20.opExtrude","SWEPT_FACE",FACE,{"disambiguationData":[OSD([sQuery(id+"F19.wireOp",EDGE,"E44")])]})]});
            var Q7;
            Q7=makeQuery(id+"F20.boolean.opBoolean","INTERSECT",EDGE,{"derivedFrom":[makeQuery(id+"F6.boolean.opBoolean","COPY",FACE,{"derivedFrom":makeQuery(id+"F6.opExtrude","CAP_FACE",FACE,{"disambiguationData":[OSD([sQuery(id+"F0.wireOp",EDGE,"E2")])],"isStart":true})}),makeQuery(id+"F20.opExtrude","SWEPT_FACE",FACE,{"disambiguationData":[OSD([sQuery(id+"F19.wireOp",EDGE,"E44")])]})]});
            var Q8;
            Q8=makeQuery(id+"F20.opExtrude","CAP_EDGE",EDGE,{"disambiguationData":[OSD([sQuery(id+"F19.wireOp",EDGE,"E46")])],"isStart":false});
            var Q9;
            Q9=makeQuery(id+"F20.opExtrude","CAP_EDGE",EDGE,{"disambiguationData":[OSD([sQuery(id+"F19.wireOp",EDGE,"E44")])],"isStart":false});
            var Q10;
            Q10=makeQuery(id+"F20.opExtrude","SWEPT_EDGE",EDGE,{"disambiguationData":[OSD([sQuery(id+"F19.wireOp",EDGE,"E43"),sQuery(id+"F19.wireOp",EDGE,"E44"),sQuery(id+"F19.wireOp",EDGE,"E46")])]});
            var Q11;
            Q11=makeQuery(id+"F20.opExtrude","SWEPT_EDGE",EDGE,{"disambiguationData":[OSD([sQuery(id+"F19.wireOp",EDGE,"E43"),sQuery(id+"F19.wireOp",EDGE,"E44"),sQuery(id+"F19.wireOp",EDGE,"E45")])]});
            var Q12;
            Q12=makeQuery(id+"F20.opExtrude","CAP_EDGE",EDGE,{"disambiguationData":[OSD([sQuery(id+"F19.wireOp",EDGE,"E45")])],"isStart":false});
            var Q13;
            Q13=makeQuery(id+"F20.opExtrude","CAP_EDGE",EDGE,{"disambiguationData":[OSD([sQuery(id+"F19.wireOp",EDGE,"E40")])],"isStart":false});
            var Q14;
            Q14=makeQuery(id+"F20.opExtrude","CAP_EDGE",EDGE,{"disambiguationData":[OSD([sQuery(id+"F19.wireOp",EDGE,"E41")])],"isStart":false});
            var Q15;
            Q15=makeQuery(id+"F20.opExtrude","CAP_EDGE",EDGE,{"disambiguationData":[OSD([sQuery(id+"F19.wireOp",EDGE,"E42")])],"isStart":false});
            var Q16;
            Q16=makeQuery(id+"F20.opExtrude","SWEPT_EDGE",EDGE,{"disambiguationData":[OSD([sQuery(id+"F19.wireOp",EDGE,"E40"),sQuery(id+"F19.wireOp",EDGE,"E41")])]});
            var Q17;
            Q17=makeQuery(id+"F20.boolean.opBoolean","INTERSECT",EDGE,{"derivedFrom":[makeQuery(id+"F6.boolean.opBoolean","COPY",FACE,{"derivedFrom":makeQuery(id+"F6.opExtrude","CAP_FACE",FACE,{"disambiguationData":[OSD([sQuery(id+"F0.wireOp",EDGE,"E2")])],"isStart":true})}),makeQuery(id+"F20.opExtrude","SWEPT_FACE",FACE,{"disambiguationData":[OSD([sQuery(id+"F19.wireOp",EDGE,"E40")])]})]});
            var Q18;
            Q18=makeQuery(id+"F20.boolean.opBoolean","INTERSECT",EDGE,{"derivedFrom":[makeQuery(id+"F7.opFillet","BLEND_FACE",FACE,{"disambiguationData":[OSD([sQuery(id+"F0.wireOp",EDGE,"E2")])]}),makeQuery(id+"F20.opExtrude","SWEPT_FACE",FACE,{"disambiguationData":[OSD([sQuery(id+"F19.wireOp",EDGE,"E40")])]})]});
            var Q19;
            Q19=makeQuery(id+"F20.opExtrude","SWEPT_EDGE",EDGE,{"disambiguationData":[OSD([sQuery(id+"F19.wireOp",EDGE,"E40"),sQuery(id+"F19.wireOp",EDGE,"E42")])]});
            var Q20;
            Q20=makeQuery(id+"F20.boolean.opBoolean","INTERSECT",EDGE,{"derivedFrom":[makeQuery(id+"F7.opFillet","BLEND_FACE",FACE,{"disambiguationData":[OSD([sQuery(id+"F0.wireOp",EDGE,"E2")])]}),makeQuery(id+"F20.opExtrude","SWEPT_FACE",FACE,{"disambiguationData":[OSD([sQuery(id+"F19.wireOp",EDGE,"E42")])]})]});
            var Q21;
            Q21=makeQuery(id+"F20.boolean.opBoolean","INTERSECT",EDGE,{"derivedFrom":[makeQuery(id+"F7.opFillet","BLEND_FACE",FACE,{"disambiguationData":[OSD([sQuery(id+"F0.wireOp",EDGE,"E2")])]}),makeQuery(id+"F20.opExtrude","SWEPT_FACE",FACE,{"disambiguationData":[OSD([sQuery(id+"F19.wireOp",EDGE,"E43")])]})]});
            var Q22;
            Q22=makeQuery(id+"F20.boolean.opBoolean","INTERSECT",EDGE,{"derivedFrom":[makeQuery(id+"F6.boolean.opBoolean","COPY",FACE,{"derivedFrom":makeQuery(id+"F6.opExtrude","CAP_FACE",FACE,{"disambiguationData":[OSD([sQuery(id+"F0.wireOp",EDGE,"E2")])],"isStart":true})}),makeQuery(id+"F20.opExtrude","SWEPT_FACE",FACE,{"disambiguationData":[OSD([sQuery(id+"F19.wireOp",EDGE,"E43")])]})]});
            var Q23;
            Q23=makeQuery(id+"F20.boolean.opBoolean","INTERSECT",EDGE,{"derivedFrom":[makeQuery(id+"F6.boolean.opBoolean","COPY",FACE,{"derivedFrom":makeQuery(id+"F6.opExtrude","CAP_FACE",FACE,{"disambiguationData":[OSD([sQuery(id+"F0.wireOp",EDGE,"E2")])],"isStart":true})}),makeQuery(id+"F20.opExtrude","SWEPT_FACE",FACE,{"disambiguationData":[OSD([sQuery(id+"F19.wireOp",EDGE,"E41")])]})]});
            fillet(context, id + "F22", {"entities" : qUnion([Q0, Q1, Q2, Q3, Q4, Q5, Q6, Q7, Q8, Q9, Q10, Q11, Q12, Q13, Q14, Q15, Q16, Q17, Q18, Q19, Q20, Q21, Q22, Q23]), "radius" : 0.3 * mm, "tangentPropagation" : true, "allowEdgeOverflow" : false});
        }
    });
